FCSTD DOCUMENT  (FreeCAD 0.17R13541 (Git))
Label: SANPORobotLaserCut2DModel
License: All rights reserved
LicenseURL: http://en.wikipedia.org/wiki/All_rights_reserved
objects: Sketcher::SketchObject×37, PartDesign::Body×1
note: 38 computed .brp shape members not serialized (recipe doc carries the construction recipe); baked Part::Feature solids carry a one-line shape summary decoded from their .brp

FEATURE [Sketcher::SketchObject] Sketch  label="A4Size"
  MapMode = 5
  Support = -> [XY_Plane]
  sketch-geometry (4):
    g0: LineSegment StartX=0 StartY=0 StartZ=0 EndX=210 EndY=0 EndZ=0
    g1: LineSegment StartX=210 StartY=0 StartZ=0 EndX=210 EndY=297 EndZ=0
    g2: LineSegment StartX=210 StartY=297 StartZ=0 EndX=0 EndY=297 EndZ=0
    g3: LineSegment StartX=0 StartY=297 StartZ=0 EndX=0 EndY=0 EndZ=0
  constraints (11):
    c: Coincident(g0,g1)
    c: Coincident(g1,g2)
    c: Coincident(g2,g3)
    c: Coincident(g3,g0)
    c: Horizontal(g0)
    c: Horizontal(g2)
    c: Vertical(g1)
    c: Vertical(g3)
    c: DistanceY(g3,g3) = 297
    c: DistanceX(g0,g0) = 210
    c: Coincident(g0,g-1)
FEATURE [Sketcher::SketchObject] Sketch025  label="Sketch017"
  MapMode = 5
  Support = -> [XY_Plane]
  sketch-geometry (30):
    g0: LineSegment StartX=101 StartY=286 StartZ=0 EndX=134 EndY=286 EndZ=0
    g1: LineSegment StartX=132 StartY=234 StartZ=0 EndX=103 EndY=234 EndZ=0
    g2: ArcOfCircle CenterX=132 CenterY=236 CenterZ=0 NormalX=0 NormalY=0 NormalZ=1 AngleXU=0 Radius=2 StartAngle=4.71239 EndAngle=6.28319
    g3: ArcOfCircle CenterX=103 CenterY=236 CenterZ=0 NormalX=0 NormalY=0 NormalZ=1 AngleXU=0 Radius=2 StartAngle=3.14159 EndAngle=4.71239
    g4: Circle CenterX=117.5 CenterY=281.5 CenterZ=0 NormalX=0 NormalY=0 NormalZ=1 AngleXU=0 Radius=1.5
    g5: Circle CenterX=117.5 CenterY=238.5 CenterZ=0 NormalX=0 NormalY=0 NormalZ=1 AngleXU=0 Radius=1.5
    g6: LineSegment StartX=125 StartY=283 StartZ=0 EndX=130 EndY=283 EndZ=0
    g7: LineSegment StartX=130 StartY=283 StartZ=0 EndX=130 EndY=280 EndZ=0
    g8: LineSegment StartX=130 StartY=280 StartZ=0 EndX=125 EndY=280 EndZ=0
    g9: LineSegment StartX=125 StartY=280 StartZ=0 EndX=125 EndY=283 EndZ=0
    g10: LineSegment StartX=105 StartY=283 StartZ=0 EndX=110 EndY=283 EndZ=0
    g11: LineSegment StartX=110 StartY=283 StartZ=0 EndX=110 EndY=280 EndZ=0
    g12: LineSegment StartX=110 StartY=280 StartZ=0 EndX=105 EndY=280 EndZ=0
    g13: LineSegment StartX=105 StartY=280 StartZ=0 EndX=105 EndY=283 EndZ=0
    g14: LineSegment StartX=105 StartY=240 StartZ=0 EndX=110 EndY=240 EndZ=0
    g15: LineSegment StartX=110 StartY=240 StartZ=0 EndX=110 EndY=237 EndZ=0
    g16: LineSegment StartX=110 StartY=237 StartZ=0 EndX=105 EndY=237 EndZ=0
    g17: LineSegment StartX=105 StartY=237 StartZ=0 EndX=105 EndY=240 EndZ=0
    g18: LineSegment StartX=125 StartY=240 StartZ=0 EndX=130 EndY=240 EndZ=0
    g19: LineSegment StartX=130 StartY=240 StartZ=0 EndX=130 EndY=237 EndZ=0
    g20: LineSegment StartX=130 StartY=237 StartZ=0 EndX=125 EndY=237 EndZ=0
    g21: LineSegment StartX=125 StartY=237 StartZ=0 EndX=125 EndY=240 EndZ=0
    g22: LineSegment StartX=101 StartY=286 StartZ=0 EndX=101 EndY=261.25 EndZ=0
    g23: LineSegment StartX=101 StartY=236 StartZ=0 EndX=101 EndY=260.75 EndZ=0
    g24: LineSegment StartX=117.5 StartY=249 StartZ=0 EndX=118.5 EndY=250.732 EndZ=0
    g25: LineSegment StartX=118.5 StartY=250.732 StartZ=0 EndX=116.5 EndY=250.732 EndZ=0
    g26: LineSegment StartX=116.5 StartY=250.732 StartZ=0 EndX=117.5 EndY=249 EndZ=0
    g27: Circle [constr] CenterX=117.5 CenterY=250.155 CenterZ=0 NormalX=0 NormalY=0 NormalZ=1 AngleXU=0 Radius=1.1547
    g28: LineSegment StartX=134 StartY=286 StartZ=0 EndX=134 EndY=261.25 EndZ=0
    g29: LineSegment StartX=134 StartY=236 StartZ=0 EndX=134 EndY=260.75 EndZ=0
  constraints (91):
    c: Horizontal(g0)
    c: Horizontal(g1)
    c: Tangent(g1,g2) = 1.5708
    c: Tangent(g1,g3) = 1.5708
    c: Radius(g4) = 1.5
    c: Equal(g4,g5)
    c: Coincident(g6,g7)
    c: Coincident(g7,g8)
    c: Coincident(g8,g9)
    c: Coincident(g9,g6)
    c: Horizontal(g6)
    c: Horizontal(g8)
    c: Vertical(g7)
    c: Vertical(g9)
    c: Coincident(g10,g11)
    c: Coincident(g11,g12)
    c: Coincident(g12,g13)
    c: Coincident(g13,g10)
    c: Horizontal(g10)
    c: Horizontal(g12)
    c: Vertical(g11)
    c: Vertical(g13)
    c: Coincident(g14,g15)
    c: Coincident(g15,g16)
    c: Coincident(g16,g17)
    c: Coincident(g17,g14)
    c: Horizontal(g14)
    c: Horizontal(g16)
    c: Vertical(g17)
    c: Coincident(g18,g19)
    c: Coincident(g19,g20)
    c: Coincident(g20,g21)
    c: Coincident(g21,g18)
    c: Horizontal(g18)
    c: Horizontal(g20)
    c: Vertical(g19)
    c: Vertical(g21)
    c: DistanceX(g8,g8) = 5
    c: DistanceY(g9,g9) = 3
    c: DistanceX(g4,g8) = 7.5
    c: DistanceX(g12,g12) = 5
    c: DistanceY(g13,g13) = 3
    c: DistanceX(g11,g4) = 7.5
    c: DistanceX(g20,g20) = 5
    c: DistanceY(g21,g21) = 3
    c: DistanceY(g17,g17) = 3
    c: DistanceX(g16,g16) = 5
    c: DistanceX(g15,g5) = 7.5
    c: DistanceX(g5,g20) = 7.5
    c: Vertical(g22)
    c: Vertical(g23)
    c: DistanceY(g23,g22) = 0.5
    c: Equal(g22,g23)
    c: Tangent(g23,g3) = 1.5708
    c: DistanceX(g3,g16) = 4
    c: DistanceY(g14,g12) = 40
    c: DistanceY(g1,g16) = 3
    c: DistanceY(g10,g0) = 3
    c: DistanceY(g1,g5) = 4.5
    c: DistanceY(g1,g19) = 3
    c: DistanceX(g19,g2) = 4
    c: DistanceY(g4,g0) = 4.5
    c: Vertical(g22,g23)
    c: DistanceY(g6,g0) = 3
    c: Vertical(g15)
    c: Coincident(g0,g22)
    c: DistanceX(g0,g10) = 4
    c: Radius(g2) = 2
    c: Radius(g3) = 2
    c: Coincident(g24,g25)
    c: Coincident(g25,g26)
    c: Coincident(g26,g24)
    c: Equal(g24,g25)
    c: Equal(g24,g26)
    c: PointOnObject(g24,g27)
    c: PointOnObject(g25,g27)
    c: PointOnObject(g26,g27)
    c: Horizontal(g25)
    c: DistanceX(g25,g25) = 2
    c: DistanceY(g1,g24) = 15
    c: Vertical(g28)
    c: Vertical(g29)
    c: Vertical(g28,g29)
    c: DistanceY(g29,g28) = 0.5
    c: Horizontal(g23,g29)
    c: DistanceX(g3,g24) = 16.5
    c: Coincident(g0,g28)
    c: Tangent(g2,g29) = -1.5708
    c: DistanceX(g0,g0) = 33
    c: DistanceX(g1) = 103
    c: DistanceY(g1) = 234
FEATURE [Sketcher::SketchObject] Sketch039
  MapMode = 5
  sketch-geometry (30):
    g0: LineSegment StartX=187 StartY=191 StartZ=0 EndX=201 EndY=191 EndZ=0
    g1: LineSegment StartX=203 StartY=189 StartZ=0 EndX=203 EndY=188 EndZ=0
    g2: LineSegment StartX=201 StartY=150 StartZ=0 EndX=187 EndY=150 EndZ=0
    g3: LineSegment StartX=185 StartY=152 StartZ=0 EndX=185 EndY=153 EndZ=0
    g4: ArcOfCircle CenterX=187 CenterY=189 CenterZ=0 NormalX=0 NormalY=0 NormalZ=1 AngleXU=0 Radius=2 StartAngle=1.5708 EndAngle=3.14159
    g5: ArcOfCircle CenterX=201 CenterY=189 CenterZ=0 NormalX=0 NormalY=0 NormalZ=1 AngleXU=0 Radius=2 StartAngle=0 EndAngle=1.5708
    g6: ArcOfCircle CenterX=187 CenterY=152 CenterZ=0 NormalX=0 NormalY=0 NormalZ=1 AngleXU=0 Radius=2 StartAngle=3.14159 EndAngle=4.71239
    g7: ArcOfCircle CenterX=201 CenterY=152 CenterZ=0 NormalX=0 NormalY=0 NormalZ=1 AngleXU=0 Radius=2 StartAngle=4.71239 EndAngle=6.28319
    g8: LineSegment StartX=199 StartY=156 StartZ=0 EndX=203 EndY=156 EndZ=0
    g9: LineSegment StartX=203 StartY=153 StartZ=0 EndX=199 EndY=153 EndZ=0
    g10: LineSegment StartX=199 StartY=153 StartZ=0 EndX=199 EndY=156 EndZ=0
    g11: Circle CenterX=194 CenterY=154.5 CenterZ=0 NormalX=0 NormalY=0 NormalZ=1 AngleXU=0 Radius=1.5
    g12: LineSegment [constr] StartX=194 StartY=150 StartZ=0 EndX=194 EndY=191 EndZ=0
    g13: LineSegment StartX=203 StartY=153 StartZ=0 EndX=203 EndY=152 EndZ=0
    g14: LineSegment StartX=185 StartY=156 StartZ=0 EndX=189 EndY=156 EndZ=0
    g15: LineSegment StartX=185 StartY=153 StartZ=0 EndX=189 EndY=153 EndZ=0
    g16: LineSegment StartX=189 StartY=156 StartZ=0 EndX=189 EndY=153 EndZ=0
    g17: LineSegment StartX=199 StartY=188 StartZ=0 EndX=203 EndY=188 EndZ=0
    g18: LineSegment StartX=203 StartY=185 StartZ=0 EndX=199 EndY=185 EndZ=0
    g19: LineSegment StartX=199 StartY=185 StartZ=0 EndX=199 EndY=188 EndZ=0
    g20: LineSegment StartX=185 StartY=185 StartZ=0 EndX=189 EndY=185 EndZ=0
    g21: LineSegment StartX=189 StartY=185 StartZ=0 EndX=189 EndY=188 EndZ=0
    g22: LineSegment StartX=189 StartY=188 StartZ=0 EndX=185 EndY=188 EndZ=0
    g23: Circle CenterX=194 CenterY=186.5 CenterZ=0 NormalX=0 NormalY=0 NormalZ=1 AngleXU=0 Radius=1.5
    g24: LineSegment StartX=185 StartY=188 StartZ=0 EndX=185 EndY=189 EndZ=0
    g25: Circle CenterX=194 CenterY=177 CenterZ=0 NormalX=0 NormalY=0 NormalZ=1 AngleXU=0 Radius=3.4
    g26: LineSegment StartX=203 StartY=185 StartZ=0 EndX=203 EndY=170.75 EndZ=0
    g27: LineSegment StartX=203 StartY=156 StartZ=0 EndX=203 EndY=170.25 EndZ=0
    g28: LineSegment StartX=185 StartY=185 StartZ=0 EndX=185 EndY=170.75 EndZ=0
    g29: LineSegment StartX=185 StartY=156 StartZ=0 EndX=185 EndY=170.25 EndZ=0
  constraints (92):
    c: Horizontal(g0)
    c: Horizontal(g2)
    c: Vertical(g1)
    c: Vertical(g3)
    c: Tangent(g0,g4) = 1.5708
    c: Tangent(g0,g5) = 1.5708
    c: Tangent(g1,g5) = 1.5708
    c: Tangent(g2,g6) = 1.5708
    c: Tangent(g3,g6) = 1.5708
    c: Radius(g4) = 2
    c: Equal(g4,g5)
    c: Equal(g4,g6)
    c: Equal(g4,g7)
    c: DistanceX(g3,g13) = 18
    c: Coincident(g9,g10)
    c: Coincident(g10,g8)
    c: Horizontal(g8)
    c: Horizontal(g9)
    c: Vertical(g10)
    c: PointOnObject(g9,g1)
    c: DistanceY(g2,g9) = 3
    c: DistanceY(g10,g10) = 3
    c: DistanceX(g9,g9) = 4
    c: PointOnObject(g12,g2)
    c: PointOnObject(g12,g0)
    c: Vertical(g12)
    c: Symmetric(g3,g13,g12)
    c: PointOnObject(g11,g12)
    c: Radius(g11) = 1.5
    c: DistanceY(g12,g11) = 4.5
    c: PointOnObject(g13,g9)
    c: PointOnObject(g8,g1)
    c: PointOnObject(g14,g3)
    c: Horizontal(g14,g8)
    c: Horizontal(g3,g9)
    c: Horizontal(g14)
    c: Coincident(g15,g3)
    c: Horizontal(g15)
    c: Coincident(g16,g14)
    c: Coincident(g16,g15)
    c: Vertical(g16)
    c: DistanceX(g15,g15) = 4
    c: Horizontal(g4,g4)
    c: Coincident(g18,g19)
    c: Coincident(g19,g17)
    c: Horizontal(g17)
    c: Horizontal(g18)
    c: Vertical(g19)
    c: PointOnObject(g18,g1)
    c: Coincident(g20,g21)
    c: Coincident(g21,g22)
    c: Horizontal(g20)
    c: Horizontal(g22)
    c: Vertical(g21)
    c: PointOnObject(g23,g12)
    c: DistanceY(g23,g12) = 4.5
    c: DistanceY(g17,g0) = 3
    c: DistanceY(g22,g0) = 3
    c: DistanceY(g21,g21) = 3
    c: DistanceY(g19,g19) = 3
    c: Radius(g23) = 1.5
    c: DistanceX(g18,g18) = 4
    c: PointOnObject(g1,g17)
    c: DistanceX(g17,g17) = 4
    c: PointOnObject(g24,g22)
    c: DistanceX(g20,g20) = 4
    c: DistanceX(g22,g22) = 4
    c: PointOnObject(g25,g12)
    c: Radius(g25) = 3.4
    c: Coincident(g26,g18)
    c: Vertical(g26)
    c: Coincident(g27,g8)
    c: Vertical(g27)
    c: DistanceY(g27,g26) = 0.5
    c: Equal(g26,g27)
    c: Coincident(g28,g20)
    c: Vertical(g28)
    c: Coincident(g29,g14)
    c: Vertical(g29)
    c: DistanceY(g29,g28) = 0.5
    c: Equal(g28,g29)
    c: Tangent(g24,g4) = 1.5708
    c: Coincident(g24,g22)
    c: DistanceX(g4,g1) = 18
    c: DistanceY(g12,g25) = 27
    c: Tangent(g13,g7) = 1.5708
    c: Tangent(g2,g7) = 1.5708
    c: Coincident(g9,g13)
    c: DistanceY(g14,g20) = 29
    c: DistanceY(g25,g20) = 8
    c: DistanceX(g2) = 187
    c: DistanceY(g2) = 150
FEATURE [Sketcher::SketchObject] Sketch046
  MapMode = 5
  Support = -> [XY_Plane]
  sketch-geometry (29):
    g0: LineSegment StartX=7 StartY=170 StartZ=0 EndX=36 EndY=170 EndZ=0
    g1: LineSegment StartX=38 StartY=148 StartZ=0 EndX=34 EndY=148 EndZ=0
    g2: LineSegment StartX=34 StartY=148 StartZ=0 EndX=34 EndY=143 EndZ=0
    g3: LineSegment StartX=34 StartY=143 StartZ=0 EndX=29 EndY=143 EndZ=0
    g4: LineSegment StartX=29 StartY=143 StartZ=0 EndX=29 EndY=148 EndZ=0
    g5: LineSegment StartX=23 StartY=148 StartZ=0 EndX=23 EndY=152 EndZ=0
    g6: LineSegment StartX=23 StartY=152 StartZ=0 EndX=24.3 EndY=152 EndZ=0
    g7: LineSegment StartX=24.3 StartY=152 StartZ=0 EndX=24.3 EndY=154.5 EndZ=0
    g8: LineSegment StartX=24.3 StartY=154.5 StartZ=0 EndX=23 EndY=154.5 EndZ=0
    g9: LineSegment StartX=23 StartY=154.5 StartZ=0 EndX=23 EndY=156 EndZ=0
    g10: LineSegment StartX=23 StartY=156 StartZ=0 EndX=20 EndY=156 EndZ=0
    g11: LineSegment StartX=20 StartY=156 StartZ=0 EndX=20 EndY=154.5 EndZ=0
    g12: LineSegment StartX=20 StartY=154.5 StartZ=0 EndX=18.7 EndY=154.5 EndZ=0
    g13: LineSegment StartX=18.7 StartY=154.5 StartZ=0 EndX=18.7 EndY=152 EndZ=0
    g14: LineSegment StartX=18.7 StartY=152 StartZ=0 EndX=20 EndY=152 EndZ=0
    g15: LineSegment StartX=20 StartY=152 StartZ=0 EndX=20 EndY=148 EndZ=0
    g16: LineSegment StartX=14 StartY=148 StartZ=0 EndX=14 EndY=143 EndZ=0
    g17: LineSegment StartX=14 StartY=143 StartZ=0 EndX=9 EndY=143 EndZ=0
    g18: LineSegment StartX=9 StartY=143 StartZ=0 EndX=9 EndY=148 EndZ=0
    g19: LineSegment StartX=9 StartY=148 StartZ=0 EndX=5 EndY=148 EndZ=0
    g20: ArcOfCircle CenterX=7 CenterY=168 CenterZ=0 NormalX=0 NormalY=0 NormalZ=1 AngleXU=0 Radius=2 StartAngle=1.5708 EndAngle=3.14159
    g21: ArcOfCircle CenterX=36 CenterY=168 CenterZ=0 NormalX=0 NormalY=0 NormalZ=1 AngleXU=0 Radius=2 StartAngle=0 EndAngle=1.5708
    g22: Circle CenterX=29 CenterY=164 CenterZ=0 NormalX=0 NormalY=0 NormalZ=1 AngleXU=0 Radius=1.5
    g23: LineSegment StartX=5 StartY=168 StartZ=0 EndX=5 EndY=158.25 EndZ=0
    g24: LineSegment StartX=5 StartY=148 StartZ=0 EndX=5 EndY=157.75 EndZ=0
    g25: LineSegment StartX=38 StartY=168 StartZ=0 EndX=38 EndY=158.25 EndZ=0
    g26: LineSegment StartX=38 StartY=148 StartZ=0 EndX=38 EndY=157.75 EndZ=0
    g27: LineSegment StartX=23 StartY=148 StartZ=0 EndX=29 EndY=148 EndZ=0
    g28: LineSegment StartX=14 StartY=148 StartZ=0 EndX=20 EndY=148 EndZ=0
  constraints (88):
    c: Horizontal(g0)
    c: Horizontal(g1)
    c: Coincident(g1,g2)
    c: Vertical(g2)
    c: Coincident(g2,g3)
    c: Horizontal(g3)
    c: Coincident(g3,g4)
    c: Vertical(g4)
    c: Vertical(g5)
    c: Coincident(g5,g6)
    c: Horizontal(g6)
    c: Coincident(g6,g7)
    c: Vertical(g7)
    c: Coincident(g7,g8)
    c: Horizontal(g8)
    c: Coincident(g8,g9)
    c: Vertical(g9)
    c: Coincident(g9,g10)
    c: Coincident(g10,g11)
    c: Vertical(g11)
    c: Coincident(g11,g12)
    c: Horizontal(g12)
    c: Coincident(g12,g13)
    c: Vertical(g13)
    c: Coincident(g13,g14)
    c: Horizontal(g14)
    c: Coincident(g14,g15)
    c: Vertical(g15)
    c: Vertical(g16)
    c: Coincident(g16,g17)
    c: Horizontal(g17)
    c: Vertical(g18)
    c: Coincident(g18,g19)
    c: Horizontal(g19)
    c: DistanceX(g10,g10) = 3
    c: DistanceY(g18,g18) = 5
    c: DistanceY(g2,g2) = 5
    c: DistanceY(g16,g16) = 5
    c: DistanceY(g4,g4) = 5
    c: DistanceX(g17,g17) = 5
    c: DistanceX(g19,g19) = 4
    c: DistanceX(g3,g3) = 5
    c: DistanceX(g1,g1) = 4
    c: Horizontal(g17,g3)
    c: DistanceY(g11,g11) = 1.5
    c: DistanceX(g8,g8) = 1.3
    c: DistanceX(g12,g12) = 1.3
    c: DistanceX(g14,g14) = 1.3
    c: DistanceX(g6,g6) = 1.3
    c: DistanceY(g13,g13) = 2.5
    c: DistanceY(g7,g7) = 2.5
    c: DistanceY(g15,g15) = 4
    c: DistanceX(g16,g15) = 6
    c: DistanceX(g5,g4) = 6
    c: Tangent(g0,g20) = 1.5708
    c: Radius(g20) = 2
    c: Radius(g21) = 2
    c: Radius(g22) = 1.5
    c: DistanceY(g22,g0) = 6
    c: Vertical(g23)
    c: Coincident(g24,g19)
    c: Vertical(g24)
    c: Tangent(g23,g20) = -1.5708
    c: Vertical(g23,g24)
    c: DistanceY(g24,g23) = 0.5
    c: Equal(g23,g24)
    c: Vertical(g25)
    c: Coincident(g26,g1)
    c: Vertical(g26)
    c: Vertical(g25,g26)
    c: DistanceY(g26,g25) = 0.5
    c: Equal(g25,g26)
    c: Tangent(g25,g21) = 1.5708
    c: DistanceX(g22,g21) = 9
    c: Tangent(g0,g21) = 1.5708
    c: Coincident(g5,g27)
    c: Horizontal(g27)
    c: DistanceY(g5,g5) = 4
    c: Coincident(g28,g15)
    c: Horizontal(g28)
    c: Coincident(g27,g4)
    c: DistanceY(g9,g9) = 1.5
    c: Coincident(g16,g28)
    c: DistanceX(g20,g21) = 33
    c: DistanceY(g1,g22) = 16
    c: Coincident(g17,g18)
    c: DistanceX(g17) = 9
    c: DistanceY(g17) = 143
FEATURE [Sketcher::SketchObject] Sketch051
  MapMode = 5
  Support = -> [XY_Plane]
  sketch-geometry (61):
    g0: ArcOfCircle CenterX=10 CenterY=70 CenterZ=0 NormalX=0 NormalY=0 NormalZ=1 AngleXU=0 Radius=5 StartAngle=1.5708 EndAngle=3.14159
    g1: LineSegment StartX=10 StartY=75 StartZ=0 EndX=80 EndY=75 EndZ=0
    g2: ArcOfCircle CenterX=80 CenterY=70 CenterZ=0 NormalX=0 NormalY=0 NormalZ=1 AngleXU=0 Radius=5 StartAngle=0 EndAngle=1.5708
    g3: LineSegment StartX=17 StartY=5 StartZ=0 EndX=73 EndY=5 EndZ=0
    g4: LineSegment StartX=35 StartY=11 StartZ=0 EndX=55 EndY=11 EndZ=0
    g5: LineSegment StartX=55 StartY=11 StartZ=0 EndX=55 EndY=8 EndZ=0
    g6: LineSegment StartX=55 StartY=8 StartZ=0 EndX=35 EndY=8 EndZ=0
    g7: LineSegment StartX=35 StartY=8 StartZ=0 EndX=35 EndY=11 EndZ=0
    g8: Circle CenterX=35.5 CenterY=16 CenterZ=0 NormalX=0 NormalY=0 NormalZ=1 AngleXU=0 Radius=1.5
    g9: Circle CenterX=20.6 CenterY=67 CenterZ=0 NormalX=0 NormalY=0 NormalZ=1 AngleXU=0 Radius=1.5
    g10: Circle CenterX=69.1 CenterY=68 CenterZ=0 NormalX=0 NormalY=0 NormalZ=1 AngleXU=0 Radius=1.5
    g11: LineSegment StartX=43.55 StartY=19.9 StartZ=0 EndX=46.45 EndY=19.9 EndZ=0
    g12: LineSegment StartX=46.45 StartY=19.9 StartZ=0 EndX=46.45 EndY=17 EndZ=0
    g13: LineSegment StartX=46.45 StartY=17 StartZ=0 EndX=43.55 EndY=17 EndZ=0
    g14: LineSegment StartX=43.55 StartY=17 StartZ=0 EndX=43.55 EndY=19.9 EndZ=0
    g15: Circle CenterX=11 CenterY=67.5 CenterZ=0 NormalX=0 NormalY=0 NormalZ=1 AngleXU=0 Radius=1.5
    g16: LineSegment StartX=14 StartY=69 StartZ=0 EndX=17 EndY=69 EndZ=0
    g17: LineSegment StartX=17 StartY=69 StartZ=0 EndX=17 EndY=66 EndZ=0
    g18: LineSegment StartX=17 StartY=66 StartZ=0 EndX=14 EndY=66 EndZ=0
    g19: LineSegment StartX=14 StartY=66 StartZ=0 EndX=14 EndY=69 EndZ=0
    g20: LineSegment StartX=5 StartY=70 StartZ=0 EndX=5 EndY=69 EndZ=0
    g21: LineSegment StartX=5 StartY=69 StartZ=0 EndX=8 EndY=69 EndZ=0
    g22: LineSegment StartX=8 StartY=69 StartZ=0 EndX=8 EndY=66 EndZ=0
    g23: LineSegment StartX=8 StartY=66 StartZ=0 EndX=5 EndY=66 EndZ=0
    g24: LineSegment StartX=5 StartY=66 StartZ=0 EndX=5 EndY=40 EndZ=0
    g25: Circle CenterX=79 CenterY=67.5 CenterZ=0 NormalX=0 NormalY=0 NormalZ=1 AngleXU=0 Radius=1.5
    g26: LineSegment StartX=73 StartY=69 StartZ=0 EndX=76 EndY=69 EndZ=0
    g27: LineSegment StartX=76 StartY=69 StartZ=0 EndX=76 EndY=66 EndZ=0
    g28: LineSegment StartX=76 StartY=66 StartZ=0 EndX=73 EndY=66 EndZ=0
    g29: LineSegment StartX=73 StartY=66 StartZ=0 EndX=73 EndY=69 EndZ=0
    g30: LineSegment StartX=85 StartY=70 StartZ=0 EndX=85 EndY=69 EndZ=0
    g31: LineSegment StartX=85 StartY=69 StartZ=0 EndX=82 EndY=69 EndZ=0
    g32: LineSegment StartX=82 StartY=69 StartZ=0 EndX=82 EndY=66 EndZ=0
    g33: LineSegment StartX=82 StartY=66 StartZ=0 EndX=85 EndY=66 EndZ=0
    g34: LineSegment StartX=85 StartY=66 StartZ=0 EndX=85 EndY=40 EndZ=0
    g35: LineSegment StartX=85 StartY=25 StartZ=0 EndX=82 EndY=25 EndZ=0
    g36: LineSegment StartX=82 StartY=25 StartZ=0 EndX=82 EndY=28 EndZ=0
    g37: LineSegment StartX=82 StartY=28 StartZ=0 EndX=85 EndY=28 EndZ=0
    g38: LineSegment StartX=85 StartY=28 StartZ=0 EndX=85 EndY=39.5 EndZ=0
    g39: Circle CenterX=79 CenterY=26.5 CenterZ=0 NormalX=0 NormalY=0 NormalZ=1 AngleXU=0 Radius=1.5
    g40: LineSegment StartX=73 StartY=28 StartZ=0 EndX=76 EndY=28 EndZ=0
    g41: LineSegment StartX=76 StartY=28 StartZ=0 EndX=76 EndY=25 EndZ=0
    g42: LineSegment StartX=76 StartY=25 StartZ=0 EndX=73 EndY=25 EndZ=0
    g43: LineSegment StartX=73 StartY=25 StartZ=0 EndX=73 EndY=28 EndZ=0
    g44: LineSegment StartX=5 StartY=25 StartZ=0 EndX=8 EndY=25 EndZ=0
    g45: LineSegment StartX=8 StartY=25 StartZ=0 EndX=8 EndY=28 EndZ=0
    g46: LineSegment StartX=8 StartY=28 StartZ=0 EndX=5 EndY=28 EndZ=0
    g47: LineSegment StartX=5 StartY=28 StartZ=0 EndX=5 EndY=39.5 EndZ=0
    g48: Circle CenterX=11 CenterY=26.5 CenterZ=0 NormalX=0 NormalY=0 NormalZ=1 AngleXU=0 Radius=1.5
    g49: LineSegment StartX=14 StartY=28 StartZ=0 EndX=17 EndY=28 EndZ=0
    g50: LineSegment StartX=17 StartY=28 StartZ=0 EndX=17 EndY=25 EndZ=0
    g51: LineSegment StartX=17 StartY=25 StartZ=0 EndX=14 EndY=25 EndZ=0
    g52: LineSegment StartX=14 StartY=25 StartZ=0 EndX=14 EndY=28 EndZ=0
    g53: LineSegment [constr] StartX=15 StartY=11 StartZ=0 EndX=75 EndY=11 EndZ=0
    g54: LineSegment [constr] StartX=75 StartY=11 StartZ=0 EndX=75 EndY=8 EndZ=0
    g55: LineSegment [constr] StartX=75 StartY=8 StartZ=0 EndX=15 EndY=8 EndZ=0
    g56: LineSegment [constr] StartX=15 StartY=8 StartZ=0 EndX=15 EndY=11 EndZ=0
    g57: LineSegment StartX=85 StartY=25 StartZ=0 EndX=74.7595 EndY=6.0492 EndZ=0
    g58: ArcOfCircle CenterX=73 CenterY=7 CenterZ=0 NormalX=0 NormalY=0 NormalZ=1 AngleXU=0 Radius=2 StartAngle=4.71239 EndAngle=5.78776
    g59: LineSegment StartX=5 StartY=25 StartZ=0 EndX=15.2405 EndY=6.0492 EndZ=0
    g60: ArcOfCircle CenterX=17 CenterY=7 CenterZ=0 NormalX=0 NormalY=0 NormalZ=1 AngleXU=0 Radius=2 StartAngle=3.63701 EndAngle=4.71239
  constraints (186):
    c: Coincident(g0,g1)
    c: Horizontal(g1)
    c: Horizontal(g3)
    c: Vertical(g2,g1)
    c: Horizontal(g2,g2)
    c: Coincident(g2,g1)
    c: Radius(g2) = 5
    c: Radius(g0) = 5
    c: Vertical(g0,g0)
    c: Horizontal(g0,g0)
    c: DistanceX(g1,g1) = 70
    c: Coincident(g4,g5)
    c: Coincident(g5,g6)
    c: Coincident(g6,g7)
    c: Coincident(g7,g4)
    c: Horizontal(g4)
    c: Horizontal(g6)
    c: Vertical(g5)
    c: Vertical(g7)
    c: DistanceX(g6,g6) = 20
    c: DistanceY(g7,g7) = 3
    c: DistanceY(g3,g6) = 3
    c: Radius(g9) = 1.5
    c: Radius(g10) = 1.5
    c: Radius(g8) = 1.5
    c: DistanceY(g3,g8) = 11
    c: DistanceY(g8,g9) = 51
    c: DistanceX(g9,g8) = 14.9
    c: DistanceX(g9,g10) = 48.5
    c: DistanceY(g8,g10) = 52
    c: Coincident(g11,g12)
    c: Coincident(g12,g13)
    c: Coincident(g13,g14)
    c: Coincident(g14,g11)
    c: Horizontal(g11)
    c: Horizontal(g13)
    c: Vertical(g12)
    c: Vertical(g14)
    c: DistanceX(g13,g13) = 2.9
    c: DistanceY(g14,g14) = 2.9
    c: DistanceY(g3,g13) = 12
    c: DistanceY(g3,g0) = 70
    c: Radius(g15) = 1.5
    c: DistanceY(g15,g0) = 7.5
    c: DistanceX(g0,g15) = 6
    c: Coincident(g16,g17)
    c: Coincident(g17,g18)
    c: Coincident(g18,g19)
    c: Coincident(g19,g16)
    c: Horizontal(g16)
    c: Horizontal(g18)
    c: Vertical(g17)
    c: Vertical(g19)
    c: DistanceX(g18,g18) = 3
    c: DistanceY(g19,g19) = 3
    c: DistanceY(g16,g0) = 6
    c: DistanceX(g0,g16) = 9
    c: Vertical(g20)
    c: Coincident(g20,g21)
    c: Horizontal(g21)
    c: Coincident(g21,g22)
    c: Vertical(g22)
    c: Coincident(g22,g23)
    c: Horizontal(g23)
    c: Coincident(g23,g24)
    c: Vertical(g24)
    c: DistanceY(g20,g20) = 1
    c: DistanceX(g21,g21) = 3
    c: DistanceY(g22,g22) = 3
    c: DistanceX(g23,g23) = 3
    c: Coincident(g26,g27)
    c: Coincident(g27,g28)
    c: Coincident(g28,g29)
    c: Coincident(g29,g26)
    c: Horizontal(g26)
    c: Horizontal(g28)
    c: Vertical(g27)
    c: Vertical(g29)
    c: Vertical(g30)
    c: Coincident(g30,g31)
    c: Horizontal(g31)
    c: Coincident(g31,g32)
    c: Vertical(g32)
    c: Coincident(g32,g33)
    c: Horizontal(g33)
    c: Coincident(g33,g34)
    c: Vertical(g34)
    c: Tangent(g0,g20) = -1.5708
    c: Radius(g25) = 1.5
    c: Tangent(g2,g30) = 1.5708
    c: DistanceY(g30,g30) = 1
    c: DistanceX(g31,g31) = 3
    c: DistanceY(g32,g32) = 3
    c: DistanceX(g33,g33) = 3
    c: DistanceX(g25,g2) = 6
    c: DistanceY(g25,g1) = 7.5
    c: DistanceY(g26,g1) = 6
    c: DistanceX(g26,g2) = 9
    c: DistanceX(g28,g28) = 3
    c: DistanceY(g29,g29) = 3
    c: DistanceY(g24,g0) = 35
    c: DistanceY(g34,g1) = 35
    c: Horizontal(g35)
    c: Coincident(g35,g36)
    c: Vertical(g36)
    c: Coincident(g36,g37)
    c: Horizontal(g37)
    c: Coincident(g37,g38)
    c: Vertical(g38)
    c: Coincident(g40,g41)
    c: Coincident(g41,g42)
    c: Coincident(g42,g43)
    c: Coincident(g43,g40)
    c: Horizontal(g40)
    c: Horizontal(g42)
    c: Vertical(g41)
    c: Vertical(g43)
    c: DistanceX(g35,g35) = 3
    c: DistanceY(g36,g36) = 3
    c: DistanceX(g37,g37) = 3
    c: Vertical(g34,g38)
    c: DistanceY(g38,g34) = 0.5
    c: DistanceX(g42,g42) = 3
    c: DistanceY(g43,g43) = 3
    c: Radius(g39) = 1.5
    c: DistanceY(g3,g39) = 21.5
    c: DistanceY(g3,g41) = 20
    c: Horizontal(g44)
    c: Coincident(g44,g45)
    c: Vertical(g45)
    c: Coincident(g45,g46)
    c: Horizontal(g46)
    c: Coincident(g46,g47)
    c: Vertical(g47)
    c: DistanceX(g44,g44) = 3
    c: DistanceY(g45,g45) = 3
    c: DistanceX(g46,g46) = 3
    c: Vertical(g24,g47)
    c: DistanceY(g47,g24) = 0.5
    c: Coincident(g49,g50)
    c: Coincident(g50,g51)
    c: Coincident(g51,g52)
    c: Coincident(g52,g49)
    c: Horizontal(g49)
    c: Horizontal(g51)
    c: Vertical(g50)
    c: Vertical(g52)
    c: Radius(g48) = 1.5
    c: DistanceX(g51,g51) = 3
    c: DistanceY(g52,g52) = 3
    c: DistanceY(g3,g48) = 21.5
    c: DistanceY(g3,g51) = 20
    c: DistanceX(g3) = 17
    c: DistanceY(g3) = 5
    c: DistanceX(g50,g42) = 56
    c: Coincident(g53,g54)
    c: Coincident(g54,g55)
    c: Coincident(g55,g56)
    c: Coincident(g56,g53)
    c: Horizontal(g53)
    c: Horizontal(g55)
    c: Vertical(g54)
    c: Vertical(g56)
    c: DistanceY(g56,g56) = 3
    c: DistanceX(g55,g55) = 60
    c: DistanceX(g55,g6) = 20
    c: DistanceY(g3,g55) = 3
    c: DistanceY(g3,g35) = 20
    c: Coincident(g35,g57)
    c: Tangent(g57,g58) = 1.5708
    c: Tangent(g58,g3) = -1.5708
    c: Radius(g58) = 2
    c: DistanceX(g3,g3) = 56
    c: DistanceX(g39,g35) = 6
    c: DistanceX(g41,g35) = 9
    c: DistanceY(g3,g44) = 20
    c: Coincident(g44,g59)
    c: Tangent(g59,g60) = -1.5708
    c: Tangent(g60,g3) = -1.5708
    c: DistanceX(g44,g48) = 6
    c: DistanceX(g44,g51) = 9
    c: Vertical(g50,g3)
    c: Radius(g60) = 2
    c: DistanceX(g44,g6) = 30
    c: DistanceX(g44,g8) = 30.5
    c: DistanceX(g44,g13) = 38.55
FEATURE [Sketcher::SketchObject] Sketch052
  MapMode = 5
  Support = -> [XY_Plane]
  sketch-geometry (68):
    g0: ArcOfCircle CenterX=91 CenterY=70 CenterZ=0 NormalX=0 NormalY=0 NormalZ=1 AngleXU=0 Radius=5 StartAngle=1.5708 EndAngle=3.14159
    g1: LineSegment StartX=91 StartY=75 StartZ=0 EndX=161 EndY=75 EndZ=0
    g2: ArcOfCircle CenterX=161 CenterY=70 CenterZ=0 NormalX=0 NormalY=0 NormalZ=1 AngleXU=0 Radius=5 StartAngle=0 EndAngle=1.5708
    g3: LineSegment StartX=98 StartY=5 StartZ=0 EndX=154 EndY=5 EndZ=0
    g4: LineSegment StartX=116 StartY=11 StartZ=0 EndX=136 EndY=11 EndZ=0
    g5: LineSegment StartX=136 StartY=11 StartZ=0 EndX=136 EndY=8 EndZ=0
    g6: LineSegment StartX=136 StartY=8 StartZ=0 EndX=116 EndY=8 EndZ=0
    g7: LineSegment StartX=116 StartY=8 StartZ=0 EndX=116 EndY=11 EndZ=0
    g8: LineSegment StartX=122 StartY=50 StartZ=0 EndX=122 EndY=30 EndZ=0
    g9: ArcOfCircle CenterX=123.5 CenterY=30 CenterZ=0 NormalX=0 NormalY=0 NormalZ=1 AngleXU=0 Radius=1.5 StartAngle=3.14159 EndAngle=6.28319
    g10: LineSegment StartX=125 StartY=30 StartZ=0 EndX=125 EndY=50 EndZ=0
    g11: ArcOfCircle CenterX=123.5 CenterY=50 CenterZ=0 NormalX=0 NormalY=0 NormalZ=1 AngleXU=0 Radius=1.5 StartAngle=0 EndAngle=3.14159
    g12: LineSegment StartX=127 StartY=50 StartZ=0 EndX=127 EndY=30 EndZ=0
    g13: ArcOfCircle CenterX=128.5 CenterY=30 CenterZ=0 NormalX=0 NormalY=0 NormalZ=1 AngleXU=0 Radius=1.5 StartAngle=3.14159 EndAngle=6.28319
    g14: LineSegment StartX=130 StartY=30 StartZ=0 EndX=130 EndY=50 EndZ=0
    g15: ArcOfCircle CenterX=128.5 CenterY=50 CenterZ=0 NormalX=0 NormalY=0 NormalZ=1 AngleXU=0 Radius=1.5 StartAngle=0 EndAngle=3.14159
    g16: LineSegment StartX=98 StartY=47.5 StartZ=0 EndX=110.1 EndY=47.5 EndZ=0
    g17: LineSegment StartX=110.1 StartY=47.5 StartZ=0 EndX=110.1 EndY=25 EndZ=0
    g18: LineSegment StartX=110.1 StartY=25 StartZ=0 EndX=98 EndY=25 EndZ=0
    g19: LineSegment StartX=141.9 StartY=47.5 StartZ=0 EndX=154 EndY=47.5 EndZ=0
    g20: LineSegment StartX=154 StartY=25 StartZ=0 EndX=141.9 EndY=25 EndZ=0
    g21: LineSegment StartX=141.9 StartY=25 StartZ=0 EndX=141.9 EndY=47.5 EndZ=0
    g22: Circle CenterX=104.05 CenterY=50 CenterZ=0 NormalX=0 NormalY=0 NormalZ=1 AngleXU=0 Radius=1
    g23: Circle CenterX=104.05 CenterY=22.5 CenterZ=0 NormalX=0 NormalY=0 NormalZ=1 AngleXU=0 Radius=1
    g24: Circle CenterX=147.95 CenterY=22.5 CenterZ=0 NormalX=0 NormalY=0 NormalZ=1 AngleXU=0 Radius=1
    g25: Circle CenterX=147.95 CenterY=50 CenterZ=0 NormalX=0 NormalY=0 NormalZ=1 AngleXU=0 Radius=1
    g26: LineSegment StartX=86 StartY=70 StartZ=0 EndX=86 EndY=69 EndZ=0
    g27: LineSegment StartX=86 StartY=69 StartZ=0 EndX=89 EndY=69 EndZ=0
    g28: LineSegment StartX=89 StartY=69 StartZ=0 EndX=89 EndY=66 EndZ=0
    g29: LineSegment StartX=89 StartY=66 StartZ=0 EndX=86 EndY=66 EndZ=0
    g30: LineSegment StartX=86 StartY=66 StartZ=0 EndX=86 EndY=47.25 EndZ=0
    g31: Circle CenterX=92 CenterY=67.5 CenterZ=0 NormalX=0 NormalY=0 NormalZ=1 AngleXU=0 Radius=1.5
    g32: LineSegment StartX=95 StartY=69 StartZ=0 EndX=98 EndY=69 EndZ=0
    g33: LineSegment StartX=98 StartY=69 StartZ=0 EndX=98 EndY=66 EndZ=0
    g34: LineSegment StartX=98 StartY=66 StartZ=0 EndX=95 EndY=66 EndZ=0
    g35: LineSegment StartX=95 StartY=66 StartZ=0 EndX=95 EndY=69 EndZ=0
    g36: LineSegment StartX=166 StartY=70 StartZ=0 EndX=166 EndY=69 EndZ=0
    g37: LineSegment StartX=166 StartY=69 StartZ=0 EndX=163 EndY=69 EndZ=0
    g38: LineSegment StartX=163 StartY=69 StartZ=0 EndX=163 EndY=66 EndZ=0
    g39: LineSegment StartX=163 StartY=66 StartZ=0 EndX=166 EndY=66 EndZ=0
    g40: LineSegment StartX=166 StartY=66 StartZ=0 EndX=166 EndY=47.25 EndZ=0
    g41: Circle CenterX=160 CenterY=67.5 CenterZ=0 NormalX=0 NormalY=0 NormalZ=1 AngleXU=0 Radius=1.5
    g42: LineSegment StartX=154 StartY=69 StartZ=0 EndX=157 EndY=69 EndZ=0
    g43: LineSegment StartX=157 StartY=69 StartZ=0 EndX=157 EndY=66 EndZ=0
    g44: LineSegment StartX=157 StartY=66 StartZ=0 EndX=154 EndY=66 EndZ=0
    g45: LineSegment StartX=154 StartY=66 StartZ=0 EndX=154 EndY=69 EndZ=0
    g46: LineSegment StartX=86 StartY=25 StartZ=0 EndX=89 EndY=25 EndZ=0
    g47: LineSegment StartX=89 StartY=25 StartZ=0 EndX=89 EndY=28 EndZ=0
    g48: LineSegment StartX=89 StartY=28 StartZ=0 EndX=86 EndY=28 EndZ=0
    g49: LineSegment StartX=86 StartY=28 StartZ=0 EndX=86 EndY=46.75 EndZ=0
    g50: Circle CenterX=92 CenterY=26.5 CenterZ=0 NormalX=0 NormalY=0 NormalZ=1 AngleXU=0 Radius=1.5
    g51: LineSegment StartX=95 StartY=28 StartZ=0 EndX=98 EndY=28 EndZ=0
    g52: LineSegment StartX=98 StartY=25 StartZ=0 EndX=95 EndY=25 EndZ=0
    g53: LineSegment StartX=95 StartY=25 StartZ=0 EndX=95 EndY=28 EndZ=0
    g54: LineSegment StartX=166 StartY=25 StartZ=0 EndX=163 EndY=25 EndZ=0
    g55: LineSegment StartX=163 StartY=25 StartZ=0 EndX=163 EndY=28 EndZ=0
    g56: LineSegment StartX=163 StartY=28 StartZ=0 EndX=166 EndY=28 EndZ=0
    g57: LineSegment StartX=166 StartY=28 StartZ=0 EndX=166 EndY=46.75 EndZ=0
    g58: Circle CenterX=160 CenterY=26.5 CenterZ=0 NormalX=0 NormalY=0 NormalZ=1 AngleXU=0 Radius=1.5
    g59: LineSegment StartX=154 StartY=28 StartZ=0 EndX=157 EndY=28 EndZ=0
    g60: LineSegment StartX=157 StartY=28 StartZ=0 EndX=157 EndY=25 EndZ=0
    g61: LineSegment StartX=157 StartY=25 StartZ=0 EndX=154 EndY=25 EndZ=0
    g62: LineSegment StartX=98 StartY=47.5 StartZ=0 EndX=98 EndY=28 EndZ=0
    g63: LineSegment StartX=154 StartY=47.5 StartZ=0 EndX=154 EndY=28 EndZ=0
    g64: LineSegment StartX=166 StartY=25 StartZ=0 EndX=155.76 EndY=6.0492 EndZ=0
    g65: ArcOfCircle CenterX=154 CenterY=7 CenterZ=0 NormalX=0 NormalY=0 NormalZ=1 AngleXU=0 Radius=2 StartAngle=4.71239 EndAngle=5.78776
    g66: LineSegment StartX=86 StartY=25 StartZ=0 EndX=96.2405 EndY=6.0492 EndZ=0
    g67: ArcOfCircle CenterX=98 CenterY=7 CenterZ=0 NormalX=0 NormalY=0 NormalZ=1 AngleXU=0 Radius=2 StartAngle=3.63701 EndAngle=4.71239
  constraints (210):
    c: Coincident(g0,g1)
    c: Horizontal(g1)
    c: Horizontal(g3)
    c: Vertical(g2,g1)
    c: Horizontal(g2,g2)
    c: Coincident(g2,g1)
    c: Radius(g2) = 5
    c: Radius(g0) = 5
    c: Vertical(g0,g0)
    c: Horizontal(g0,g0)
    c: DistanceX(g1,g1) = 70
    c: Coincident(g4,g5)
    c: Coincident(g5,g6)
    c: Coincident(g6,g7)
    c: Coincident(g7,g4)
    c: Horizontal(g4)
    c: Horizontal(g6)
    c: Vertical(g5)
    c: Vertical(g7)
    c: DistanceX(g6,g6) = 20
    c: DistanceY(g7,g7) = 3
    c: DistanceY(g3,g6) = 3
    c: Vertical(g8)
    c: Tangent(g8,g9) = -1.5708
    c: Vertical(g10)
    c: Tangent(g10,g11) = -1.5708
    c: DistanceY(g10,g10) = 20
    c: Radius(g11) = 1.5
    c: Horizontal(g8,g9)
    c: Vertical(g12)
    c: Tangent(g12,g13) = -1.5708
    c: Vertical(g14)
    c: Tangent(g14,g15) = -1.5708
    c: Horizontal(g13,g12)
    c: DistanceY(g14,g14) = 20
    c: Radius(g15) = 1.5
    c: Coincident(g16,g17)
    c: Coincident(g17,g18)
    c: Horizontal(g16)
    c: Horizontal(g18)
    c: Vertical(g17)
    c: DistanceY(g18,g16) = 22.5
    c: DistanceX(g18,g18) = 12.1
    c: Coincident(g20,g21)
    c: Coincident(g21,g19)
    c: Horizontal(g19)
    c: Horizontal(g20)
    c: Vertical(g21)
    c: DistanceX(g20,g20) = 12.1
    c: DistanceY(g21,g21) = 22.5
    c: DistanceY(g3,g20) = 20
    c: DistanceY(g3,g17) = 20
    c: DistanceY(g3,g8) = 25
    c: DistanceY(g3,g13) = 25
    c: Radius(g22) = 1
    c: Radius(g25) = 1
    c: Radius(g24) = 1
    c: Radius(g23) = 1
    c: DistanceY(g16,g22) = 2.5
    c: DistanceX(g16,g22) = 6.05
    c: DistanceX(g25,g19) = 6.05
    c: DistanceY(g19,g25) = 2.5
    c: DistanceY(g23,g18) = 2.5
    c: DistanceX(g18,g23) = 6.05
    c: DistanceX(g24,g20) = 6.05
    c: DistanceY(g24,g20) = 2.5
    c: DistanceX(g14,g19) = 11.9
    c: DistanceX(g10,g12) = 2
    c: Tangent(g11,g8) = -1.5708
    c: Tangent(g9,g10) = -1.5708
    c: Tangent(g15,g12) = -1.5708
    c: Tangent(g13,g14) = -1.5708
    c: Vertical(g26)
    c: Coincident(g26,g27)
    c: Horizontal(g27)
    c: Coincident(g27,g28)
    c: Vertical(g28)
    c: Coincident(g28,g29)
    c: Horizontal(g29)
    c: Coincident(g29,g30)
    c: Vertical(g30)
    c: Tangent(g0,g26) = -1.5708
    c: DistanceY(g26,g26) = 1
    c: DistanceX(g27,g27) = 3
    c: DistanceY(g28,g28) = 3
    c: DistanceX(g29,g29) = 3
    c: Coincident(g32,g33)
    c: Coincident(g33,g34)
    c: Coincident(g34,g35)
    c: Coincident(g35,g32)
    c: Horizontal(g32)
    c: Horizontal(g34)
    c: Vertical(g33)
    c: Vertical(g35)
    c: Radius(g31) = 1.5
    c: DistanceX(g34,g34) = 3
    c: DistanceY(g35,g35) = 3
    c: DistanceX(g0,g31) = 6
    c: DistanceX(g0,g32) = 9
    c: DistanceY(g31,g0) = 7.5
    c: DistanceY(g32,g0) = 6
    c: DistanceY(g3,g0) = 70
    c: Vertical(g36)
    c: Coincident(g36,g37)
    c: Horizontal(g37)
    c: Coincident(g37,g38)
    c: Vertical(g38)
    c: Coincident(g38,g39)
    c: Horizontal(g39)
    c: Coincident(g39,g40)
    c: Vertical(g40)
    c: Tangent(g2,g36) = 1.5708
    c: DistanceY(g36,g36) = 1
    c: DistanceX(g37,g37) = 3
    c: DistanceY(g38,g38) = 3
    c: DistanceX(g39,g39) = 3
    c: Coincident(g42,g43)
    c: Coincident(g43,g44)
    c: Coincident(g44,g45)
    c: Coincident(g45,g42)
    c: Horizontal(g42)
    c: Horizontal(g44)
    c: Vertical(g43)
    c: Vertical(g45)
    c: Radius(g41) = 1.5
    c: DistanceX(g44,g44) = 3
    c: DistanceY(g45,g45) = 3
    c: DistanceX(g41,g2) = 6
    c: DistanceX(g42,g2) = 9
    c: DistanceY(g42,g1) = 6
    c: DistanceY(g41,g1) = 7.5
    c: Horizontal(g46)
    c: Coincident(g46,g47)
    c: Vertical(g47)
    c: Coincident(g47,g48)
    c: Horizontal(g48)
    c: Coincident(g48,g49)
    c: Vertical(g49)
    c: Vertical(g30,g49)
    c: DistanceY(g49,g30) = 0.5
    c: DistanceY(g47,g47) = 3
    c: Coincident(g52,g53)
    c: Coincident(g53,g51)
    c: Horizontal(g51)
    c: Horizontal(g52)
    c: Vertical(g53)
    c: DistanceX(g46,g46) = 3
    c: DistanceX(g48,g48) = 3
    c: DistanceX(g46,g52) = 9
    c: DistanceX(g52,g52) = 3
    c: DistanceY(g53,g53) = 3
    c: DistanceY(g3,g50) = 21.5
    c: DistanceY(g3,g52) = 20
    c: Equal(g30,g49)
    c: Radius(g50) = 1.5
    c: Horizontal(g54)
    c: Coincident(g54,g55)
    c: Vertical(g55)
    c: Coincident(g55,g56)
    c: Horizontal(g56)
    c: Coincident(g56,g57)
    c: Vertical(g57)
    c: Vertical(g40,g57)
    c: DistanceY(g57,g40) = 0.5
    c: DistanceX(g54,g54) = 3
    c: DistanceY(g55,g55) = 3
    c: DistanceX(g56,g56) = 3
    c: Coincident(g59,g60)
    c: Coincident(g60,g61)
    c: Horizontal(g59)
    c: Horizontal(g61)
    c: Vertical(g60)
    c: Radius(g58) = 1.5
    c: DistanceX(g61,g61) = 3
    c: DistanceY(g61,g59) = 3
    c: DistanceY(g3,g58) = 21.5
    c: DistanceY(g3,g61) = 20
    c: DistanceX(g58,g54) = 6
    c: Equal(g40,g57)
    c: DistanceY(g59,g43) = 38
    c: DistanceX(g3) = 98
    c: DistanceY(g3) = 5
    c: Coincident(g62,g16)
    c: Coincident(g62,g51)
    c: Vertical(g62)
    c: Coincident(g63,g19)
    c: Coincident(g63,g59)
    c: Vertical(g63)
    c: DistanceX(g19,g19) = 12.1
    c: DistanceX(g16,g16) = 12.1
    c: Coincident(g54,g64)
    c: Tangent(g64,g65) = 1.5708
    c: Coincident(g46,g66)
    c: Tangent(g66,g67) = -1.5708
    c: Tangent(g67,g3) = -1.5708
    c: Tangent(g65,g3) = -1.5708
    c: Radius(g65) = 2
    c: Radius(g67) = 2
    c: DistanceX(g3,g3) = 56
    c: DistanceX(g46,g50) = 6
    c: DistanceY(g3,g46) = 20
    c: Coincident(g18,g52)
    c: DistanceX(g46,g3) = 12
    c: Coincident(g20,g61)
    c: DistanceY(g3,g54) = 20
    c: DistanceX(g60,g54) = 9
    c: DistanceX(g46,g6) = 30
    c: DistanceX(g46,g8) = 36
    c: DistanceX(g13,g54) = 36
    c: DistanceY(g51,g34) = 38
FEATURE [Sketcher::SketchObject] Sketch064
  MapMode = 5
  Support = -> [XY_Plane]
  sketch-geometry (12):
    g0: LineSegment StartX=140 StartY=76 StartZ=0 EndX=166 EndY=76 EndZ=0
    g1: LineSegment StartX=166 StartY=94 StartZ=0 EndX=140 EndY=94 EndZ=0
    g2: ArcOfCircle CenterX=140 CenterY=92 CenterZ=0 NormalX=0 NormalY=0 NormalZ=1 AngleXU=0 Radius=2 StartAngle=1.5708 EndAngle=3.14159
    g3: ArcOfCircle CenterX=140 CenterY=78 CenterZ=0 NormalX=0 NormalY=0 NormalZ=1 AngleXU=0 Radius=2 StartAngle=3.14159 EndAngle=4.71239
    g4: LineSegment StartX=147.261 StartY=88.39 StartZ=0 EndX=161.526 EndY=87.2932 EndZ=0
    g5: ArcOfCircle CenterX=161.35 CenterY=85 CenterZ=0 NormalX=0 NormalY=0 NormalZ=1 AngleXU=0 Radius=2.3 StartAngle=4.78912 EndAngle=7.77725
    g6: LineSegment StartX=161.526 StartY=82.7068 StartZ=0 EndX=147.261 EndY=81.61 EndZ=0
    g7: ArcOfCircle CenterX=147 CenterY=85 CenterZ=0 NormalX=0 NormalY=0 NormalZ=1 AngleXU=0 Radius=3.4 StartAngle=1.49407 EndAngle=4.78912
    g8: LineSegment StartX=138 StartY=92 StartZ=0 EndX=138 EndY=85.25 EndZ=0
    g9: LineSegment StartX=138 StartY=78 StartZ=0 EndX=138 EndY=84.75 EndZ=0
    g10: LineSegment StartX=166 StartY=94 StartZ=0 EndX=166 EndY=85.25 EndZ=0
    g11: LineSegment StartX=166 StartY=76 StartZ=0 EndX=166 EndY=84.75 EndZ=0
  constraints (37):
    c: Horizontal(g0)
    c: Horizontal(g1)
    c: Tangent(g1,g2) = -1.5708
    c: Radius(g3) = 2
    c: Radius(g2) = 2
    c: DistanceX(g1,g1) = 26
    c: Tangent(g4,g5) = 1.5708
    c: Tangent(g6,g7) = 1.5708
    c: Radius(g7) = 3.4
    c: DistanceX(g7,g0) = 19
    c: Horizontal(g5,g7)
    c: DistanceX(g7,g5) = 14.35
    c: Radius(g5) = 2.3
    c: Tangent(g7,g4) = 1.5708
    c: Tangent(g5,g6) = 1.5708
    c: DistanceY(g0,g7) = 9
    c: Vertical(g8)
    c: Vertical(g9)
    c: Tangent(g8,g2) = -1.5708
    c: DistanceY(g9,g8) = 0.5
    c: Vertical(g8,g9)
    c: Equal(g8,g9)
    c: DistanceY(g9,g9) = 6.75
    c: Coincident(g10,g1)
    c: Vertical(g10)
    c: Coincident(g11,g0)
    c: Vertical(g11)
    c: Vertical(g10,g11)
    c: DistanceY(g11,g10) = 0.5
    c: Equal(g10,g11)
    c: DistanceX(g0,g0) = 26
    c: Tangent(g9,g3) = 1.5708
    c: DistanceX(g5,g0) = 4.65
    c: DistanceX(g3,g7) = 9
    c: Tangent(g3,g0) = -1.5708
    c: DistanceX(g0) = 140
    c: DistanceY(g0) = 76
FEATURE [Sketcher::SketchObject] Sketch083
  MapMode = 5
  Support = -> [XY_Plane]
  sketch-geometry (47):
    g0: LineSegment StartX=111 StartY=142 StartZ=0 EndX=111 EndY=115 EndZ=0
    g1: ArcOfCircle CenterX=97 CenterY=111 CenterZ=0 NormalX=0 NormalY=0 NormalZ=1 AngleXU=0 Radius=2 StartAngle=1.5708 EndAngle=3.14159
    g2: ArcOfCircle CenterX=97 CenterY=97 CenterZ=0 NormalX=0 NormalY=0 NormalZ=1 AngleXU=0 Radius=2 StartAngle=3.14159 EndAngle=4.71239
    g3: LineSegment StartX=111 StartY=93 StartZ=0 EndX=111 EndY=76 EndZ=0
    g4: Circle CenterX=104 CenterY=104 CenterZ=0 NormalX=0 NormalY=0 NormalZ=1 AngleXU=0 Radius=1.5
    g5: LineSegment StartX=123 StartY=142 StartZ=0 EndX=123 EndY=104.25 EndZ=0
    g6: LineSegment StartX=123 StartY=76 StartZ=0 EndX=123 EndY=103.75 EndZ=0
    g7: LineSegment StartX=95 StartY=111 StartZ=0 EndX=95 EndY=104.25 EndZ=0
    g8: LineSegment StartX=95 StartY=97 StartZ=0 EndX=95 EndY=103.75 EndZ=0
    g9: LineSegment StartX=123 StartY=142 StartZ=0 EndX=120 EndY=142 EndZ=0
    g10: LineSegment StartX=120 StartY=142 StartZ=0 EndX=120 EndY=139 EndZ=0
    g11: LineSegment StartX=114 StartY=139 StartZ=0 EndX=114 EndY=142 EndZ=0
    g12: LineSegment StartX=114 StartY=142 StartZ=0 EndX=111 EndY=142 EndZ=0
    g13: LineSegment StartX=123 StartY=76 StartZ=0 EndX=120 EndY=76 EndZ=0
    g14: LineSegment StartX=120 StartY=76 StartZ=0 EndX=120 EndY=79 EndZ=0
    g15: LineSegment StartX=114 StartY=79 StartZ=0 EndX=114 EndY=76 EndZ=0
    g16: LineSegment StartX=114 StartY=76 StartZ=0 EndX=111 EndY=76 EndZ=0
    g17: LineSegment StartX=97 StartY=113 StartZ=0 EndX=109 EndY=113 EndZ=0
    g18: ArcOfCircle CenterX=109 CenterY=115 CenterZ=0 NormalX=0 NormalY=0 NormalZ=1 AngleXU=0 Radius=2 StartAngle=4.71239 EndAngle=6.28319
    g19: LineSegment StartX=97 StartY=95 StartZ=0 EndX=109 EndY=95 EndZ=0
    g20: ArcOfCircle CenterX=109 CenterY=93 CenterZ=0 NormalX=0 NormalY=0 NormalZ=1 AngleXU=0 Radius=2 StartAngle=-4.4e-11 EndAngle=1.5708
    g21: LineSegment StartX=114 StartY=79 StartZ=0 EndX=115.5 EndY=79 EndZ=0
    g22: LineSegment StartX=115.5 StartY=79 StartZ=0 EndX=115.5 EndY=83 EndZ=0
    g23: LineSegment StartX=115.5 StartY=83 StartZ=0 EndX=114.2 EndY=83 EndZ=0
    g24: LineSegment StartX=114.2 StartY=83 StartZ=0 EndX=114.2 EndY=85.5 EndZ=0
    g25: LineSegment StartX=114.2 StartY=85.5 StartZ=0 EndX=115.5 EndY=85.5 EndZ=0
    g26: LineSegment StartX=115.5 StartY=85.5 StartZ=0 EndX=115.5 EndY=87 EndZ=0
    g27: LineSegment StartX=115.5 StartY=87 StartZ=0 EndX=118.5 EndY=87 EndZ=0
    g28: LineSegment StartX=118.5 StartY=87 StartZ=0 EndX=118.5 EndY=85.5 EndZ=0
    g29: LineSegment StartX=118.5 StartY=85.5 StartZ=0 EndX=119.8 EndY=85.5 EndZ=0
    g30: LineSegment StartX=119.8 StartY=85.5 StartZ=0 EndX=119.8 EndY=83 EndZ=0
    g31: LineSegment StartX=119.8 StartY=83 StartZ=0 EndX=118.5 EndY=83 EndZ=0
    g32: LineSegment StartX=118.5 StartY=83 StartZ=0 EndX=118.5 EndY=79 EndZ=0
    g33: LineSegment StartX=118.5 StartY=79 StartZ=0 EndX=120 EndY=79 EndZ=0
    g34: LineSegment StartX=114 StartY=139 StartZ=0 EndX=115.5 EndY=139 EndZ=0
    g35: LineSegment StartX=115.5 StartY=139 StartZ=0 EndX=115.5 EndY=135 EndZ=0
    g36: LineSegment StartX=115.5 StartY=135 StartZ=0 EndX=114.2 EndY=135 EndZ=0
    g37: LineSegment StartX=114.2 StartY=135 StartZ=0 EndX=114.2 EndY=132.5 EndZ=0
    g38: LineSegment StartX=114.2 StartY=132.5 StartZ=0 EndX=115.5 EndY=132.5 EndZ=0
    g39: LineSegment StartX=115.5 StartY=132.5 StartZ=0 EndX=115.5 EndY=131 EndZ=0
    g40: LineSegment StartX=115.5 StartY=131 StartZ=0 EndX=118.5 EndY=131 EndZ=0
    g41: LineSegment StartX=118.5 StartY=131 StartZ=0 EndX=118.5 EndY=132.5 EndZ=0
    g42: LineSegment StartX=118.5 StartY=132.5 StartZ=0 EndX=119.8 EndY=132.5 EndZ=0
    g43: LineSegment StartX=119.8 StartY=132.5 StartZ=0 EndX=119.8 EndY=135 EndZ=0
    g44: LineSegment StartX=119.8 StartY=135 StartZ=0 EndX=118.5 EndY=135 EndZ=0
    g45: LineSegment StartX=118.5 StartY=135 StartZ=0 EndX=118.5 EndY=139 EndZ=0
    g46: LineSegment StartX=118.5 StartY=139 StartZ=0 EndX=120 EndY=139 EndZ=0
  constraints (142):
    c: Vertical(g0)
    c: Vertical(g3)
    c: Radius(g2) = 2
    c: Radius(g1) = 2
    c: Radius(g4) = 1.5
    c: DistanceX(g4,g6) = 19
    c: Vertical(g5)
    c: Vertical(g6)
    c: Vertical(g5,g6)
    c: DistanceY(g6,g5) = 0.5
    c: Vertical(g7)
    c: Coincident(g8,g2)
    c: Vertical(g8)
    c: Tangent(g8,g2)
    c: Tangent(g7,g1) = -1.5708
    c: Vertical(g7,g8)
    c: DistanceY(g8,g7) = 0.5
    c: Equal(g7,g8)
    c: Horizontal(g9)
    c: Coincident(g9,g10)
    c: Vertical(g10)
    c: Vertical(g11)
    c: Coincident(g11,g12)
    c: Coincident(g12,g0)
    c: Horizontal(g12)
    c: Coincident(g13,g14)
    c: Vertical(g14)
    c: Vertical(g15)
    c: Coincident(g15,g16)
    c: Coincident(g16,g3)
    c: Horizontal(g16)
    c: Horizontal(g13)
    c: DistanceX(g13,g13) = 3
    c: DistanceX(g16,g16) = 3
    c: DistanceX(g15,g14) = 6
    c: DistanceX(g2,g6) = 28
    c: DistanceX(g11,g10) = 6
    c: DistanceX(g9,g9) = 3
    c: DistanceX(g12,g12) = 3
    c: Horizontal(g17)
    c: Tangent(g17,g18) = -1.5708
    c: Tangent(g18,g0) = 1.5708
    c: Tangent(g1,g17) = 1.5708
    c: Radius(g18) = 2
    c: Horizontal(g19)
    c: Tangent(g19,g20) = 1.5708
    c: Tangent(g20,g3) = 1.5708
    c: Tangent(g2,g19) = -1.5708
    c: Radius(g20) = 2
    c: Coincident(g6,g13)
    c: Coincident(g5,g9)
    c: DistanceY(g19,g4) = 9
    c: DistanceY(g4,g17) = 9
    c: Horizontal(g6,g8)
    c: Coincident(g15,g21)
    c: Horizontal(g21)
    c: Coincident(g21,g22)
    c: Vertical(g22)
    c: Coincident(g22,g23)
    c: Horizontal(g23)
    c: Coincident(g23,g24)
    c: Vertical(g24)
    c: Coincident(g24,g25)
    c: Horizontal(g25)
    c: Coincident(g25,g26)
    c: Vertical(g26)
    c: Coincident(g26,g27)
    c: Horizontal(g27)
    c: Coincident(g27,g28)
    c: Vertical(g28)
    c: Coincident(g28,g29)
    c: Horizontal(g29)
    c: Coincident(g29,g30)
    c: Vertical(g30)
    c: Coincident(g30,g31)
    c: Horizontal(g31)
    c: Coincident(g31,g32)
    c: Vertical(g32)
    c: Coincident(g32,g33)
    c: Coincident(g33,g14)
    c: Horizontal(g33)
    c: DistanceY(g15,g15) = 3
    c: DistanceY(g14,g14) = 3
    c: DistanceX(g21,g21) = 1.5
    c: DistanceX(g33,g33) = 1.5
    c: DistanceY(g22,g22) = 4
    c: DistanceY(g32,g32) = 4
    c: DistanceX(g23,g23) = 1.3
    c: DistanceX(g31,g31) = 1.3
    c: DistanceY(g24,g24) = 2.5
    c: DistanceY(g30,g30) = 2.5
    c: DistanceX(g25,g25) = 1.3
    c: DistanceX(g29,g29) = 1.3
    c: DistanceY(g26,g26) = 1.5
    c: DistanceY(g28,g28) = 1.5
    c: Coincident(g11,g34)
    c: Horizontal(g34)
    c: Coincident(g34,g35)
    c: Vertical(g35)
    c: Coincident(g35,g36)
    c: Horizontal(g36)
    c: Coincident(g36,g37)
    c: Vertical(g37)
    c: Coincident(g37,g38)
    c: Horizontal(g38)
    c: Coincident(g38,g39)
    c: Vertical(g39)
    c: Coincident(g39,g40)
    c: Horizontal(g40)
    c: Coincident(g40,g41)
    c: Vertical(g41)
    c: Coincident(g41,g42)
    c: Horizontal(g42)
    c: Coincident(g42,g43)
    c: Vertical(g43)
    c: Coincident(g43,g44)
    c: Horizontal(g44)
    c: Coincident(g44,g45)
    c: Vertical(g45)
    c: Coincident(g45,g46)
    c: Coincident(g46,g10)
    c: DistanceY(g11,g11) = 3
    c: DistanceY(g10,g10) = 3
    c: DistanceX(g34,g34) = 1.5
    c: Horizontal(g46)
    c: DistanceX(g46,g46) = 1.5
    c: DistanceY(g35,g35) = 4
    c: DistanceY(g45,g45) = 4
    c: DistanceX(g36,g36) = 1.3
    c: DistanceX(g44,g44) = 1.3
    c: DistanceY(g37,g37) = 2.5
    c: DistanceY(g43,g43) = 2.5
    c: DistanceX(g38,g38) = 1.3
    c: DistanceX(g42,g42) = 1.3
    c: DistanceY(g39,g39) = 1.5
    c: DistanceY(g41,g41) = 1.5
    c: DistanceY(g6,g5) = 66
    c: DistanceX(g3) = 111
    c: DistanceY(g3) = 76
    c: DistanceY(g3,g3) = 17
    c: DistanceY(g15,g19) = 16
    c: DistanceY(g17,g11) = 26
FEATURE [Sketcher::SketchObject] Sketch084
  MapMode = 5
  Support = -> [XY_Plane]
  sketch-geometry (47):
    g0: LineSegment StartX=66 StartY=76 StartZ=0 EndX=69 EndY=76 EndZ=0
    g1: LineSegment StartX=78 StartY=76 StartZ=0 EndX=78 EndY=93 EndZ=0
    g2: ArcOfCircle CenterX=92 CenterY=97 CenterZ=0 NormalX=0 NormalY=0 NormalZ=1 AngleXU=0 Radius=2 StartAngle=4.71239 EndAngle=6.28319
    g3: ArcOfCircle CenterX=92 CenterY=111 CenterZ=0 NormalX=0 NormalY=0 NormalZ=1 AngleXU=0 Radius=2 StartAngle=0 EndAngle=1.5708
    g4: LineSegment StartX=78 StartY=115 StartZ=0 EndX=78 EndY=142 EndZ=0
    g5: LineSegment StartX=69 StartY=142 StartZ=0 EndX=66 EndY=142 EndZ=0
    g6: Circle CenterX=85 CenterY=104 CenterZ=0 NormalX=0 NormalY=0 NormalZ=1 AngleXU=0 Radius=1.5
    g7: LineSegment StartX=66 StartY=142 StartZ=0 EndX=66 EndY=104.25 EndZ=0
    g8: LineSegment StartX=66 StartY=76 StartZ=0 EndX=66 EndY=103.75 EndZ=0
    g9: LineSegment StartX=94 StartY=111 StartZ=0 EndX=94 EndY=104.25 EndZ=0
    g10: LineSegment StartX=94 StartY=97 StartZ=0 EndX=94 EndY=103.75 EndZ=0
    g11: LineSegment StartX=75 StartY=139 StartZ=0 EndX=75 EndY=142 EndZ=0
    g12: LineSegment StartX=75 StartY=142 StartZ=0 EndX=78 EndY=142 EndZ=0
    g13: LineSegment StartX=75 StartY=79 StartZ=0 EndX=75 EndY=76 EndZ=0
    g14: LineSegment StartX=75 StartY=76 StartZ=0 EndX=78 EndY=76 EndZ=0
    g15: LineSegment StartX=92 StartY=113 StartZ=0 EndX=80 EndY=113 EndZ=0
    g16: ArcOfCircle CenterX=80 CenterY=115 CenterZ=0 NormalX=0 NormalY=0 NormalZ=1 AngleXU=0 Radius=2 StartAngle=3.14159 EndAngle=4.71239
    g17: LineSegment StartX=92 StartY=95 StartZ=0 EndX=80 EndY=95 EndZ=0
    g18: ArcOfCircle CenterX=80 CenterY=93 CenterZ=0 NormalX=0 NormalY=0 NormalZ=1 AngleXU=0 Radius=2 StartAngle=1.5708 EndAngle=3.14159
    g19: LineSegment StartX=69 StartY=139 StartZ=0 EndX=69 EndY=142 EndZ=0
    g20: LineSegment StartX=69 StartY=76 StartZ=0 EndX=69 EndY=79 EndZ=0
    g21: LineSegment StartX=69 StartY=79 StartZ=0 EndX=70.5 EndY=79 EndZ=0
    g22: LineSegment StartX=70.5 StartY=79 StartZ=0 EndX=70.5 EndY=83 EndZ=0
    g23: LineSegment StartX=70.5 StartY=83 StartZ=0 EndX=69.2 EndY=83 EndZ=0
    g24: LineSegment StartX=69.2 StartY=83 StartZ=0 EndX=69.2 EndY=85.5 EndZ=0
    g25: LineSegment StartX=69.2 StartY=85.5 StartZ=0 EndX=70.5 EndY=85.5 EndZ=0
    g26: LineSegment StartX=70.5 StartY=85.5 StartZ=0 EndX=70.5 EndY=87 EndZ=0
    g27: LineSegment StartX=70.5 StartY=87 StartZ=0 EndX=73.5 EndY=87 EndZ=0
    g28: LineSegment StartX=73.5 StartY=87 StartZ=0 EndX=73.5 EndY=85.5 EndZ=0
    g29: LineSegment StartX=73.5 StartY=85.5 StartZ=0 EndX=74.8 EndY=85.5 EndZ=0
    g30: LineSegment StartX=74.8 StartY=85.5 StartZ=0 EndX=74.8 EndY=83 EndZ=0
    g31: LineSegment StartX=74.8 StartY=83 StartZ=0 EndX=73.5 EndY=83 EndZ=0
    g32: LineSegment StartX=73.5 StartY=83 StartZ=0 EndX=73.5 EndY=79 EndZ=0
    g33: LineSegment StartX=73.5 StartY=79 StartZ=0 EndX=75 EndY=79 EndZ=0
    g34: LineSegment StartX=69 StartY=139 StartZ=0 EndX=70.5 EndY=139 EndZ=0
    g35: LineSegment StartX=70.5 StartY=139 StartZ=0 EndX=70.5 EndY=135 EndZ=0
    g36: LineSegment StartX=70.5 StartY=135 StartZ=0 EndX=69.2 EndY=135 EndZ=0
    g37: LineSegment StartX=69.2 StartY=135 StartZ=0 EndX=69.2 EndY=132.5 EndZ=0
    g38: LineSegment StartX=69.2 StartY=132.5 StartZ=0 EndX=70.5 EndY=132.5 EndZ=0
    g39: LineSegment StartX=70.5 StartY=132.5 StartZ=0 EndX=70.5 EndY=131 EndZ=0
    g40: LineSegment StartX=70.5 StartY=131 StartZ=0 EndX=73.5 EndY=131 EndZ=0
    g41: LineSegment StartX=73.5 StartY=131 StartZ=0 EndX=73.5 EndY=132.5 EndZ=0
    g42: LineSegment StartX=73.5 StartY=132.5 StartZ=0 EndX=74.8 EndY=132.5 EndZ=0
    g43: LineSegment StartX=74.8 StartY=132.5 StartZ=0 EndX=74.8 EndY=135 EndZ=0
    g44: LineSegment StartX=74.8 StartY=135 StartZ=0 EndX=73.5 EndY=135 EndZ=0
    g45: LineSegment StartX=73.5 StartY=135 StartZ=0 EndX=73.5 EndY=139 EndZ=0
    g46: LineSegment StartX=73.5 StartY=139 StartZ=0 EndX=75 EndY=139 EndZ=0
  constraints (140):
    c: Horizontal(g0)
    c: Vertical(g1)
    c: Vertical(g4)
    c: Horizontal(g5)
    c: Radius(g3) = 2
    c: Radius(g2) = 2
    c: DistanceX(g5,g5) = 3
    c: Radius(g6) = 1.5
    c: DistanceX(g0,g6) = 19
    c: Coincident(g7,g5)
    c: Vertical(g7)
    c: Coincident(g8,g0)
    c: Vertical(g8)
    c: Vertical(g7,g8)
    c: DistanceY(g8,g7) = 0.5
    c: Vertical(g9)
    c: Coincident(g10,g2)
    c: Vertical(g10)
    c: Tangent(g10,g2)
    c: Tangent(g9,g3) = 1.5708
    c: Vertical(g9,g10)
    c: DistanceY(g10,g9) = 0.5
    c: Equal(g9,g10)
    c: Vertical(g11)
    c: Coincident(g11,g12)
    c: Coincident(g12,g4)
    c: Horizontal(g12)
    c: DistanceX(g12,g12) = 3
    c: DistanceX(g0,g0) = 3
    c: Vertical(g13)
    c: Coincident(g13,g14)
    c: Coincident(g14,g1)
    c: Horizontal(g14)
    c: DistanceX(g20,g13) = 6
    c: DistanceX(g14,g14) = 3
    c: DistanceX(g0,g2) = 28
    c: Horizontal(g15)
    c: Tangent(g15,g16) = 1.5708
    c: Tangent(g16,g4) = 1.5708
    c: Tangent(g3,g15) = -1.5708
    c: Horizontal(g17)
    c: Tangent(g17,g18) = -1.5708
    c: Tangent(g18,g1) = 1.5708
    c: Tangent(g2,g17) = 1.5708
    c: Radius(g18) = 2
    c: Radius(g16) = 2
    c: DistanceX(g19,g11) = 6
    c: Coincident(g19,g5)
    c: Vertical(g19)
    c: DistanceY(g6,g7) = 0.25
    c: Coincident(g0,g20)
    c: Vertical(g20)
    c: DistanceY(g0,g5) = 66
    c: DistanceY(g17,g6) = 9
    c: DistanceY(g6,g15) = 9
    c: Coincident(g20,g21)
    c: Horizontal(g21)
    c: Coincident(g21,g22)
    c: Vertical(g22)
    c: Coincident(g22,g23)
    c: Horizontal(g23)
    c: Coincident(g23,g24)
    c: Vertical(g24)
    c: Coincident(g24,g25)
    c: Horizontal(g25)
    c: Coincident(g25,g26)
    c: Vertical(g26)
    c: Coincident(g26,g27)
    c: Horizontal(g27)
    c: Coincident(g27,g28)
    c: Vertical(g28)
    c: Coincident(g28,g29)
    c: Horizontal(g29)
    c: Coincident(g29,g30)
    c: Vertical(g30)
    c: Coincident(g30,g31)
    c: Horizontal(g31)
    c: Coincident(g31,g32)
    c: Vertical(g32)
    c: Coincident(g32,g33)
    c: Coincident(g33,g13)
    c: Horizontal(g33)
    c: DistanceX(g27,g27) = 3
    c: DistanceY(g22,g22) = 4
    c: DistanceY(g24,g24) = 2.5
    c: DistanceY(g26,g26) = 1.5
    c: DistanceY(g20,g20) = 3
    c: DistanceX(g23,g23) = 1.3
    c: DistanceY(g13,g13) = 3
    c: DistanceY(g32,g32) = 4
    c: DistanceY(g30,g30) = 2.5
    c: DistanceY(g28,g28) = 1.5
    c: DistanceX(g25,g25) = 1.3
    c: DistanceX(g21,g21) = 1.5
    c: DistanceX(g33,g33) = 1.5
    c: DistanceX(g31,g31) = 1.3
    c: DistanceX(g0) = 66
    c: DistanceY(g0) = 76
    c: Coincident(g19,g34)
    c: Horizontal(g34)
    c: Coincident(g34,g35)
    c: Vertical(g35)
    c: Coincident(g35,g36)
    c: Horizontal(g36)
    c: Coincident(g36,g37)
    c: Vertical(g37)
    c: Coincident(g37,g38)
    c: Horizontal(g38)
    c: Coincident(g38,g39)
    c: Vertical(g39)
    c: Coincident(g39,g40)
    c: Horizontal(g40)
    c: Coincident(g40,g41)
    c: Vertical(g41)
    c: Coincident(g41,g42)
    c: Horizontal(g42)
    c: Coincident(g42,g43)
    c: Vertical(g43)
    c: Coincident(g43,g44)
    c: Horizontal(g44)
    c: Coincident(g44,g45)
    c: Vertical(g45)
    c: Coincident(g45,g46)
    c: Coincident(g46,g11)
    c: Horizontal(g46)
    c: DistanceY(g19,g19) = 3
    c: DistanceY(g11,g11) = 3
    c: DistanceX(g34,g34) = 1.5
    c: DistanceX(g46,g46) = 1.5
    c: DistanceY(g35,g35) = 4
    c: DistanceY(g45,g45) = 4
    c: DistanceY(g37,g37) = 2.5
    c: DistanceY(g43,g43) = 2.5
    c: DistanceY(g39,g39) = 1.5
    c: DistanceY(g41,g41) = 1.5
    c: DistanceX(g40,g40) = 3
    c: DistanceX(g36,g36) = 1.3
    c: DistanceX(g44,g44) = 1.3
    c: DistanceX(g38,g38) = 1.3
    c: DistanceY(g1,g1) = 17
FEATURE [Sketcher::SketchObject] Sketch094
  MapMode = 5
  Support = -> [XY_Plane]
  sketch-geometry (35):
    g0: LineSegment [constr] StartX=144 StartY=158 StartZ=0 EndX=162 EndY=158 EndZ=0
    g1: LineSegment StartX=144 StartY=143 StartZ=0 EndX=148 EndY=143 EndZ=0
    g2: LineSegment StartX=162 StartY=143 StartZ=0 EndX=158 EndY=143 EndZ=0
    g3: LineSegment StartX=148 StartY=143 StartZ=0 EndX=148 EndY=146 EndZ=0
    g4: LineSegment StartX=148 StartY=146 StartZ=0 EndX=151.5 EndY=146 EndZ=0
    g5: LineSegment StartX=151.5 StartY=146 StartZ=0 EndX=151.5 EndY=150 EndZ=0
    g6: LineSegment StartX=151.5 StartY=150 StartZ=0 EndX=150.2 EndY=150 EndZ=0
    g7: LineSegment StartX=150.2 StartY=150 StartZ=0 EndX=150.2 EndY=152.5 EndZ=0
    g8: LineSegment StartX=150.2 StartY=152.5 StartZ=0 EndX=151.5 EndY=152.5 EndZ=0
    g9: LineSegment StartX=151.5 StartY=152.5 StartZ=0 EndX=151.5 EndY=154 EndZ=0
    g10: LineSegment StartX=151.5 StartY=154 StartZ=0 EndX=154.5 EndY=154 EndZ=0
    g11: LineSegment StartX=154.5 StartY=154 StartZ=0 EndX=154.5 EndY=152.5 EndZ=0
    g12: LineSegment StartX=154.5 StartY=152.5 StartZ=0 EndX=155.8 EndY=152.5 EndZ=0
    g13: LineSegment StartX=155.8 StartY=152.5 StartZ=0 EndX=155.8 EndY=150 EndZ=0
    g14: LineSegment StartX=155.8 StartY=150 StartZ=0 EndX=154.5 EndY=150 EndZ=0
    g15: LineSegment StartX=154.5 StartY=150 StartZ=0 EndX=154.5 EndY=146 EndZ=0
    g16: LineSegment StartX=154.5 StartY=146 StartZ=0 EndX=158 EndY=146 EndZ=0
    g17: LineSegment StartX=158 StartY=146 StartZ=0 EndX=158 EndY=143 EndZ=0
    g18: LineSegment StartX=162 StartY=188 StartZ=0 EndX=162 EndY=178.5 EndZ=0
    g19: ArcOfCircle CenterX=146 CenterY=188 CenterZ=0 NormalX=0 NormalY=0 NormalZ=1 AngleXU=0 Radius=2 StartAngle=1.5708 EndAngle=3.14159
    g20: LineSegment StartX=146 StartY=190 StartZ=0 EndX=160 EndY=190 EndZ=0
    g21: ArcOfCircle CenterX=160 CenterY=188 CenterZ=0 NormalX=0 NormalY=0 NormalZ=1 AngleXU=0 Radius=2 StartAngle=0 EndAngle=1.5708
    g22: LineSegment StartX=146.95 StartY=185 StartZ=0 EndX=159.05 EndY=185 EndZ=0
    g23: LineSegment StartX=159.05 StartY=185 StartZ=0 EndX=159.05 EndY=162.5 EndZ=0
    g24: LineSegment StartX=159.05 StartY=162.5 StartZ=0 EndX=146.95 EndY=162.5 EndZ=0
    g25: LineSegment StartX=146.95 StartY=162.5 StartZ=0 EndX=146.95 EndY=185 EndZ=0
    g26: Circle CenterX=153 CenterY=187.5 CenterZ=0 NormalX=0 NormalY=0 NormalZ=1 AngleXU=0 Radius=1
    g27: Circle CenterX=153 CenterY=160 CenterZ=0 NormalX=0 NormalY=0 NormalZ=1 AngleXU=0 Radius=1
    g28: LineSegment StartX=162 StartY=178 StartZ=0 EndX=162 EndY=143 EndZ=0
    g29: LineSegment StartX=144 StartY=188 StartZ=0 EndX=144 EndY=178.5 EndZ=0
    g30: LineSegment StartX=144 StartY=178 StartZ=0 EndX=144 EndY=168 EndZ=0
    g31: LineSegment StartX=144 StartY=168 StartZ=0 EndX=141 EndY=168 EndZ=0
    g32: LineSegment StartX=141 StartY=168 StartZ=0 EndX=141 EndY=163 EndZ=0
    g33: LineSegment StartX=141 StartY=163 StartZ=0 EndX=144 EndY=163 EndZ=0
    g34: LineSegment StartX=144 StartY=163 StartZ=0 EndX=144 EndY=143 EndZ=0
  constraints (109):
    c: Horizontal(g0)
    c: DistanceY(g1,g0) = 15
    c: DistanceX(g0,g0) = 18
    c: Horizontal(g2,g1)
    c: Horizontal(g1)
    c: Horizontal(g2)
    c: Coincident(g1,g3)
    c: Vertical(g3)
    c: Coincident(g3,g4)
    c: Horizontal(g4)
    c: Coincident(g4,g5)
    c: Vertical(g5)
    c: Coincident(g5,g6)
    c: Horizontal(g6)
    c: Coincident(g6,g7)
    c: Vertical(g7)
    c: Coincident(g7,g8)
    c: Horizontal(g8)
    c: Coincident(g8,g9)
    c: Coincident(g9,g10)
    c: Horizontal(g10)
    c: Coincident(g10,g11)
    c: Vertical(g11)
    c: Coincident(g11,g12)
    c: Horizontal(g12)
    c: Coincident(g12,g13)
    c: Vertical(g13)
    c: Coincident(g13,g14)
    c: Horizontal(g14)
    c: Coincident(g14,g15)
    c: Vertical(g15)
    c: Coincident(g15,g16)
    c: Horizontal(g16)
    c: Coincident(g16,g17)
    c: Coincident(g17,g2)
    c: Vertical(g17)
    c: Vertical(g9)
    c: DistanceX(g1,g1) = 4
    c: DistanceX(g2,g2) = 4
    c: Horizontal(g3,g16)
    c: DistanceY(g3,g3) = 3
    c: Horizontal(g5,g14)
    c: Horizontal(g8,g11)
    c: DistanceX(g4,g4) = 3.5
    c: DistanceX(g16,g16) = 3.5
    c: DistanceY(g5,g5) = 4
    c: Vertical(g8,g5)
    c: Vertical(g11,g14)
    c: DistanceY(g7,g7) = 2.5
    c: DistanceX(g4,g15) = 3
    c: DistanceX(g6,g6) = 1.3
    c: DistanceX(g14,g14) = 1.3
    c: DistanceY(g9,g9) = 1.5
    c: Vertical(g18)
    c: Vertical(g0,g18)
    c: Vertical(g18,g28)
    c: DistanceY(g28,g18) = 0.5
    c: Horizontal(g20)
    c: Tangent(g20,g21) = 1.5708
    c: Tangent(g19,g20) = 1.5708
    c: Radius(g19) = 2
    c: Radius(g21) = 2
    c: Tangent(g21,g18) = 1.5708
    c: Coincident(g22,g23)
    c: Coincident(g23,g24)
    c: Coincident(g24,g25)
    c: Coincident(g25,g22)
    c: Horizontal(g22)
    c: Horizontal(g24)
    c: Vertical(g23)
    c: Vertical(g25)
    c: DistanceX(g24,g24) = 12.1
    c: DistanceY(g25,g25) = 22.5
    c: DistanceY(g3,g24) = 16.5
    c: DistanceX(g1,g24) = 2.95
    c: DistanceY(g22,g19) = 5
    c: Radius(g27) = 1
    c: Radius(g26) = 1
    c: DistanceY(g22,g26) = 2.5
    c: DistanceY(g27,g24) = 2.5
    c: DistanceX(g24,g27) = 6.05
    c: DistanceX(g22,g26) = 6.05
    c: DistanceY(g9,g27) = 6
    c: DistanceY(g1,g19) = 47
    c: Vertical(g30,g29)
    c: DistanceY(g30,g29) = 0.5
    c: Horizontal(g30,g28)
    c: DistanceX(g10,g10) = 3
    c: Vertical(g28)
    c: Vertical(g29)
    c: Tangent(g19,g29) = -1.5708
    c: Vertical(g30)
    c: Coincident(g30,g31)
    c: Horizontal(g31)
    c: Coincident(g31,g32)
    c: Vertical(g32)
    c: Coincident(g32,g33)
    c: Horizontal(g33)
    c: Coincident(g33,g34)
    c: Coincident(g34,g1)
    c: Vertical(g34)
    c: DistanceY(g34,g34) = 20
    c: DistanceX(g33,g33) = 3
    c: DistanceY(g32,g32) = 5
    c: DistanceX(g31,g31) = 3
    c: Coincident(g2,g28)
    c: DistanceY(g30,g30) = 10
    c: DistanceX(g1) = 144
    c: DistanceY(g1) = 143
FEATURE [Sketcher::SketchObject] Sketch095
  MapMode = 5
  Support = -> [XY_Plane]
  sketch-geometry (30):
    g0: LineSegment [constr] StartX=144 StartY=206 StartZ=0 EndX=162 EndY=206 EndZ=0
    g1: LineSegment StartX=144 StartY=191 StartZ=0 EndX=148 EndY=191 EndZ=0
    g2: LineSegment StartX=162 StartY=191 StartZ=0 EndX=158 EndY=191 EndZ=0
    g3: LineSegment StartX=148 StartY=191 StartZ=0 EndX=148 EndY=194 EndZ=0
    g4: LineSegment StartX=148 StartY=194 StartZ=0 EndX=151.5 EndY=194 EndZ=0
    g5: LineSegment StartX=151.5 StartY=194 StartZ=0 EndX=151.5 EndY=198 EndZ=0
    g6: LineSegment StartX=151.5 StartY=198 StartZ=0 EndX=150.2 EndY=198 EndZ=0
    g7: LineSegment StartX=150.2 StartY=198 StartZ=0 EndX=150.2 EndY=200.5 EndZ=0
    g8: LineSegment StartX=150.2 StartY=200.5 StartZ=0 EndX=151.5 EndY=200.5 EndZ=0
    g9: LineSegment StartX=151.5 StartY=200.5 StartZ=0 EndX=151.5 EndY=202 EndZ=0
    g10: LineSegment StartX=151.5 StartY=202 StartZ=0 EndX=154.5 EndY=202 EndZ=0
    g11: LineSegment StartX=154.5 StartY=202 StartZ=0 EndX=154.5 EndY=200.5 EndZ=0
    g12: LineSegment StartX=154.5 StartY=200.5 StartZ=0 EndX=155.8 EndY=200.5 EndZ=0
    g13: LineSegment StartX=155.8 StartY=200.5 StartZ=0 EndX=155.8 EndY=198 EndZ=0
    g14: LineSegment StartX=155.8 StartY=198 StartZ=0 EndX=154.5 EndY=198 EndZ=0
    g15: LineSegment StartX=154.5 StartY=198 StartZ=0 EndX=154.5 EndY=194 EndZ=0
    g16: LineSegment StartX=154.5 StartY=194 StartZ=0 EndX=158 EndY=194 EndZ=0
    g17: LineSegment StartX=158 StartY=194 StartZ=0 EndX=158 EndY=191 EndZ=0
    g18: LineSegment StartX=162 StartY=231 StartZ=0 EndX=162 EndY=226.5 EndZ=0
    g19: ArcOfCircle CenterX=146 CenterY=231 CenterZ=0 NormalX=0 NormalY=0 NormalZ=1 AngleXU=0 Radius=2 StartAngle=1.5708 EndAngle=3.14159
    g20: LineSegment StartX=146 StartY=233 StartZ=0 EndX=160 EndY=233 EndZ=0
    g21: ArcOfCircle CenterX=160 CenterY=231 CenterZ=0 NormalX=0 NormalY=0 NormalZ=1 AngleXU=0 Radius=2 StartAngle=0 EndAngle=1.5708
    g22: Circle CenterX=153 CenterY=227 CenterZ=0 NormalX=0 NormalY=0 NormalZ=1 AngleXU=0 Radius=1.5
    g23: LineSegment StartX=162 StartY=226 StartZ=0 EndX=162 EndY=191 EndZ=0
    g24: LineSegment StartX=144 StartY=231 StartZ=0 EndX=144 EndY=226.5 EndZ=0
    g25: LineSegment StartX=144 StartY=226 StartZ=0 EndX=144 EndY=216 EndZ=0
    g26: LineSegment StartX=144 StartY=216 StartZ=0 EndX=141 EndY=216 EndZ=0
    g27: LineSegment StartX=141 StartY=216 StartZ=0 EndX=141 EndY=211 EndZ=0
    g28: LineSegment StartX=141 StartY=211 StartZ=0 EndX=144 EndY=211 EndZ=0
    g29: LineSegment StartX=144 StartY=211 StartZ=0 EndX=144 EndY=191 EndZ=0
  constraints (95):
    c: Horizontal(g0)
    c: DistanceY(g1,g0) = 15
    c: DistanceX(g0,g0) = 18
    c: Horizontal(g2,g1)
    c: Horizontal(g1)
    c: Horizontal(g2)
    c: Coincident(g1,g3)
    c: Vertical(g3)
    c: Coincident(g3,g4)
    c: Horizontal(g4)
    c: Coincident(g4,g5)
    c: Vertical(g5)
    c: Coincident(g5,g6)
    c: Horizontal(g6)
    c: Coincident(g6,g7)
    c: Vertical(g7)
    c: Coincident(g7,g8)
    c: Horizontal(g8)
    c: Coincident(g8,g9)
    c: Coincident(g9,g10)
    c: Horizontal(g10)
    c: Coincident(g10,g11)
    c: Vertical(g11)
    c: Coincident(g11,g12)
    c: Horizontal(g12)
    c: Coincident(g12,g13)
    c: Vertical(g13)
    c: Coincident(g13,g14)
    c: Horizontal(g14)
    c: Coincident(g14,g15)
    c: Vertical(g15)
    c: Coincident(g15,g16)
    c: Horizontal(g16)
    c: Coincident(g16,g17)
    c: Coincident(g17,g2)
    c: Vertical(g17)
    c: Vertical(g9)
    c: DistanceX(g1,g1) = 4
    c: DistanceX(g2,g2) = 4
    c: Horizontal(g3,g16)
    c: DistanceY(g3,g3) = 3
    c: Horizontal(g5,g14)
    c: Horizontal(g8,g11)
    c: DistanceX(g4,g4) = 3.5
    c: DistanceX(g16,g16) = 3.5
    c: DistanceY(g5,g5) = 4
    c: Vertical(g8,g5)
    c: Vertical(g11,g14)
    c: DistanceY(g7,g7) = 2.5
    c: DistanceX(g4,g15) = 3
    c: DistanceX(g6,g6) = 1.3
    c: DistanceX(g14,g14) = 1.3
    c: DistanceY(g9,g9) = 1.5
    c: Vertical(g18)
    c: Vertical(g0,g18)
    c: Vertical(g18,g23)
    c: DistanceY(g23,g18) = 0.5
    c: Horizontal(g20)
    c: Tangent(g20,g21) = 1.5708
    c: Tangent(g19,g20) = 1.5708
    c: Radius(g19) = 2
    c: Radius(g21) = 2
    c: Tangent(g21,g18) = 1.5708
    c: Radius(g22) = 1.5
    c: DistanceY(g22,g19) = 6
    c: DistanceX(g1,g22) = 9
    c: DistanceY(g1,g19) = 42
    c: Distance(g22,g19) = 9.21954
    c: Distance(g19,g22) = 8.06226
    c: Vertical(g25,g24)
    c: DistanceY(g25,g24) = 0.5
    c: Horizontal(g25,g23)
    c: DistanceX(g10,g10) = 3
    c: Vertical(g23)
    c: Vertical(g24)
    c: Tangent(g19,g24) = -1.5708
    c: Vertical(g25)
    c: Coincident(g25,g26)
    c: Horizontal(g26)
    c: Coincident(g26,g27)
    c: Vertical(g27)
    c: Coincident(g27,g28)
    c: Horizontal(g28)
    c: Coincident(g28,g29)
    c: Coincident(g29,g1)
    c: Vertical(g29)
    c: DistanceY(g29,g29) = 20
    c: DistanceX(g28,g28) = 3
    c: DistanceY(g27,g27) = 5
    c: DistanceX(g26,g26) = 3
    c: DistanceY(g1,g22) = 36
    c: Coincident(g2,g23)
    c: DistanceY(g25,g25) = 10
    c: DistanceX(g1) = 144
    c: DistanceY(g1) = 191
FEATURE [Sketcher::SketchObject] Sketch099
  MapMode = 5
  Support = -> [XY_Plane]
  sketch-geometry (29):
    g0: LineSegment StartX=41 StartY=170 StartZ=0 EndX=70 EndY=170 EndZ=0
    g1: LineSegment StartX=72 StartY=148 StartZ=0 EndX=68 EndY=148 EndZ=0
    g2: LineSegment StartX=68 StartY=148 StartZ=0 EndX=68 EndY=143 EndZ=0
    g3: LineSegment StartX=68 StartY=143 StartZ=0 EndX=63 EndY=143 EndZ=0
    g4: LineSegment StartX=63 StartY=143 StartZ=0 EndX=63 EndY=148 EndZ=0
    g5: LineSegment StartX=57 StartY=148 StartZ=0 EndX=57 EndY=152 EndZ=0
    g6: LineSegment StartX=57 StartY=152 StartZ=0 EndX=58.3 EndY=152 EndZ=0
    g7: LineSegment StartX=58.3 StartY=152 StartZ=0 EndX=58.3 EndY=154.5 EndZ=0
    g8: LineSegment StartX=58.3 StartY=154.5 StartZ=0 EndX=57 EndY=154.5 EndZ=0
    g9: LineSegment StartX=57 StartY=154.5 StartZ=0 EndX=57 EndY=156 EndZ=0
    g10: LineSegment StartX=57 StartY=156 StartZ=0 EndX=54 EndY=156 EndZ=0
    g11: LineSegment StartX=54 StartY=156 StartZ=0 EndX=54 EndY=154.5 EndZ=0
    g12: LineSegment StartX=54 StartY=154.5 StartZ=0 EndX=52.7 EndY=154.5 EndZ=0
    g13: LineSegment StartX=52.7 StartY=154.5 StartZ=0 EndX=52.7 EndY=152 EndZ=0
    g14: LineSegment StartX=52.7 StartY=152 StartZ=0 EndX=54 EndY=152 EndZ=0
    g15: LineSegment StartX=54 StartY=152 StartZ=0 EndX=54 EndY=148 EndZ=0
    g16: LineSegment StartX=48 StartY=148 StartZ=0 EndX=48 EndY=143 EndZ=0
    g17: LineSegment StartX=48 StartY=143 StartZ=0 EndX=43 EndY=143 EndZ=0
    g18: LineSegment StartX=43 StartY=143 StartZ=0 EndX=43 EndY=148 EndZ=0
    g19: LineSegment StartX=43 StartY=148 StartZ=0 EndX=39 EndY=148 EndZ=0
    g20: ArcOfCircle CenterX=41 CenterY=168 CenterZ=0 NormalX=0 NormalY=0 NormalZ=1 AngleXU=0 Radius=2 StartAngle=1.5708 EndAngle=3.14159
    g21: ArcOfCircle CenterX=70 CenterY=168 CenterZ=0 NormalX=0 NormalY=0 NormalZ=1 AngleXU=0 Radius=2 StartAngle=0 EndAngle=1.5708
    g22: Circle CenterX=48 CenterY=164 CenterZ=0 NormalX=0 NormalY=0 NormalZ=1 AngleXU=0 Radius=1.5
    g23: LineSegment StartX=39 StartY=168 StartZ=0 EndX=39 EndY=158.25 EndZ=0
    g24: LineSegment StartX=39 StartY=148 StartZ=0 EndX=39 EndY=157.75 EndZ=0
    g25: LineSegment StartX=72 StartY=168 StartZ=0 EndX=72 EndY=158.25 EndZ=0
    g26: LineSegment StartX=72 StartY=148 StartZ=0 EndX=72 EndY=157.75 EndZ=0
    g27: LineSegment StartX=57 StartY=148 StartZ=0 EndX=63 EndY=148 EndZ=0
    g28: LineSegment StartX=48 StartY=148 StartZ=0 EndX=54 EndY=148 EndZ=0
  constraints (88):
    c: Horizontal(g0)
    c: Horizontal(g1)
    c: Coincident(g1,g2)
    c: Vertical(g2)
    c: Coincident(g2,g3)
    c: Horizontal(g3)
    c: Coincident(g3,g4)
    c: Vertical(g4)
    c: Vertical(g5)
    c: Coincident(g5,g6)
    c: Horizontal(g6)
    c: Coincident(g6,g7)
    c: Vertical(g7)
    c: Coincident(g7,g8)
    c: Horizontal(g8)
    c: Coincident(g8,g9)
    c: Vertical(g9)
    c: Coincident(g9,g10)
    c: Coincident(g10,g11)
    c: Vertical(g11)
    c: Coincident(g11,g12)
    c: Horizontal(g12)
    c: Coincident(g12,g13)
    c: Vertical(g13)
    c: Coincident(g13,g14)
    c: Horizontal(g14)
    c: Coincident(g14,g15)
    c: Vertical(g15)
    c: Vertical(g16)
    c: Coincident(g16,g17)
    c: Horizontal(g17)
    c: Vertical(g18)
    c: Coincident(g18,g19)
    c: Horizontal(g19)
    c: DistanceX(g10,g10) = 3
    c: DistanceY(g18,g18) = 5
    c: DistanceY(g2,g2) = 5
    c: DistanceY(g16,g16) = 5
    c: DistanceY(g4,g4) = 5
    c: DistanceX(g17,g17) = 5
    c: DistanceX(g19,g19) = 4
    c: DistanceX(g3,g3) = 5
    c: DistanceX(g1,g1) = 4
    c: Horizontal(g17,g3)
    c: DistanceY(g11,g11) = 1.5
    c: DistanceX(g8,g8) = 1.3
    c: DistanceX(g12,g12) = 1.3
    c: DistanceX(g14,g14) = 1.3
    c: DistanceX(g6,g6) = 1.3
    c: DistanceY(g13,g13) = 2.5
    c: DistanceY(g7,g7) = 2.5
    c: DistanceY(g15,g15) = 4
    c: DistanceX(g16,g15) = 6
    c: DistanceX(g5,g4) = 6
    c: Tangent(g0,g20) = 1.5708
    c: Radius(g20) = 2
    c: Radius(g21) = 2
    c: Radius(g22) = 1.5
    c: Vertical(g23)
    c: Coincident(g24,g19)
    c: Vertical(g24)
    c: Tangent(g23,g20) = -1.5708
    c: Vertical(g23,g24)
    c: DistanceY(g24,g23) = 0.5
    c: Equal(g23,g24)
    c: Vertical(g25)
    c: Coincident(g26,g1)
    c: Vertical(g26)
    c: Vertical(g25,g26)
    c: DistanceY(g26,g25) = 0.5
    c: Equal(g25,g26)
    c: Tangent(g25,g21) = 1.5708
    c: Tangent(g0,g21) = 1.5708
    c: Coincident(g5,g27)
    c: Horizontal(g27)
    c: DistanceY(g5,g5) = 4
    c: Coincident(g28,g15)
    c: Horizontal(g28)
    c: Coincident(g27,g4)
    c: DistanceY(g9,g9) = 1.5
    c: Coincident(g16,g28)
    c: DistanceX(g20,g21) = 33
    c: DistanceY(g1,g22) = 16
    c: DistanceX(g20,g22) = 9
    c: DistanceY(g22,g0) = 6
    c: Coincident(g17,g18)
    c: DistanceX(g17) = 43
    c: DistanceY(g17) = 143
FEATURE [Sketcher::SketchObject] Sketch100
  MapMode = 5
  Support = -> [XY_Plane]
  sketch-geometry (29):
    g0: LineSegment StartX=109 StartY=209 StartZ=0 EndX=138 EndY=209 EndZ=0
    g1: LineSegment StartX=140 StartY=187 StartZ=0 EndX=136 EndY=187 EndZ=0
    g2: LineSegment StartX=136 StartY=187 StartZ=0 EndX=136 EndY=182 EndZ=0
    g3: LineSegment StartX=136 StartY=182 StartZ=0 EndX=131 EndY=182 EndZ=0
    g4: LineSegment StartX=131 StartY=182 StartZ=0 EndX=131 EndY=187 EndZ=0
    g5: LineSegment StartX=125 StartY=187 StartZ=0 EndX=125 EndY=191 EndZ=0
    g6: LineSegment StartX=125 StartY=191 StartZ=0 EndX=126.3 EndY=191 EndZ=0
    g7: LineSegment StartX=126.3 StartY=191 StartZ=0 EndX=126.3 EndY=193.5 EndZ=0
    g8: LineSegment StartX=126.3 StartY=193.5 StartZ=0 EndX=125 EndY=193.5 EndZ=0
    g9: LineSegment StartX=125 StartY=193.5 StartZ=0 EndX=125 EndY=195 EndZ=0
    g10: LineSegment StartX=125 StartY=195 StartZ=0 EndX=122 EndY=195 EndZ=0
    g11: LineSegment StartX=122 StartY=195 StartZ=0 EndX=122 EndY=193.5 EndZ=0
    g12: LineSegment StartX=122 StartY=193.5 StartZ=0 EndX=120.7 EndY=193.5 EndZ=0
    g13: LineSegment StartX=120.7 StartY=193.5 StartZ=0 EndX=120.7 EndY=191 EndZ=0
    g14: LineSegment StartX=120.7 StartY=191 StartZ=0 EndX=122 EndY=191 EndZ=0
    g15: LineSegment StartX=122 StartY=191 StartZ=0 EndX=122 EndY=187 EndZ=0
    g16: LineSegment StartX=116 StartY=187 StartZ=0 EndX=116 EndY=182 EndZ=0
    g17: LineSegment StartX=116 StartY=182 StartZ=0 EndX=111 EndY=182 EndZ=0
    g18: LineSegment StartX=111 StartY=182 StartZ=0 EndX=111 EndY=187 EndZ=0
    g19: LineSegment StartX=111 StartY=187 StartZ=0 EndX=107 EndY=187 EndZ=0
    g20: ArcOfCircle CenterX=109 CenterY=207 CenterZ=0 NormalX=0 NormalY=0 NormalZ=1 AngleXU=0 Radius=2 StartAngle=1.5708 EndAngle=3.14159
    g21: ArcOfCircle CenterX=138 CenterY=207 CenterZ=0 NormalX=0 NormalY=0 NormalZ=1 AngleXU=0 Radius=2 StartAngle=0 EndAngle=1.5708
    g22: Circle CenterX=131 CenterY=203 CenterZ=0 NormalX=0 NormalY=0 NormalZ=1 AngleXU=0 Radius=3.4
    g23: LineSegment StartX=107 StartY=207 StartZ=0 EndX=107 EndY=197.25 EndZ=0
    g24: LineSegment StartX=107 StartY=187 StartZ=0 EndX=107 EndY=196.75 EndZ=0
    g25: LineSegment StartX=140 StartY=207 StartZ=0 EndX=140 EndY=197.25 EndZ=0
    g26: LineSegment StartX=140 StartY=187 StartZ=0 EndX=140 EndY=196.75 EndZ=0
    g27: LineSegment StartX=125 StartY=187 StartZ=0 EndX=131 EndY=187 EndZ=0
    g28: LineSegment StartX=116 StartY=187 StartZ=0 EndX=122 EndY=187 EndZ=0
  constraints (88):
    c: Horizontal(g0)
    c: Horizontal(g1)
    c: Coincident(g1,g2)
    c: Vertical(g2)
    c: Coincident(g2,g3)
    c: Horizontal(g3)
    c: Coincident(g3,g4)
    c: Vertical(g4)
    c: Vertical(g5)
    c: Coincident(g5,g6)
    c: Horizontal(g6)
    c: Coincident(g6,g7)
    c: Vertical(g7)
    c: Coincident(g7,g8)
    c: Horizontal(g8)
    c: Coincident(g8,g9)
    c: Vertical(g9)
    c: Coincident(g9,g10)
    c: Coincident(g10,g11)
    c: Vertical(g11)
    c: Coincident(g11,g12)
    c: Horizontal(g12)
    c: Coincident(g12,g13)
    c: Vertical(g13)
    c: Coincident(g13,g14)
    c: Horizontal(g14)
    c: Coincident(g14,g15)
    c: Vertical(g15)
    c: Vertical(g16)
    c: Coincident(g16,g17)
    c: Horizontal(g17)
    c: Coincident(g17,g18)
    c: Vertical(g18)
    c: Coincident(g18,g19)
    c: Horizontal(g19)
    c: DistanceX(g10,g10) = 3
    c: DistanceY(g18,g18) = 5
    c: DistanceY(g2,g2) = 5
    c: DistanceY(g16,g16) = 5
    c: DistanceY(g4,g4) = 5
    c: DistanceX(g17,g17) = 5
    c: DistanceX(g19,g19) = 4
    c: DistanceX(g3,g3) = 5
    c: DistanceX(g1,g1) = 4
    c: Horizontal(g17,g3)
    c: DistanceY(g11,g11) = 1.5
    c: DistanceX(g8,g8) = 1.3
    c: DistanceX(g12,g12) = 1.3
    c: DistanceX(g14,g14) = 1.3
    c: DistanceX(g6,g6) = 1.3
    c: DistanceY(g13,g13) = 2.5
    c: DistanceY(g7,g7) = 2.5
    c: DistanceY(g15,g15) = 4
    c: DistanceX(g16,g15) = 6
    c: DistanceX(g5,g4) = 6
    c: Tangent(g0,g20) = 1.5708
    c: Radius(g20) = 2
    c: Radius(g21) = 2
    c: Radius(g22) = 3.4
    c: DistanceY(g22,g0) = 6
    c: Vertical(g23)
    c: Coincident(g24,g19)
    c: Vertical(g24)
    c: Tangent(g23,g20) = -1.5708
    c: Vertical(g23,g24)
    c: DistanceY(g24,g23) = 0.5
    c: Equal(g23,g24)
    c: Vertical(g25)
    c: Coincident(g26,g1)
    c: Vertical(g26)
    c: Vertical(g25,g26)
    c: DistanceY(g26,g25) = 0.5
    c: Equal(g25,g26)
    c: Tangent(g25,g21) = 1.5708
    c: DistanceX(g22,g21) = 9
    c: Tangent(g0,g21) = 1.5708
    c: Coincident(g5,g27)
    c: Horizontal(g27)
    c: DistanceY(g5,g5) = 4
    c: Coincident(g28,g15)
    c: Horizontal(g28)
    c: Coincident(g27,g4)
    c: DistanceY(g9,g9) = 1.5
    c: Coincident(g16,g28)
    c: DistanceX(g20,g21) = 33
    c: DistanceY(g1,g22) = 16
    c: DistanceX(g17) = 111
    c: DistanceY(g17) = 182
FEATURE [Sketcher::SketchObject] Sketch101
  MapMode = 5
  Support = -> [XY_Plane]
  sketch-geometry (29):
    g0: LineSegment StartX=75 StartY=209 StartZ=0 EndX=104 EndY=209 EndZ=0
    g1: LineSegment StartX=106 StartY=187 StartZ=0 EndX=102 EndY=187 EndZ=0
    g2: LineSegment StartX=102 StartY=187 StartZ=0 EndX=102 EndY=182 EndZ=0
    g3: LineSegment StartX=102 StartY=182 StartZ=0 EndX=97 EndY=182 EndZ=0
    g4: LineSegment StartX=97 StartY=182 StartZ=0 EndX=97 EndY=187 EndZ=0
    g5: LineSegment StartX=91 StartY=187 StartZ=0 EndX=91 EndY=191 EndZ=0
    g6: LineSegment StartX=91 StartY=191 StartZ=0 EndX=92.3 EndY=191 EndZ=0
    g7: LineSegment StartX=92.3 StartY=191 StartZ=0 EndX=92.3 EndY=193.5 EndZ=0
    g8: LineSegment StartX=92.3 StartY=193.5 StartZ=0 EndX=91 EndY=193.5 EndZ=0
    g9: LineSegment StartX=91 StartY=193.5 StartZ=0 EndX=91 EndY=195 EndZ=0
    g10: LineSegment StartX=91 StartY=195 StartZ=0 EndX=88 EndY=195 EndZ=0
    g11: LineSegment StartX=88 StartY=195 StartZ=0 EndX=88 EndY=193.5 EndZ=0
    g12: LineSegment StartX=88 StartY=193.5 StartZ=0 EndX=86.7 EndY=193.5 EndZ=0
    g13: LineSegment StartX=86.7 StartY=193.5 StartZ=0 EndX=86.7 EndY=191 EndZ=0
    g14: LineSegment StartX=86.7 StartY=191 StartZ=0 EndX=88 EndY=191 EndZ=0
    g15: LineSegment StartX=88 StartY=191 StartZ=0 EndX=88 EndY=187 EndZ=0
    g16: LineSegment StartX=82 StartY=187 StartZ=0 EndX=82 EndY=182 EndZ=0
    g17: LineSegment StartX=82 StartY=182 StartZ=0 EndX=77 EndY=182 EndZ=0
    g18: LineSegment StartX=77 StartY=182 StartZ=0 EndX=77 EndY=187 EndZ=0
    g19: LineSegment StartX=77 StartY=187 StartZ=0 EndX=73 EndY=187 EndZ=0
    g20: ArcOfCircle CenterX=75 CenterY=207 CenterZ=0 NormalX=0 NormalY=0 NormalZ=1 AngleXU=0 Radius=2 StartAngle=1.5708 EndAngle=3.14159
    g21: ArcOfCircle CenterX=104 CenterY=207 CenterZ=0 NormalX=0 NormalY=0 NormalZ=1 AngleXU=0 Radius=2 StartAngle=0 EndAngle=1.5708
    g22: Circle CenterX=82 CenterY=203 CenterZ=0 NormalX=0 NormalY=0 NormalZ=1 AngleXU=0 Radius=3.4
    g23: LineSegment StartX=73 StartY=207 StartZ=0 EndX=73 EndY=197.25 EndZ=0
    g24: LineSegment StartX=73 StartY=187 StartZ=0 EndX=73 EndY=196.75 EndZ=0
    g25: LineSegment StartX=106 StartY=207 StartZ=0 EndX=106 EndY=197.25 EndZ=0
    g26: LineSegment StartX=106 StartY=187 StartZ=0 EndX=106 EndY=196.75 EndZ=0
    g27: LineSegment StartX=91 StartY=187 StartZ=0 EndX=97 EndY=187 EndZ=0
    g28: LineSegment StartX=82 StartY=187 StartZ=0 EndX=88 EndY=187 EndZ=0
  constraints (89):
    c: Horizontal(g0)
    c: Horizontal(g1)
    c: Coincident(g1,g2)
    c: Vertical(g2)
    c: Coincident(g2,g3)
    c: Horizontal(g3)
    c: Coincident(g3,g4)
    c: Vertical(g4)
    c: Vertical(g5)
    c: Coincident(g5,g6)
    c: Horizontal(g6)
    c: Coincident(g6,g7)
    c: Vertical(g7)
    c: Coincident(g7,g8)
    c: Horizontal(g8)
    c: Coincident(g8,g9)
    c: Vertical(g9)
    c: Coincident(g9,g10)
    c: Coincident(g10,g11)
    c: Vertical(g11)
    c: Coincident(g11,g12)
    c: Horizontal(g12)
    c: Coincident(g12,g13)
    c: Vertical(g13)
    c: Coincident(g13,g14)
    c: Horizontal(g14)
    c: Coincident(g14,g15)
    c: Vertical(g15)
    c: Vertical(g16)
    c: Coincident(g16,g17)
    c: Horizontal(g17)
    c: Vertical(g18)
    c: Coincident(g18,g19)
    c: Horizontal(g19)
    c: DistanceX(g10,g10) = 3
    c: DistanceY(g18,g18) = 5
    c: DistanceY(g2,g2) = 5
    c: DistanceY(g16,g16) = 5
    c: DistanceY(g4,g4) = 5
    c: DistanceX(g17,g17) = 5
    c: DistanceX(g19,g19) = 4
    c: DistanceX(g3,g3) = 5
    c: DistanceX(g1,g1) = 4
    c: Horizontal(g17,g3)
    c: DistanceY(g11,g11) = 1.5
    c: DistanceX(g8,g8) = 1.3
    c: DistanceX(g12,g12) = 1.3
    c: DistanceX(g14,g14) = 1.3
    c: DistanceX(g6,g6) = 1.3
    c: DistanceY(g13,g13) = 2.5
    c: DistanceY(g7,g7) = 2.5
    c: DistanceY(g15,g15) = 4
    c: DistanceX(g16,g15) = 6
    c: DistanceX(g5,g4) = 6
    c: Tangent(g0,g20) = 1.5708
    c: Radius(g20) = 2
    c: Radius(g21) = 2
    c: Radius(g22) = 3.4
    c: Vertical(g23)
    c: Coincident(g24,g19)
    c: Vertical(g24)
    c: Tangent(g23,g20) = -1.5708
    c: Vertical(g23,g24)
    c: DistanceY(g24,g23) = 0.5
    c: Equal(g23,g24)
    c: Vertical(g25)
    c: Coincident(g26,g1)
    c: Vertical(g26)
    c: Vertical(g25,g26)
    c: DistanceY(g26,g25) = 0.5
    c: Equal(g25,g26)
    c: Tangent(g25,g21) = 1.5708
    c: Tangent(g0,g21) = 1.5708
    c: Coincident(g5,g27)
    c: Horizontal(g27)
    c: DistanceY(g5,g5) = 4
    c: Coincident(g28,g15)
    c: Horizontal(g28)
    c: Coincident(g27,g4)
    c: DistanceY(g9,g9) = 1.5
    c: Coincident(g16,g28)
    c: DistanceX(g20,g21) = 33
    c: DistanceY(g1,g22) = 16
    c: DistanceX(g20,g22) = 9
    c: DistanceY(g22,g0) = 6
    c: Coincident(g17,g18)
    c: DistanceY(g19,g0) = 22
    c: DistanceX(g17) = 77
    c: DistanceY(g17) = 182
FEATURE [Sketcher::SketchObject] Sketch102
  MapMode = 5
  Support = -> [XY_Plane]
  sketch-geometry (32):
    g0: LineSegment StartX=7 StartY=290 StartZ=0 EndX=50 EndY=290 EndZ=0
    g1: LineSegment StartX=50 StartY=233 StartZ=0 EndX=7 EndY=233 EndZ=0
    g2: ArcOfCircle CenterX=7 CenterY=288 CenterZ=0 NormalX=0 NormalY=0 NormalZ=1 AngleXU=0 Radius=2 StartAngle=1.5708 EndAngle=3.14159
    g3: ArcOfCircle CenterX=50 CenterY=288 CenterZ=0 NormalX=0 NormalY=0 NormalZ=1 AngleXU=0 Radius=2 StartAngle=0 EndAngle=1.5708
    g4: ArcOfCircle CenterX=50 CenterY=235 CenterZ=0 NormalX=0 NormalY=0 NormalZ=1 AngleXU=0 Radius=2 StartAngle=4.71239 EndAngle=6.28319
    g5: ArcOfCircle CenterX=7 CenterY=235 CenterZ=0 NormalX=0 NormalY=0 NormalZ=1 AngleXU=0 Radius=2 StartAngle=3.14159 EndAngle=4.71239
    g6: Circle CenterX=35.5 CenterY=284.5 CenterZ=0 NormalX=0 NormalY=0 NormalZ=1 AngleXU=0 Radius=3
    g7: Circle CenterX=35.5 CenterY=241.5 CenterZ=0 NormalX=0 NormalY=0 NormalZ=1 AngleXU=0 Radius=3
    g8: LineSegment StartX=43 StartY=286 StartZ=0 EndX=48 EndY=286 EndZ=0
    g9: LineSegment StartX=48 StartY=286 StartZ=0 EndX=48 EndY=283 EndZ=0
    g10: LineSegment StartX=48 StartY=283 StartZ=0 EndX=43 EndY=283 EndZ=0
    g11: LineSegment StartX=43 StartY=283 StartZ=0 EndX=43 EndY=286 EndZ=0
    g12: LineSegment StartX=23 StartY=286 StartZ=0 EndX=28 EndY=286 EndZ=0
    g13: LineSegment StartX=28 StartY=286 StartZ=0 EndX=28 EndY=283 EndZ=0
    g14: LineSegment StartX=28 StartY=283 StartZ=0 EndX=23 EndY=283 EndZ=0
    g15: LineSegment StartX=23 StartY=283 StartZ=0 EndX=23 EndY=286 EndZ=0
    g16: LineSegment StartX=23 StartY=243 StartZ=0 EndX=28 EndY=243 EndZ=0
    g17: LineSegment StartX=28 StartY=243 StartZ=0 EndX=28 EndY=240 EndZ=0
    g18: LineSegment StartX=28 StartY=240 StartZ=0 EndX=23 EndY=240 EndZ=0
    g19: LineSegment StartX=23 StartY=240 StartZ=0 EndX=23 EndY=243 EndZ=0
    g20: LineSegment StartX=43 StartY=243 StartZ=0 EndX=48 EndY=243 EndZ=0
    g21: LineSegment StartX=48 StartY=243 StartZ=0 EndX=48 EndY=240 EndZ=0
    g22: LineSegment StartX=48 StartY=240 StartZ=0 EndX=43 EndY=240 EndZ=0
    g23: LineSegment StartX=43 StartY=240 StartZ=0 EndX=43 EndY=243 EndZ=0
    g24: LineSegment StartX=5 StartY=288 StartZ=0 EndX=5 EndY=261.75 EndZ=0
    g25: LineSegment StartX=5 StartY=235 StartZ=0 EndX=5 EndY=261.25 EndZ=0
    g26: LineSegment StartX=52 StartY=288 StartZ=0 EndX=52 EndY=261.75 EndZ=0
    g27: LineSegment StartX=52 StartY=235 StartZ=0 EndX=52 EndY=261.25 EndZ=0
    g28: LineSegment StartX=35.5 StartY=252 StartZ=0 EndX=36.5 EndY=253.732 EndZ=0
    g29: LineSegment StartX=36.5 StartY=253.732 StartZ=0 EndX=34.5 EndY=253.732 EndZ=0
    g30: LineSegment StartX=34.5 StartY=253.732 StartZ=0 EndX=35.5 EndY=252 EndZ=0
    g31: Circle [constr] CenterX=35.5 CenterY=253.155 CenterZ=0 NormalX=0 NormalY=0 NormalZ=1 AngleXU=0 Radius=1.1547
  constraints (95):
    c: Horizontal(g0)
    c: Horizontal(g1)
    c: Tangent(g0,g2) = 1.5708
    c: Tangent(g0,g3) = 1.5708
    c: Tangent(g1,g4) = 1.5708
    c: Tangent(g1,g5) = 1.5708
    c: Radius(g2) = 2
    c: Equal(g2,g3)
    c: Equal(g2,g4)
    c: Equal(g2,g5)
    c: Radius(g6) = 3
    c: Equal(g6,g7)
    c: Coincident(g8,g9)
    c: Coincident(g9,g10)
    c: Coincident(g10,g11)
    c: Coincident(g11,g8)
    c: Horizontal(g8)
    c: Horizontal(g10)
    c: Vertical(g9)
    c: Vertical(g11)
    c: Coincident(g12,g13)
    c: Coincident(g13,g14)
    c: Coincident(g14,g15)
    c: Coincident(g15,g12)
    c: Horizontal(g12)
    c: Horizontal(g14)
    c: Vertical(g13)
    c: Vertical(g15)
    c: Coincident(g16,g17)
    c: Coincident(g17,g18)
    c: Coincident(g18,g19)
    c: Coincident(g19,g16)
    c: Horizontal(g16)
    c: Horizontal(g18)
    c: Vertical(g19)
    c: Coincident(g20,g21)
    c: Coincident(g21,g22)
    c: Coincident(g22,g23)
    c: Coincident(g23,g20)
    c: Horizontal(g20)
    c: Horizontal(g22)
    c: Vertical(g21)
    c: Vertical(g23)
    c: DistanceX(g10,g10) = 5
    c: DistanceY(g11,g11) = 3
    c: DistanceX(g6,g10) = 7.5
    c: DistanceX(g14,g14) = 5
    c: DistanceY(g15,g15) = 3
    c: DistanceX(g13,g6) = 7.5
    c: DistanceX(g22,g22) = 5
    c: DistanceY(g23,g23) = 3
    c: DistanceY(g19,g19) = 3
    c: DistanceX(g18,g18) = 5
    c: DistanceX(g17,g7) = 7.5
    c: DistanceX(g7,g22) = 7.5
    c: Vertical(g24)
    c: Vertical(g25)
    c: DistanceY(g25,g24) = 0.5
    c: Equal(g24,g25)
    c: Tangent(g25,g5) = 1.5708
    c: Tangent(g24,g2) = -1.5708
    c: DistanceX(g5,g18) = 18
    c: Vertical(g26)
    c: Vertical(g27)
    c: Vertical(g26,g27)
    c: DistanceY(g27,g26) = 0.5
    c: Equal(g26,g27)
    c: Horizontal(g3,g3)
    c: Tangent(g4,g27) = -1.5708
    c: Tangent(g26,g3) = 1.5708
    c: DistanceY(g16,g14) = 40
    c: DistanceY(g1,g18) = 7
    c: DistanceY(g12,g0) = 4
    c: DistanceX(g2,g12) = 18
    c: DistanceY(g1,g7) = 8.5
    c: DistanceY(g1,g21) = 7
    c: DistanceX(g21,g4) = 4
    c: DistanceY(g6,g0) = 5.5
    c: Vertical(g24,g25)
    c: DistanceY(g8,g0) = 4
    c: Vertical(g17)
    c: Coincident(g28,g29)
    c: Coincident(g29,g30)
    c: Coincident(g30,g28)
    c: Equal(g28,g29)
    c: Equal(g28,g30)
    c: PointOnObject(g28,g31)
    c: PointOnObject(g29,g31)
    c: PointOnObject(g30,g31)
    c: Horizontal(g29)
    c: DistanceX(g29,g29) = 2
    c: DistanceX(g28,g4) = 16.5
    c: DistanceY(g1,g28) = 19
    c: DistanceX(g1) = 7
    c: DistanceY(g1) = 233
FEATURE [Sketcher::SketchObject] Sketch103
  MapMode = 5
  Support = -> [XY_Plane]
  sketch-geometry (32):
    g0: LineSegment StartX=55 StartY=290 StartZ=0 EndX=98 EndY=290 EndZ=0
    g1: LineSegment StartX=98 StartY=233 StartZ=0 EndX=55 EndY=233 EndZ=0
    g2: ArcOfCircle CenterX=55 CenterY=288 CenterZ=0 NormalX=0 NormalY=0 NormalZ=1 AngleXU=0 Radius=2 StartAngle=1.5708 EndAngle=3.14159
    g3: ArcOfCircle CenterX=98 CenterY=288 CenterZ=0 NormalX=0 NormalY=0 NormalZ=1 AngleXU=0 Radius=2 StartAngle=0 EndAngle=1.5708
    g4: ArcOfCircle CenterX=98 CenterY=235 CenterZ=0 NormalX=0 NormalY=0 NormalZ=1 AngleXU=0 Radius=2 StartAngle=4.71239 EndAngle=6.28319
    g5: ArcOfCircle CenterX=55 CenterY=235 CenterZ=0 NormalX=0 NormalY=0 NormalZ=1 AngleXU=0 Radius=2 StartAngle=3.14159 EndAngle=4.71239
    g6: Circle CenterX=69.5 CenterY=284.5 CenterZ=0 NormalX=0 NormalY=0 NormalZ=1 AngleXU=0 Radius=3
    g7: Circle CenterX=69.5 CenterY=241.5 CenterZ=0 NormalX=0 NormalY=0 NormalZ=1 AngleXU=0 Radius=3
    g8: LineSegment StartX=77 StartY=286 StartZ=0 EndX=82 EndY=286 EndZ=0
    g9: LineSegment StartX=82 StartY=286 StartZ=0 EndX=82 EndY=283 EndZ=0
    g10: LineSegment StartX=82 StartY=283 StartZ=0 EndX=77 EndY=283 EndZ=0
    g11: LineSegment StartX=77 StartY=283 StartZ=0 EndX=77 EndY=286 EndZ=0
    g12: LineSegment StartX=57 StartY=286 StartZ=0 EndX=62 EndY=286 EndZ=0
    g13: LineSegment StartX=62 StartY=286 StartZ=0 EndX=62 EndY=283 EndZ=0
    g14: LineSegment StartX=62 StartY=283 StartZ=0 EndX=57 EndY=283 EndZ=0
    g15: LineSegment StartX=57 StartY=283 StartZ=0 EndX=57 EndY=286 EndZ=0
    g16: LineSegment StartX=57 StartY=243 StartZ=0 EndX=62 EndY=243 EndZ=0
    g17: LineSegment StartX=62 StartY=243 StartZ=0 EndX=62 EndY=240 EndZ=0
    g18: LineSegment StartX=62 StartY=240 StartZ=0 EndX=57 EndY=240 EndZ=0
    g19: LineSegment StartX=57 StartY=240 StartZ=0 EndX=57 EndY=243 EndZ=0
    g20: LineSegment StartX=77 StartY=243 StartZ=0 EndX=82 EndY=243 EndZ=0
    g21: LineSegment StartX=82 StartY=243 StartZ=0 EndX=82 EndY=240 EndZ=0
    g22: LineSegment StartX=82 StartY=240 StartZ=0 EndX=77 EndY=240 EndZ=0
    g23: LineSegment StartX=77 StartY=240 StartZ=0 EndX=77 EndY=243 EndZ=0
    g24: LineSegment StartX=53 StartY=288 StartZ=0 EndX=53 EndY=261.75 EndZ=0
    g25: LineSegment StartX=53 StartY=235 StartZ=0 EndX=53 EndY=261.25 EndZ=0
    g26: LineSegment StartX=100 StartY=288 StartZ=0 EndX=100 EndY=261.75 EndZ=0
    g27: LineSegment StartX=100 StartY=235 StartZ=0 EndX=100 EndY=261.25 EndZ=0
    g28: LineSegment StartX=69.5 StartY=252 StartZ=0 EndX=70.5 EndY=253.732 EndZ=0
    g29: LineSegment StartX=70.5 StartY=253.732 StartZ=0 EndX=68.5 EndY=253.732 EndZ=0
    g30: LineSegment StartX=68.5 StartY=253.732 StartZ=0 EndX=69.5 EndY=252 EndZ=0
    g31: Circle [constr] CenterX=69.5 CenterY=253.155 CenterZ=0 NormalX=0 NormalY=0 NormalZ=1 AngleXU=0 Radius=1.1547
  constraints (96):
    c: Horizontal(g0)
    c: Horizontal(g1)
    c: Tangent(g0,g2) = 1.5708
    c: Tangent(g0,g3) = 1.5708
    c: Tangent(g1,g4) = 1.5708
    c: Tangent(g1,g5) = 1.5708
    c: Radius(g2) = 2
    c: Equal(g2,g3)
    c: Equal(g2,g4)
    c: Equal(g2,g5)
    c: Radius(g6) = 3
    c: Equal(g6,g7)
    c: Coincident(g8,g9)
    c: Coincident(g9,g10)
    c: Coincident(g10,g11)
    c: Coincident(g11,g8)
    c: Horizontal(g8)
    c: Horizontal(g10)
    c: Vertical(g9)
    c: Vertical(g11)
    c: Coincident(g12,g13)
    c: Coincident(g13,g14)
    c: Coincident(g14,g15)
    c: Coincident(g15,g12)
    c: Horizontal(g12)
    c: Horizontal(g14)
    c: Vertical(g13)
    c: Vertical(g15)
    c: Coincident(g16,g17)
    c: Coincident(g17,g18)
    c: Coincident(g18,g19)
    c: Coincident(g19,g16)
    c: Horizontal(g16)
    c: Horizontal(g18)
    c: Vertical(g19)
    c: Coincident(g20,g21)
    c: Coincident(g21,g22)
    c: Coincident(g22,g23)
    c: Coincident(g23,g20)
    c: Horizontal(g20)
    c: Horizontal(g22)
    c: Vertical(g21)
    c: Vertical(g23)
    c: DistanceX(g10,g10) = 5
    c: DistanceY(g11,g11) = 3
    c: DistanceX(g6,g10) = 7.5
    c: DistanceX(g14,g14) = 5
    c: DistanceY(g15,g15) = 3
    c: DistanceX(g13,g6) = 7.5
    c: DistanceX(g22,g22) = 5
    c: DistanceY(g23,g23) = 3
    c: DistanceY(g19,g19) = 3
    c: DistanceX(g18,g18) = 5
    c: DistanceX(g17,g7) = 7.5
    c: DistanceX(g7,g22) = 7.5
    c: Vertical(g24)
    c: Vertical(g25)
    c: DistanceY(g25,g24) = 0.5
    c: Equal(g24,g25)
    c: Tangent(g25,g5) = 1.5708
    c: Tangent(g24,g2) = -1.5708
    c: DistanceX(g5,g18) = 4
    c: Vertical(g26)
    c: Vertical(g27)
    c: Vertical(g26,g27)
    c: DistanceY(g27,g26) = 0.5
    c: Equal(g26,g27)
    c: Horizontal(g3,g3)
    c: Tangent(g4,g27) = -1.5708
    c: Tangent(g26,g3) = 1.5708
    c: DistanceY(g16,g14) = 40
    c: DistanceY(g1,g18) = 7
    c: DistanceY(g12,g0) = 4
    c: DistanceX(g2,g12) = 4
    c: DistanceY(g1,g7) = 8.5
    c: DistanceY(g1,g21) = 7
    c: DistanceX(g21,g4) = 18
    c: DistanceY(g6,g0) = 5.5
    c: Vertical(g24,g25)
    c: DistanceY(g8,g0) = 4
    c: Vertical(g17)
    c: Coincident(g28,g29)
    c: Coincident(g29,g30)
    c: Coincident(g30,g28)
    c: Equal(g28,g29)
    c: Equal(g28,g30)
    c: PointOnObject(g28,g31)
    c: PointOnObject(g29,g31)
    c: PointOnObject(g30,g31)
    c: Horizontal(g29)
    c: DistanceX(g29,g29) = 2
    c: DistanceX(g8,g3) = 18
    c: DistanceX(g5,g28) = 16.5
    c: DistanceY(g1,g28) = 19
    c: DistanceX(g1) = 55
    c: DistanceY(g1) = 233
FEATURE [Sketcher::SketchObject] Sketch104
  MapMode = 5
  Support = -> [XY_Plane]
  sketch-geometry (16):
    g0: LineSegment StartX=75 StartY=232 StartZ=0 EndX=104 EndY=232 EndZ=0
    g1: LineSegment StartX=92.3 StartY=214 StartZ=0 EndX=92.3 EndY=216.5 EndZ=0
    g2: LineSegment StartX=92.3 StartY=216.5 StartZ=0 EndX=86.7 EndY=216.5 EndZ=0
    g3: LineSegment StartX=86.7 StartY=216.5 StartZ=0 EndX=86.7 EndY=214 EndZ=0
    g4: LineSegment StartX=86.7 StartY=214 StartZ=0 EndX=92.3 EndY=214 EndZ=0
    g5: LineSegment StartX=106 StartY=210 StartZ=0 EndX=73 EndY=210 EndZ=0
    g6: ArcOfCircle CenterX=75 CenterY=230 CenterZ=0 NormalX=0 NormalY=0 NormalZ=1 AngleXU=0 Radius=2 StartAngle=1.5708 EndAngle=3.14159
    g7: ArcOfCircle CenterX=104 CenterY=230 CenterZ=0 NormalX=0 NormalY=0 NormalZ=1 AngleXU=0 Radius=2 StartAngle=0 EndAngle=1.5708
    g8: LineSegment StartX=73 StartY=230 StartZ=0 EndX=73 EndY=220.25 EndZ=0
    g9: LineSegment StartX=73 StartY=210 StartZ=0 EndX=73 EndY=219.75 EndZ=0
    g10: LineSegment StartX=106 StartY=230 StartZ=0 EndX=106 EndY=220.25 EndZ=0
    g11: LineSegment StartX=106 StartY=210 StartZ=0 EndX=106 EndY=219.75 EndZ=0
    g12: LineSegment StartX=82.2606 StartY=229.39 StartZ=0 EndX=96.5263 EndY=228.293 EndZ=0
    g13: ArcOfCircle CenterX=96.35 CenterY=226 CenterZ=0 NormalX=0 NormalY=0 NormalZ=1 AngleXU=0 Radius=2.3 StartAngle=4.78912 EndAngle=7.77725
    g14: LineSegment StartX=96.5263 StartY=223.707 StartZ=0 EndX=82.2606 EndY=222.61 EndZ=0
    g15: ArcOfCircle CenterX=82 CenterY=226 CenterZ=0 NormalX=0 NormalY=0 NormalZ=1 AngleXU=0 Radius=3.4 StartAngle=1.49407 EndAngle=4.78912
  constraints (47):
    c: Horizontal(g0)
    c: Vertical(g1)
    c: Coincident(g1,g2)
    c: Horizontal(g2)
    c: Vertical(g3)
    c: Coincident(g3,g4)
    c: Horizontal(g4)
    c: Horizontal(g5)
    c: DistanceY(g3,g3) = 2.5
    c: DistanceY(g1,g1) = 2.5
    c: DistanceY(g5,g4) = 4
    c: Tangent(g0,g6) = 1.5708
    c: Radius(g6) = 2
    c: Radius(g7) = 2
    c: Vertical(g8)
    c: Coincident(g9,g5)
    c: Vertical(g9)
    c: Tangent(g8,g6) = -1.5708
    c: Vertical(g8,g9)
    c: DistanceY(g9,g8) = 0.5
    c: Equal(g8,g9)
    c: Vertical(g10)
    c: Vertical(g11)
    c: Vertical(g10,g11)
    c: DistanceY(g11,g10) = 0.5
    c: Equal(g10,g11)
    c: Tangent(g10,g7) = 1.5708
    c: Tangent(g0,g7) = 1.5708
    c: DistanceX(g6,g7) = 33
    c: DistanceY(g5,g0) = 22
    c: Tangent(g12,g13) = 1.5708
    c: Tangent(g14,g15) = 1.5708
    c: Tangent(g15,g12) = 1.5708
    c: Tangent(g13,g14) = 1.5708
    c: Radius(g15) = 3.4
    c: Radius(g13) = 2.3
    c: Horizontal(g15,g13)
    c: DistanceX(g15,g13) = 14.35
    c: DistanceY(g15,g0) = 6
    c: DistanceX(g6,g15) = 9
    c: Coincident(g2,g3)
    c: DistanceX(g2,g2) = 5.6
    c: Coincident(g1,g4)
    c: Coincident(g5,g11)
    c: DistanceX(g5,g3) = 13.7
    c: DistanceX(g5) = 73
    c: DistanceY(g5) = 210
FEATURE [Sketcher::SketchObject] Sketch105
  MapMode = 5
  Support = -> [XY_Plane]
  sketch-geometry (16):
    g0: LineSegment StartX=109 StartY=232 StartZ=0 EndX=138 EndY=232 EndZ=0
    g1: LineSegment StartX=126.3 StartY=214 StartZ=0 EndX=126.3 EndY=216.5 EndZ=0
    g2: LineSegment StartX=126.3 StartY=216.5 StartZ=0 EndX=120.7 EndY=216.5 EndZ=0
    g3: LineSegment StartX=120.7 StartY=216.5 StartZ=0 EndX=120.7 EndY=214 EndZ=0
    g4: LineSegment StartX=120.7 StartY=214 StartZ=0 EndX=126.3 EndY=214 EndZ=0
    g5: LineSegment StartX=140 StartY=210 StartZ=0 EndX=107 EndY=210 EndZ=0
    g6: ArcOfCircle CenterX=109 CenterY=230 CenterZ=0 NormalX=0 NormalY=0 NormalZ=1 AngleXU=0 Radius=2 StartAngle=1.5708 EndAngle=3.14159
    g7: ArcOfCircle CenterX=138 CenterY=230 CenterZ=0 NormalX=0 NormalY=0 NormalZ=1 AngleXU=0 Radius=2 StartAngle=0 EndAngle=1.5708
    g8: LineSegment StartX=107 StartY=230 StartZ=0 EndX=107 EndY=220.25 EndZ=0
    g9: LineSegment StartX=107 StartY=210 StartZ=0 EndX=107 EndY=219.75 EndZ=0
    g10: LineSegment StartX=140 StartY=230 StartZ=0 EndX=140 EndY=220.25 EndZ=0
    g11: LineSegment StartX=140 StartY=210 StartZ=0 EndX=140 EndY=219.75 EndZ=0
    g12: LineSegment StartX=130.739 StartY=229.39 StartZ=0 EndX=116.474 EndY=228.293 EndZ=0
    g13: ArcOfCircle CenterX=116.65 CenterY=226 CenterZ=0 NormalX=0 NormalY=0 NormalZ=1 AngleXU=0 Radius=2.3 StartAngle=1.64753 EndAngle=4.63566
    g14: LineSegment StartX=116.474 StartY=223.707 StartZ=0 EndX=130.739 EndY=222.61 EndZ=0
    g15: ArcOfCircle CenterX=131 CenterY=226 CenterZ=0 NormalX=0 NormalY=0 NormalZ=1 AngleXU=0 Radius=3.4 StartAngle=4.63566 EndAngle=7.93071
  constraints (47):
    c: Horizontal(g0)
    c: Vertical(g1)
    c: Coincident(g1,g2)
    c: Horizontal(g2)
    c: Vertical(g3)
    c: Coincident(g3,g4)
    c: Horizontal(g4)
    c: Horizontal(g5)
    c: DistanceY(g3,g3) = 2.5
    c: DistanceY(g1,g1) = 2.5
    c: DistanceY(g5,g4) = 4
    c: Tangent(g0,g6) = 1.5708
    c: Radius(g6) = 2
    c: Radius(g7) = 2
    c: Vertical(g8)
    c: Coincident(g9,g5)
    c: Vertical(g9)
    c: Tangent(g8,g6) = -1.5708
    c: Vertical(g8,g9)
    c: DistanceY(g9,g8) = 0.5
    c: Equal(g8,g9)
    c: Vertical(g10)
    c: Vertical(g11)
    c: Vertical(g10,g11)
    c: DistanceY(g11,g10) = 0.5
    c: Equal(g10,g11)
    c: Tangent(g10,g7) = 1.5708
    c: Tangent(g0,g7) = 1.5708
    c: DistanceX(g6,g7) = 33
    c: DistanceY(g5,g0) = 22
    c: Coincident(g2,g3)
    c: DistanceX(g2,g2) = 5.6
    c: Coincident(g1,g4)
    c: Coincident(g5,g11)
    c: DistanceX(g5,g3) = 13.7
    c: Tangent(g12,g13) = -1.5708
    c: Tangent(g14,g15) = -1.5708
    c: Tangent(g15,g12) = -1.5708
    c: Tangent(g13,g14) = -1.5708
    c: Radius(g15) = 3.4
    c: Radius(g13) = 2.3
    c: Horizontal(g13,g15)
    c: DistanceX(g13,g15) = 14.35
    c: DistanceY(g15,g0) = 6
    c: DistanceX(g15,g7) = 9
    c: DistanceX(g5) = 107
    c: DistanceY(g5) = 210
FEATURE [Sketcher::SketchObject] Sketch107
  MapMode = 5
  Support = -> [XY_Plane]
  sketch-geometry (14):
    g0: LineSegment StartX=186.75 StartY=265 StartZ=0 EndX=204 EndY=265 EndZ=0
    g1: LineSegment StartX=204 StartY=265 StartZ=0 EndX=204 EndY=260 EndZ=0
    g2: LineSegment StartX=204 StartY=260 StartZ=0 EndX=201 EndY=260 EndZ=0
    g3: LineSegment StartX=201 StartY=260 StartZ=0 EndX=201 EndY=255 EndZ=0
    g4: LineSegment StartX=201 StartY=255 StartZ=0 EndX=204 EndY=255 EndZ=0
    g5: LineSegment StartX=204 StartY=255 StartZ=0 EndX=204 EndY=250 EndZ=0
    g6: LineSegment StartX=204 StartY=250 StartZ=0 EndX=186.75 EndY=250 EndZ=0
    g7: LineSegment StartX=186.25 StartY=265 StartZ=0 EndX=169 EndY=265 EndZ=0
    g8: LineSegment StartX=169 StartY=265 StartZ=0 EndX=169 EndY=260 EndZ=0
    g9: LineSegment StartX=169 StartY=260 StartZ=0 EndX=172 EndY=260 EndZ=0
    g10: LineSegment StartX=172 StartY=260 StartZ=0 EndX=172 EndY=255 EndZ=0
    g11: LineSegment StartX=172 StartY=255 StartZ=0 EndX=169 EndY=255 EndZ=0
    g12: LineSegment StartX=169 StartY=255 StartZ=0 EndX=169 EndY=250 EndZ=0
    g13: LineSegment StartX=169 StartY=250 StartZ=0 EndX=186.25 EndY=250 EndZ=0
  constraints (45):
    c: Horizontal(g0)
    c: Coincident(g0,g1)
    c: Vertical(g1)
    c: Coincident(g1,g2)
    c: Horizontal(g2)
    c: Coincident(g2,g3)
    c: Coincident(g3,g4)
    c: Horizontal(g4)
    c: Coincident(g4,g5)
    c: Coincident(g5,g6)
    c: Horizontal(g6)
    c: Vertical(g5)
    c: Vertical(g3)
    c: DistanceY(g1,g1) = 5
    c: DistanceY(g3,g3) = 5
    c: DistanceY(g5,g5) = 5
    c: DistanceX(g0,g0) = 17.25
    c: DistanceX(g6,g6) = 17.25
    c: Horizontal(g7)
    c: Coincident(g7,g8)
    c: Vertical(g8)
    c: Coincident(g8,g9)
    c: Horizontal(g9)
    c: Coincident(g9,g10)
    c: Vertical(g10)
    c: Coincident(g10,g11)
    c: Horizontal(g11)
    c: Coincident(g11,g12)
    c: Vertical(g12)
    c: Coincident(g12,g13)
    c: Horizontal(g13)
    c: DistanceY(g8,g8) = 5
    c: DistanceY(g10,g10) = 5
    c: DistanceY(g12,g12) = 5
    c: DistanceX(g7,g7) = 17.25
    c: DistanceX(g13,g13) = 17.25
    c: Horizontal(g0,g7)
    c: DistanceX(g7,g0) = 0.5
    c: DistanceX(g13,g6) = 0.5
    c: DistanceX(g11,g11) = 3
    c: DistanceX(g9,g9) = 3
    c: DistanceX(g2,g2) = 3
    c: DistanceX(g7,g0) = 35
    c: DistanceX(g12) = 169
    c: DistanceY(g12) = 250
FEATURE [Sketcher::SketchObject] Sketch108
  MapMode = 5
  Support = -> [XY_Plane]
  sketch-geometry (14):
    g0: LineSegment StartX=186.75 StartY=249 StartZ=0 EndX=204 EndY=249 EndZ=0
    g1: LineSegment StartX=204 StartY=249 StartZ=0 EndX=204 EndY=244 EndZ=0
    g2: LineSegment StartX=204 StartY=244 StartZ=0 EndX=201 EndY=244 EndZ=0
    g3: LineSegment StartX=201 StartY=244 StartZ=0 EndX=201 EndY=239 EndZ=0
    g4: LineSegment StartX=201 StartY=239 StartZ=0 EndX=204 EndY=239 EndZ=0
    g5: LineSegment StartX=204 StartY=239 StartZ=0 EndX=204 EndY=234 EndZ=0
    g6: LineSegment StartX=204 StartY=234 StartZ=0 EndX=186.75 EndY=234 EndZ=0
    g7: LineSegment StartX=186.25 StartY=249 StartZ=0 EndX=169 EndY=249 EndZ=0
    g8: LineSegment StartX=169 StartY=249 StartZ=0 EndX=169 EndY=244 EndZ=0
    g9: LineSegment StartX=169 StartY=244 StartZ=0 EndX=172 EndY=244 EndZ=0
    g10: LineSegment StartX=172 StartY=244 StartZ=0 EndX=172 EndY=239 EndZ=0
    g11: LineSegment StartX=172 StartY=239 StartZ=0 EndX=169 EndY=239 EndZ=0
    g12: LineSegment StartX=169 StartY=239 StartZ=0 EndX=169 EndY=234 EndZ=0
    g13: LineSegment StartX=169 StartY=234 StartZ=0 EndX=186.25 EndY=234 EndZ=0
  constraints (44):
    c: Horizontal(g0)
    c: Coincident(g0,g1)
    c: Vertical(g1)
    c: Coincident(g1,g2)
    c: Horizontal(g2)
    c: Coincident(g2,g3)
    c: Coincident(g3,g4)
    c: Horizontal(g4)
    c: Coincident(g4,g5)
    c: Coincident(g5,g6)
    c: Horizontal(g6)
    c: Vertical(g5)
    c: Vertical(g3)
    c: DistanceY(g1,g1) = 5
    c: DistanceY(g3,g3) = 5
    c: DistanceY(g5,g5) = 5
    c: DistanceX(g0,g0) = 17.25
    c: DistanceX(g6,g6) = 17.25
    c: Horizontal(g7)
    c: Coincident(g7,g8)
    c: Vertical(g8)
    c: Coincident(g8,g9)
    c: Horizontal(g9)
    c: Coincident(g9,g10)
    c: Vertical(g10)
    c: Coincident(g10,g11)
    c: Horizontal(g11)
    c: Coincident(g11,g12)
    c: Vertical(g12)
    c: Coincident(g12,g13)
    c: Horizontal(g13)
    c: DistanceY(g8,g8) = 5
    c: DistanceY(g10,g10) = 5
    c: DistanceY(g12,g12) = 5
    c: DistanceX(g7,g7) = 17.25
    c: DistanceX(g13,g13) = 17.25
    c: Horizontal(g0,g7)
    c: DistanceX(g7,g0) = 0.5
    c: DistanceX(g13,g6) = 0.5
    c: DistanceX(g11,g11) = 3
    c: DistanceX(g9,g9) = 3
    c: DistanceX(g2,g2) = 3
    c: DistanceX(g12) = 169
    c: DistanceY(g12) = 234
FEATURE [Sketcher::SketchObject] Sketch003
  MapMode = 5
  sketch-geometry (19):
    g0: LineSegment StartX=5 StartY=139 StartZ=0 EndX=25 EndY=139 EndZ=0
    g1: LineSegment StartX=65 StartY=139 StartZ=0 EndX=65 EndY=79 EndZ=0
    g2: LineSegment StartX=65 StartY=79 StartZ=0 EndX=45 EndY=79 EndZ=0
    g3: LineSegment StartX=5 StartY=79 StartZ=0 EndX=5 EndY=139 EndZ=0
    g4: LineSegment StartX=45 StartY=79 StartZ=0 EndX=45 EndY=76 EndZ=0
    g5: LineSegment StartX=25 StartY=76 StartZ=0 EndX=25 EndY=79 EndZ=0
    g6: LineSegment StartX=45 StartY=139 StartZ=0 EndX=45 EndY=142 EndZ=0
    g7: LineSegment StartX=25 StartY=142 StartZ=0 EndX=25 EndY=139 EndZ=0
    g8: LineSegment StartX=45 StartY=139 StartZ=0 EndX=65 EndY=139 EndZ=0
    g9: LineSegment StartX=25 StartY=79 StartZ=0 EndX=5 EndY=79 EndZ=0
    g10: Circle CenterX=22.25 CenterY=109 CenterZ=0 NormalX=0 NormalY=0 NormalZ=1 AngleXU=0 Radius=7.9
    g11: Circle CenterX=47.75 CenterY=109 CenterZ=0 NormalX=0 NormalY=0 NormalZ=1 AngleXU=0 Radius=7.9
    g12: LineSegment [constr] StartX=35 StartY=139 StartZ=0 EndX=35 EndY=79 EndZ=0
    g13: LineSegment StartX=25 StartY=142 StartZ=0 EndX=34.75 EndY=142 EndZ=0
    g14: LineSegment StartX=45 StartY=142 StartZ=0 EndX=35.25 EndY=142 EndZ=0
    g15: LineSegment [constr] StartX=25 StartY=139 StartZ=0 EndX=45 EndY=139 EndZ=0
    g16: LineSegment [constr] StartX=25 StartY=79 StartZ=0 EndX=45 EndY=79 EndZ=0
    g17: LineSegment StartX=25 StartY=76 StartZ=0 EndX=34.75 EndY=76 EndZ=0
    g18: LineSegment StartX=45 StartY=76 StartZ=0 EndX=35.25 EndY=76 EndZ=0
  constraints (62):
    c: Coincident(g8,g1)
    c: Coincident(g1,g2)
    c: Coincident(g9,g3)
    c: Coincident(g3,g0)
    c: Horizontal(g0)
    c: Horizontal(g2)
    c: Vertical(g1)
    c: Vertical(g3)
    c: Vertical(g4)
    c: Vertical(g5)
    c: PointOnObject(g5,g2)
    c: Vertical(g6)
    c: Vertical(g7)
    c: PointOnObject(g7,g0)
    c: PointOnObject(g0,g7)
    c: PointOnObject(g8,g6)
    c: Tangent(g0,g8)
    c: PointOnObject(g2,g4)
    c: PointOnObject(g9,g5)
    c: Tangent(g2,g9)
    c: DistanceX(g5,g4) = 20
    c: DistanceX(g9,g9) = 20
    c: DistanceX(g2,g2) = 20
    c: DistanceY(g5,g5) = 3
    c: DistanceY(g3,g3) = 60
    c: Coincident(g6,g8)
    c: DistanceY(g7,g7) = 3
    c: DistanceX(g0,g0) = 20
    c: DistanceX(g8,g8) = 20
    c: DistanceX(g-1,g3) = 5
    c: Coincident(g4,g2)
    c: Radius(g10) = 7.9
    c: Horizontal(g11,g10)
    c: DistanceX(g10,g11) = 25.5
    c: Symmetric(g5,g2,g12)
    c: Symmetric(g11,g10,g12)
    c: DistanceY(g3,g10) = 30
    c: DistanceY(g-1,g3) = 79
    c: Coincident(g13,g7)
    c: Horizontal(g13)
    c: Coincident(g14,g6)
    c: Horizontal(g14)
    c: DistanceX(g13,g14) = 0.5
    c: Coincident(g15,g0)
    c: Coincident(g15,g6)
    c: PointOnObject(g12,g15)
    c: Coincident(g16,g5)
    c: Coincident(g16,g2)
    c: DistanceX(g7,g13) = 9.75
    c: PointOnObject(g12,g16)
    c: Coincident(g17,g5)
    c: Horizontal(g17)
    c: Coincident(g18,g4)
    c: Horizontal(g18)
    c: DistanceX(g17,g18) = 0.5
    c: DistanceX(g17,g17) = 9.75
    c: Horizontal(g17,g18)
    c: Horizontal(g13,g14)
    c: Radius(g11) = 7.9
    c: DistanceX(g0,g1) = 60
    c: DistanceX(g0,g10) = 17.25
    c: DistanceX(g11,g1) = 17.25
FEATURE [Sketcher::SketchObject] Sketch109
  MapMode = 5
  Support = -> [XY_Plane]
  sketch-geometry (32):
    g0: LineSegment StartX=102.75 StartY=181.1 StartZ=0 EndX=82 EndY=181.1 EndZ=0
    g1: ArcOfCircle CenterX=132 CenterY=180.1 CenterZ=0 NormalX=0 NormalY=0 NormalZ=1 AngleXU=0 Radius=1 StartAngle=0 EndAngle=1.5708
    g2: LineSegment StartX=132 StartY=181.1 StartZ=0 EndX=103.25 EndY=181.1 EndZ=0
    g3: LineSegment StartX=133 StartY=180.1 StartZ=0 EndX=133 EndY=163 EndZ=0
    g4: LineSegment StartX=83 StartY=163 StartZ=0 EndX=83 EndY=166 EndZ=0
    g5: LineSegment StartX=83 StartY=166 StartZ=0 EndX=93 EndY=166 EndZ=0
    g6: LineSegment StartX=93 StartY=166 StartZ=0 EndX=93 EndY=163 EndZ=0
    g7: LineSegment StartX=73 StartY=163 StartZ=0 EndX=73 EndY=180.1 EndZ=0
    g8: ArcOfCircle CenterX=79 CenterY=174.1 CenterZ=0 NormalX=0 NormalY=0 NormalZ=1 AngleXU=0 Radius=1 StartAngle=3.14159 EndAngle=4.71239
    g9: LineSegment StartX=79 StartY=173.1 StartZ=0 EndX=87 EndY=173.1 EndZ=0
    g10: ArcOfCircle CenterX=87 CenterY=174.1 CenterZ=0 NormalX=0 NormalY=0 NormalZ=1 AngleXU=0 Radius=1 StartAngle=4.71239 EndAngle=6.28319
    g11: LineSegment StartX=88 StartY=174.1 StartZ=0 EndX=88 EndY=175.1 EndZ=0
    g12: ArcOfCircle CenterX=87 CenterY=175.1 CenterZ=0 NormalX=0 NormalY=0 NormalZ=1 AngleXU=0 Radius=1 StartAngle=0 EndAngle=1.5708
    g13: LineSegment StartX=77 StartY=181.1 StartZ=0 EndX=74 EndY=181.1 EndZ=0
    g14: ArcOfCircle CenterX=74 CenterY=180.1 CenterZ=0 NormalX=0 NormalY=0 NormalZ=1 AngleXU=0 Radius=1 StartAngle=1.5708 EndAngle=3.14159
    g15: ArcOfCircle CenterX=82 CenterY=180.1 CenterZ=0 NormalX=0 NormalY=0 NormalZ=1 AngleXU=0 Radius=1 StartAngle=1.5708 EndAngle=3.14159
    g16: LineSegment StartX=81 StartY=180.1 StartZ=0 EndX=81 EndY=177.1 EndZ=0
    g17: ArcOfCircle CenterX=82 CenterY=177.1 CenterZ=0 NormalX=0 NormalY=0 NormalZ=1 AngleXU=0 Radius=1 StartAngle=3.14159 EndAngle=4.71239
    g18: LineSegment StartX=82 StartY=176.1 StartZ=0 EndX=87 EndY=176.1 EndZ=0
    g19: ArcOfCircle CenterX=77 CenterY=180.1 CenterZ=0 NormalX=0 NormalY=0 NormalZ=1 AngleXU=0 Radius=1 StartAngle=0 EndAngle=1.5708
    g20: LineSegment StartX=78 StartY=180.1 StartZ=0 EndX=78 EndY=174.1 EndZ=0
    g21: Circle CenterX=121.5 CenterY=172.05 CenterZ=0 NormalX=0 NormalY=0 NormalZ=1 AngleXU=0 Radius=1.5
    g22: LineSegment StartX=73 StartY=163 StartZ=0 EndX=83 EndY=163 EndZ=0
    g23: LineSegment StartX=133 StartY=163 StartZ=0 EndX=123 EndY=163 EndZ=0
    g24: LineSegment StartX=123 StartY=163 StartZ=0 EndX=123 EndY=166 EndZ=0
    g25: LineSegment StartX=123 StartY=166 StartZ=0 EndX=113 EndY=166 EndZ=0
    g26: LineSegment StartX=113 StartY=166 StartZ=0 EndX=113 EndY=163 EndZ=0
    g27: LineSegment StartX=113 StartY=163 StartZ=0 EndX=103.25 EndY=163 EndZ=0
    g28: Circle CenterX=98 CenterY=164.5 CenterZ=0 NormalX=0 NormalY=0 NormalZ=1 AngleXU=0 Radius=1
    g29: LineSegment StartX=93 StartY=163 StartZ=0 EndX=95.4019 EndY=163 EndZ=0
    g30: ArcOfCircle CenterX=98 CenterY=164.5 CenterZ=0 NormalX=0 NormalY=0 NormalZ=1 AngleXU=0 Radius=3 StartAngle=3.66519 EndAngle=5.75959
    g31: LineSegment StartX=100.598 StartY=163 StartZ=0 EndX=102.75 EndY=163 EndZ=0
  constraints (91):
    c: Horizontal(g0)
    c: Horizontal(g2)
    c: Horizontal(g0,g2)
    c: DistanceX(g0,g2) = 0.5
    c: Tangent(g1,g2) = -1.5708
    c: Radius(g1) = 1
    c: Horizontal(g1,g1)
    c: Vertical(g3)
    c: Tangent(g3,g1) = 1.5708
    c: Vertical(g4)
    c: Coincident(g4,g5)
    c: Horizontal(g5)
    c: Coincident(g5,g6)
    c: Vertical(g6)
    c: DistanceY(g4,g4) = 3
    c: Vertical(g7)
    c: Horizontal(g9)
    c: Tangent(g9,g10) = -1.5708
    c: Vertical(g11)
    c: Tangent(g11,g12) = -1.5708
    c: Radius(g12) = 1
    c: Radius(g10) = 1
    c: Radius(g8) = 1
    c: DistanceY(g11,g11) = 1
    c: Tangent(g10,g11) = -1.5708
    c: DistanceX(g9,g9) = 8
    c: Tangent(g8,g9) = -1.5708
    c: Horizontal(g13)
    c: Tangent(g13,g14) = -1.5708
    c: Tangent(g14,g7) = 1.5708
    c: Radius(g14) = 1
    c: Tangent(g0,g15) = -1.5708
    c: Vertical(g16)
    c: Tangent(g16,g17) = -1.5708
    c: Tangent(g15,g16) = -1.5708
    c: Radius(g15) = 1
    c: Radius(g17) = 1
    c: DistanceY(g16,g16) = 3
    c: Horizontal(g18)
    c: Tangent(g13,g19) = -1.5708
    c: Vertical(g20)
    c: Tangent(g19,g20) = 1.5708
    c: Radius(g19) = 1
    c: DistanceX(g13,g13) = 3
    c: Tangent(g20,g8) = -1.5708
    c: Tangent(g12,g18) = 1.5708
    c: Tangent(g17,g18) = -1.5708
    c: DistanceX(g7,g3) = 60
    c: DistanceY(g7,g13) = 18.1
    c: DistanceY(g3,g1) = 18.1
    c: DistanceX(g19,g15) = 3
    c: Radius(g21) = 1.5
    c: DistanceX(g21,g1) = 11.5
    c: DistanceY(g21,g1) = 9.05
    c: DistanceX(g5,g5) = 10
    c: DistanceX(g7,g4) = 10
    c: Coincident(g7,g22)
    c: Horizontal(g22)
    c: Coincident(g4,g22)
    c: Coincident(g3,g23)
    c: Horizontal(g23)
    c: Coincident(g23,g24)
    c: Vertical(g24)
    c: Coincident(g24,g25)
    c: Horizontal(g25)
    c: Coincident(g25,g26)
    c: Vertical(g26)
    c: Coincident(g26,g27)
    c: Horizontal(g27)
    c: DistanceX(g23,g23) = 10
    c: DistanceX(g25,g25) = 10
    c: DistanceY(g6,g6) = 3
    c: DistanceX(g27,g27) = 9.75
    c: DistanceY(g24,g24) = 3
    c: DistanceY(g26,g26) = 3
    c: Radius(g28) = 1
    c: DistanceY(g7,g28) = 1.5
    c: DistanceX(g7,g28) = 25
    c: DistanceX(g7) = 73
    c: DistanceY(g7) = 163
    c: Coincident(g6,g29)
    c: Horizontal(g29)
    c: Coincident(g30,g31)
    c: Horizontal(g27,g31)
    c: DistanceX(g31,g27) = 0.5
    c: Coincident(g30,g28)
    c: Horizontal(g31)
    c: Radius(g30) = 3
    c: Coincident(g29,g30)
    c: Horizontal(g30,g29)
    c: Vertical(g0,g31)
FEATURE [Sketcher::SketchObject] Sketch110
  MapMode = 5
  Support = -> [XY_Plane]
  sketch-geometry (32):
    g0: LineSegment StartX=102.75 StartY=161.1 StartZ=0 EndX=74 EndY=161.1 EndZ=0
    g1: ArcOfCircle CenterX=132 CenterY=160.1 CenterZ=0 NormalX=0 NormalY=0 NormalZ=1 AngleXU=0 Radius=1 StartAngle=0 EndAngle=1.5708
    g2: LineSegment StartX=133 StartY=160.1 StartZ=0 EndX=133 EndY=143 EndZ=0
    g3: LineSegment StartX=113 StartY=143 StartZ=0 EndX=113 EndY=146 EndZ=0
    g4: LineSegment StartX=113 StartY=146 StartZ=0 EndX=123 EndY=146 EndZ=0
    g5: LineSegment StartX=123 StartY=146 StartZ=0 EndX=123 EndY=143 EndZ=0
    g6: LineSegment StartX=73 StartY=143 StartZ=0 EndX=73 EndY=160.1 EndZ=0
    g7: ArcOfCircle CenterX=119 CenterY=154.1 CenterZ=0 NormalX=0 NormalY=0 NormalZ=1 AngleXU=0 Radius=1 StartAngle=3.14159 EndAngle=4.71239
    g8: LineSegment StartX=119 StartY=153.1 StartZ=0 EndX=127 EndY=153.1 EndZ=0
    g9: ArcOfCircle CenterX=127 CenterY=154.1 CenterZ=0 NormalX=0 NormalY=0 NormalZ=1 AngleXU=0 Radius=1 StartAngle=4.71239 EndAngle=6.28319
    g10: ArcOfCircle CenterX=74 CenterY=160.1 CenterZ=0 NormalX=0 NormalY=0 NormalZ=1 AngleXU=0 Radius=1 StartAngle=1.5708 EndAngle=3.14159
    g11: LineSegment StartX=119 StartY=156.1 StartZ=0 EndX=124 EndY=156.1 EndZ=0
    g12: LineSegment StartX=132 StartY=161.1 StartZ=0 EndX=129 EndY=161.1 EndZ=0
    g13: ArcOfCircle CenterX=129 CenterY=160.1 CenterZ=0 NormalX=0 NormalY=0 NormalZ=1 AngleXU=0 Radius=1 StartAngle=1.5708 EndAngle=3.14159
    g14: LineSegment StartX=128 StartY=160.1 StartZ=0 EndX=128 EndY=154.1 EndZ=0
    g15: ArcOfCircle CenterX=124 CenterY=157.1 CenterZ=0 NormalX=0 NormalY=0 NormalZ=1 AngleXU=0 Radius=1 StartAngle=4.71239 EndAngle=6.28319
    g16: LineSegment StartX=125 StartY=157.1 StartZ=0 EndX=125 EndY=160.1 EndZ=0
    g17: ArcOfCircle CenterX=124 CenterY=160.1 CenterZ=0 NormalX=0 NormalY=0 NormalZ=1 AngleXU=0 Radius=1 StartAngle=0 EndAngle=1.5708
    g18: LineSegment StartX=124 StartY=161.1 StartZ=0 EndX=103.25 EndY=161.1 EndZ=0
    g19: ArcOfCircle CenterX=119 CenterY=155.1 CenterZ=0 NormalX=0 NormalY=0 NormalZ=1 AngleXU=0 Radius=1 StartAngle=1.5708 EndAngle=3.14159
    g20: LineSegment StartX=118 StartY=155.1 StartZ=0 EndX=118 EndY=154.1 EndZ=0
    g21: Circle CenterX=84.5 CenterY=152.05 CenterZ=0 NormalX=0 NormalY=0 NormalZ=1 AngleXU=0 Radius=1.5
    g22: LineSegment StartX=133 StartY=143 StartZ=0 EndX=123 EndY=143 EndZ=0
    g23: LineSegment StartX=73 StartY=143 StartZ=0 EndX=83 EndY=143 EndZ=0
    g24: LineSegment StartX=83 StartY=143 StartZ=0 EndX=83 EndY=146 EndZ=0
    g25: LineSegment StartX=83 StartY=146 StartZ=0 EndX=93 EndY=146 EndZ=0
    g26: LineSegment StartX=93 StartY=146 StartZ=0 EndX=93 EndY=143 EndZ=0
    g27: LineSegment StartX=93 StartY=143 StartZ=0 EndX=102.75 EndY=143 EndZ=0
    g28: Circle CenterX=108 CenterY=144.5 CenterZ=0 NormalX=0 NormalY=0 NormalZ=1 AngleXU=0 Radius=1
    g29: LineSegment StartX=113 StartY=143 StartZ=0 EndX=110.598 EndY=143 EndZ=0
    g30: ArcOfCircle CenterX=108 CenterY=144.5 CenterZ=0 NormalX=0 NormalY=0 NormalZ=1 AngleXU=0 Radius=3 StartAngle=3.66519 EndAngle=5.75959
    g31: LineSegment StartX=105.402 StartY=143 StartZ=0 EndX=103.25 EndY=143 EndZ=0
  constraints (91):
    c: Horizontal(g0)
    c: Radius(g1) = 1
    c: Horizontal(g1,g1)
    c: Vertical(g2)
    c: Tangent(g2,g1) = 1.5708
    c: Vertical(g3)
    c: Coincident(g3,g4)
    c: Horizontal(g4)
    c: Coincident(g4,g5)
    c: Vertical(g5)
    c: Vertical(g6)
    c: Horizontal(g8)
    c: Tangent(g8,g9) = -1.5708
    c: Radius(g9) = 1
    c: Radius(g7) = 1
    c: DistanceX(g8,g8) = 8
    c: Tangent(g7,g8) = -1.5708
    c: Tangent(g10,g6) = 1.5708
    c: Radius(g10) = 1
    c: Horizontal(g11)
    c: DistanceX(g6,g2) = 60
    c: DistanceY(g3,g3) = 3
    c: DistanceY(g5,g5) = 3
    c: DistanceY(g2,g1) = 18.1
    c: Tangent(g0,g10) = -1.5708
    c: Horizontal(g12)
    c: Tangent(g12,g13) = -1.5708
    c: Vertical(g14)
    c: Tangent(g14,g9) = 1.5708
    c: Tangent(g13,g14) = -1.5708
    c: Tangent(g1,g12) = -1.5708
    c: Tangent(g11,g15) = -1.5708
    c: Vertical(g16)
    c: Tangent(g16,g17) = -1.5708
    c: Horizontal(g18)
    c: DistanceX(g0,g18) = 0.5
    c: Tangent(g11,g19) = 1.5708
    c: Vertical(g20)
    c: Tangent(g19,g20) = -1.5708
    c: DistanceY(g20,g20) = 1
    c: Tangent(g20,g7) = -1.5708
    c: Radius(g19) = 1
    c: Tangent(g15,g16) = -1.5708
    c: Radius(g15) = 1
    c: DistanceY(g16,g16) = 3
    c: Radius(g17) = 1
    c: DistanceX(g12,g12) = 3
    c: Tangent(g17,g18) = -1.5708
    c: Horizontal(g18,g0)
    c: Horizontal(g17,g12)
    c: Radius(g13) = 1
    c: DistanceX(g16,g13) = 3
    c: Radius(g21) = 1.5
    c: DistanceX(g6,g21) = 11.5
    c: DistanceY(g21,g0) = 9.05
    c: DistanceX(g4,g4) = 10
    c: DistanceX(g5,g2) = 10
    c: Coincident(g2,g22)
    c: Horizontal(g22)
    c: Coincident(g5,g22)
    c: Coincident(g6,g23)
    c: Horizontal(g23)
    c: Coincident(g23,g24)
    c: Vertical(g24)
    c: Coincident(g24,g25)
    c: Horizontal(g25)
    c: Coincident(g25,g26)
    c: Vertical(g26)
    c: Coincident(g26,g27)
    c: Horizontal(g27)
    c: DistanceX(g23,g23) = 10
    c: DistanceX(g25,g25) = 10
    c: DistanceY(g24,g24) = 3
    c: DistanceY(g26,g26) = 3
    c: DistanceX(g27,g27) = 9.75
    c: Vertical(g0,g27)
    c: Radius(g28) = 1
    c: DistanceY(g6,g28) = 1.5
    c: DistanceX(g28,g2) = 25
    c: DistanceX(g6) = 73
    c: DistanceY(g6) = 143
    c: Coincident(g3,g29)
    c: Horizontal(g29)
    c: Coincident(g30,g31)
    c: Horizontal(g31)
    c: Horizontal(g27,g31)
    c: DistanceX(g27,g31) = 0.5
    c: DistanceY(g6,g0) = 18.1
    c: Coincident(g28,g30)
    c: Coincident(g29,g30)
    c: Radius(g30) = 3
FEATURE [Sketcher::SketchObject] Sketch112
  MapMode = 5
  Support = -> [XY_Plane]
  sketch-geometry (25):
    g0: ArcOfCircle CenterX=169 CenterY=63 CenterZ=0 NormalX=0 NormalY=0 NormalZ=1 AngleXU=0 Radius=2 StartAngle=1.5708 EndAngle=3.14159
    g1: LineSegment StartX=169 StartY=65 StartZ=0 EndX=185.1 EndY=65 EndZ=0
    g2: LineSegment StartX=170 StartY=59 StartZ=0 EndX=182.1 EndY=59 EndZ=0
    g3: LineSegment StartX=182.1 StartY=59 StartZ=0 EndX=182.1 EndY=55 EndZ=0
    g4: LineSegment StartX=182.1 StartY=36.5 StartZ=0 EndX=170 EndY=36.5 EndZ=0
    g5: Circle CenterX=176.05 CenterY=61.5 CenterZ=0 NormalX=0 NormalY=0 NormalZ=1 AngleXU=0 Radius=1
    g6: Circle CenterX=176.05 CenterY=34 CenterZ=0 NormalX=0 NormalY=0 NormalZ=1 AngleXU=0 Radius=1
    g7: LineSegment StartX=182.1 StartY=55 StartZ=0 EndX=185.1 EndY=55 EndZ=0
    g8: LineSegment StartX=185.1 StartY=55 StartZ=0 EndX=185.1 EndY=65 EndZ=0
    g9: ArcOfCircle CenterX=169 CenterY=7 CenterZ=0 NormalX=0 NormalY=0 NormalZ=1 AngleXU=0 Radius=2 StartAngle=3.14159 EndAngle=4.71239
    g10: LineSegment StartX=169 StartY=5 StartZ=0 EndX=185.1 EndY=5 EndZ=0
    g11: LineSegment StartX=185.1 StartY=45 StartZ=0 EndX=182.1 EndY=45 EndZ=0
    g12: LineSegment StartX=182.1 StartY=45 StartZ=0 EndX=182.1 EndY=36.5 EndZ=0
    g13: LineSegment StartX=167 StartY=63 StartZ=0 EndX=167 EndY=35.25 EndZ=0
    g14: LineSegment StartX=167 StartY=7 StartZ=0 EndX=167 EndY=34.75 EndZ=0
    g15: LineSegment StartX=170 StartY=36.5 StartZ=0 EndX=170 EndY=59 EndZ=0
    g16: LineSegment StartX=185.1 StartY=25 StartZ=0 EndX=182.1 EndY=25 EndZ=0
    g17: LineSegment StartX=182.1 StartY=25 StartZ=0 EndX=182.1 EndY=15 EndZ=0
    g18: LineSegment StartX=182.1 StartY=15 StartZ=0 EndX=185.1 EndY=15 EndZ=0
    g19: LineSegment StartX=185.1 StartY=15 StartZ=0 EndX=185.1 EndY=5 EndZ=0
    g20: Circle CenterX=183.6 CenterY=30 CenterZ=0 NormalX=0 NormalY=0 NormalZ=1 AngleXU=0 Radius=1
    g21: LineSegment StartX=185.1 StartY=45 StartZ=0 EndX=185.1 EndY=35.25 EndZ=0
    g22: LineSegment StartX=185.1 StartY=25 StartZ=0 EndX=185.1 EndY=27.4019 EndZ=0
    g23: ArcOfCircle CenterX=183.6 CenterY=30 CenterZ=0 NormalX=0 NormalY=0 NormalZ=1 AngleXU=0 Radius=3 StartAngle=5.23599 EndAngle=7.33038
    g24: LineSegment StartX=185.1 StartY=32.5981 StartZ=0 EndX=185.1 EndY=34.75 EndZ=0
  constraints (75):
    c: Horizontal(g1)
    c: Tangent(g0,g1) = 1.5708
    c: Radius(g0) = 2
    c: Coincident(g2,g3)
    c: Coincident(g12,g4)
    c: Horizontal(g2)
    c: Horizontal(g4)
    c: Vertical(g3)
    c: DistanceX(g4,g4) = 12.1
    c: DistanceY(g4,g2) = 22.5
    c: DistanceY(g2,g0) = 6
    c: Radius(g6) = 1
    c: Radius(g5) = 1
    c: DistanceY(g2,g5) = 2.5
    c: DistanceY(g6,g4) = 2.5
    c: DistanceX(g4,g6) = 6.05
    c: DistanceX(g2,g5) = 6.05
    c: Horizontal(g7)
    c: Coincident(g7,g8)
    c: Vertical(g8)
    c: DistanceX(g7,g7) = 3
    c: Coincident(g1,g8)
    c: Horizontal(g10)
    c: Horizontal(g11)
    c: PointOnObject(g3,g7)
    c: Coincident(g12,g11)
    c: Tangent(g3,g12)
    c: DistanceX(g11,g11) = 3
    c: Tangent(g9,g10) = -1.5708
    c: Radius(g9) = 2
    c: DistanceY(g11,g3) = 10
    c: Coincident(g3,g7)
    c: DistanceY(g7,g1) = 10
    c: DistanceY(g10,g1) = 60
    c: Vertical(g13)
    c: Vertical(g14)
    c: Coincident(g15,g4)
    c: Vertical(g15)
    c: Vertical(g13,g14)
    c: DistanceY(g14,g13) = 0.5
    c: Tangent(g13,g0) = -1.5708
    c: Tangent(g14,g9) = 1.5708
    c: Equal(g14,g13)
    c: DistanceX(g9,g4) = 3
    c: DistanceX(g9) = 169
    c: DistanceY(g9) = 5
    c: Horizontal(g16)
    c: Coincident(g16,g17)
    c: Vertical(g17)
    c: Coincident(g17,g18)
    c: Horizontal(g18)
    c: Coincident(g18,g19)
    c: Coincident(g19,g10)
    c: Vertical(g19)
    c: DistanceY(g19,g19) = 10
    c: DistanceY(g17,g17) = 10
    c: DistanceX(g18,g18) = 3
    c: DistanceX(g16,g16) = 3
    c: Radius(g20) = 1
    c: DistanceY(g10,g20) = 25
    c: DistanceX(g20,g10) = 1.5
    c: Coincident(g2,g15)
    c: Coincident(g21,g11)
    c: Vertical(g21)
    c: Coincident(g16,g22)
    c: Vertical(g22)
    c: Coincident(g23,g24)
    c: Vertical(g24)
    c: Vertical(g21,g24)
    c: DistanceY(g24,g21) = 0.5
    c: Coincident(g20,g23)
    c: Coincident(g22,g23)
    c: Radius(g23) = 3
    c: Horizontal(g14,g24)
    c: Vertical(g22,g23)
FEATURE [Sketcher::SketchObject] Sketch116
  MapMode = 5
  Support = -> [XY_Plane]
  sketch-geometry (10):
    g0: LineSegment StartX=80 StartY=76 StartZ=0 EndX=109 EndY=76 EndZ=0
    g1: LineSegment StartX=109 StartY=94 StartZ=0 EndX=80 EndY=94 EndZ=0
    g2: LineSegment StartX=88.2606 StartY=88.39 StartZ=0 EndX=102.526 EndY=87.2932 EndZ=0
    g3: ArcOfCircle CenterX=102.35 CenterY=85 CenterZ=0 NormalX=0 NormalY=0 NormalZ=1 AngleXU=0 Radius=2.3 StartAngle=4.78912 EndAngle=7.77725
    g4: LineSegment StartX=102.526 StartY=82.7068 StartZ=0 EndX=88.2606 EndY=81.61 EndZ=0
    g5: ArcOfCircle CenterX=88 CenterY=85 CenterZ=0 NormalX=0 NormalY=0 NormalZ=1 AngleXU=0 Radius=3.4 StartAngle=1.49407 EndAngle=4.78912
    g6: LineSegment StartX=80 StartY=94 StartZ=0 EndX=80 EndY=85.25 EndZ=0
    g7: LineSegment StartX=80 StartY=76 StartZ=0 EndX=80 EndY=84.75 EndZ=0
    g8: LineSegment StartX=109 StartY=94 StartZ=0 EndX=109 EndY=85.25 EndZ=0
    g9: LineSegment StartX=109 StartY=76 StartZ=0 EndX=109 EndY=84.75 EndZ=0
  constraints (32):
    c: Horizontal(g0)
    c: Horizontal(g1)
    c: DistanceX(g1,g1) = 29
    c: Tangent(g2,g3) = 1.5708
    c: Tangent(g4,g5) = 1.5708
    c: Radius(g5) = 3.4
    c: DistanceX(g5,g0) = 21
    c: Horizontal(g3,g5)
    c: DistanceX(g5,g3) = 14.35
    c: Radius(g3) = 2.3
    c: Tangent(g5,g2) = 1.5708
    c: Tangent(g3,g4) = 1.5708
    c: DistanceY(g0,g5) = 9
    c: Vertical(g6)
    c: Vertical(g7)
    c: DistanceY(g7,g6) = 0.5
    c: Vertical(g6,g7)
    c: Equal(g6,g7)
    c: Coincident(g8,g1)
    c: Vertical(g8)
    c: Coincident(g9,g0)
    c: Vertical(g9)
    c: Vertical(g8,g9)
    c: DistanceY(g9,g8) = 0.5
    c: Equal(g8,g9)
    c: DistanceX(g3,g0) = 6.65
    c: Coincident(g0,g7)
    c: Coincident(g1,g6)
    c: DistanceY(g0,g1) = 18
    c: DistanceX(g0) = 80
    c: DistanceY(g0) = 76
    c: DistanceX(g0,g5) = 8
FEATURE [Sketcher::SketchObject] Sketch117
  MapMode = 5
  Support = -> [XY_Plane]
  sketch-geometry (10):
    g0: LineSegment StartX=80 StartY=114 StartZ=0 EndX=109 EndY=114 EndZ=0
    g1: LineSegment StartX=109 StartY=132 StartZ=0 EndX=80 EndY=132 EndZ=0
    g2: LineSegment StartX=88.2606 StartY=126.39 StartZ=0 EndX=102.526 EndY=125.293 EndZ=0
    g3: ArcOfCircle CenterX=102.35 CenterY=123 CenterZ=0 NormalX=0 NormalY=0 NormalZ=1 AngleXU=0 Radius=2.3 StartAngle=4.78912 EndAngle=7.77725
    g4: LineSegment StartX=102.526 StartY=120.707 StartZ=0 EndX=88.2606 EndY=119.61 EndZ=0
    g5: ArcOfCircle CenterX=88 CenterY=123 CenterZ=0 NormalX=0 NormalY=0 NormalZ=1 AngleXU=0 Radius=3.4 StartAngle=1.49407 EndAngle=4.78912
    g6: LineSegment StartX=80 StartY=132 StartZ=0 EndX=80 EndY=123.25 EndZ=0
    g7: LineSegment StartX=80 StartY=114 StartZ=0 EndX=80 EndY=122.75 EndZ=0
    g8: LineSegment StartX=109 StartY=132 StartZ=0 EndX=109 EndY=123.25 EndZ=0
    g9: LineSegment StartX=109 StartY=114 StartZ=0 EndX=109 EndY=122.75 EndZ=0
  constraints (32):
    c: Horizontal(g0)
    c: Horizontal(g1)
    c: DistanceX(g1,g1) = 29
    c: Tangent(g2,g3) = 1.5708
    c: Tangent(g4,g5) = 1.5708
    c: Radius(g5) = 3.4
    c: DistanceX(g5,g0) = 21
    c: Horizontal(g3,g5)
    c: DistanceX(g5,g3) = 14.35
    c: Radius(g3) = 2.3
    c: Tangent(g5,g2) = 1.5708
    c: Tangent(g3,g4) = 1.5708
    c: DistanceY(g0,g5) = 9
    c: Vertical(g6)
    c: Vertical(g7)
    c: DistanceY(g7,g6) = 0.5
    c: Vertical(g6,g7)
    c: Equal(g6,g7)
    c: Coincident(g8,g1)
    c: Vertical(g8)
    c: Coincident(g9,g0)
    c: Vertical(g9)
    c: Vertical(g8,g9)
    c: DistanceY(g9,g8) = 0.5
    c: Equal(g8,g9)
    c: DistanceX(g3,g0) = 6.65
    c: Coincident(g0,g7)
    c: Coincident(g1,g6)
    c: DistanceY(g0,g1) = 18
    c: DistanceX(g0) = 80
    c: DistanceY(g0) = 114
    c: DistanceX(g0,g5) = 8
FEATURE [Sketcher::SketchObject] Sketch124
  MapMode = 5
  Support = -> [XY_Plane]
  sketch-geometry (35):
    g0: LineSegment [constr] StartX=163 StartY=158 StartZ=0 EndX=181 EndY=158 EndZ=0
    g1: LineSegment StartX=163 StartY=143 StartZ=0 EndX=167 EndY=143 EndZ=0
    g2: LineSegment StartX=181 StartY=143 StartZ=0 EndX=177 EndY=143 EndZ=0
    g3: LineSegment StartX=167 StartY=143 StartZ=0 EndX=167 EndY=146 EndZ=0
    g4: LineSegment StartX=167 StartY=146 StartZ=0 EndX=170.5 EndY=146 EndZ=0
    g5: LineSegment StartX=170.5 StartY=146 StartZ=0 EndX=170.5 EndY=150 EndZ=0
    g6: LineSegment StartX=170.5 StartY=150 StartZ=0 EndX=169.2 EndY=150 EndZ=0
    g7: LineSegment StartX=169.2 StartY=150 StartZ=0 EndX=169.2 EndY=152.5 EndZ=0
    g8: LineSegment StartX=169.2 StartY=152.5 StartZ=0 EndX=170.5 EndY=152.5 EndZ=0
    g9: LineSegment StartX=170.5 StartY=152.5 StartZ=0 EndX=170.5 EndY=154 EndZ=0
    g10: LineSegment StartX=170.5 StartY=154 StartZ=0 EndX=173.5 EndY=154 EndZ=0
    g11: LineSegment StartX=173.5 StartY=154 StartZ=0 EndX=173.5 EndY=152.5 EndZ=0
    g12: LineSegment StartX=173.5 StartY=152.5 StartZ=0 EndX=174.8 EndY=152.5 EndZ=0
    g13: LineSegment StartX=174.8 StartY=152.5 StartZ=0 EndX=174.8 EndY=150 EndZ=0
    g14: LineSegment StartX=174.8 StartY=150 StartZ=0 EndX=173.5 EndY=150 EndZ=0
    g15: LineSegment StartX=173.5 StartY=150 StartZ=0 EndX=173.5 EndY=146 EndZ=0
    g16: LineSegment StartX=173.5 StartY=146 StartZ=0 EndX=177 EndY=146 EndZ=0
    g17: LineSegment StartX=177 StartY=146 StartZ=0 EndX=177 EndY=143 EndZ=0
    g18: LineSegment StartX=181 StartY=188 StartZ=0 EndX=181 EndY=178.5 EndZ=0
    g19: ArcOfCircle CenterX=165 CenterY=188 CenterZ=0 NormalX=0 NormalY=0 NormalZ=1 AngleXU=0 Radius=2 StartAngle=1.5708 EndAngle=3.14159
    g20: LineSegment StartX=165 StartY=190 StartZ=0 EndX=179 EndY=190 EndZ=0
    g21: ArcOfCircle CenterX=179 CenterY=188 CenterZ=0 NormalX=0 NormalY=0 NormalZ=1 AngleXU=0 Radius=2 StartAngle=0 EndAngle=1.5708
    g22: LineSegment StartX=165.95 StartY=185 StartZ=0 EndX=178.05 EndY=185 EndZ=0
    g23: LineSegment StartX=178.05 StartY=185 StartZ=0 EndX=178.05 EndY=162.5 EndZ=0
    g24: LineSegment StartX=178.05 StartY=162.5 StartZ=0 EndX=165.95 EndY=162.5 EndZ=0
    g25: LineSegment StartX=165.95 StartY=162.5 StartZ=0 EndX=165.95 EndY=185 EndZ=0
    g26: Circle CenterX=172 CenterY=187.5 CenterZ=0 NormalX=0 NormalY=0 NormalZ=1 AngleXU=0 Radius=1
    g27: Circle CenterX=172 CenterY=160 CenterZ=0 NormalX=0 NormalY=0 NormalZ=1 AngleXU=0 Radius=1
    g28: LineSegment StartX=181 StartY=178 StartZ=0 EndX=181 EndY=168 EndZ=0
    g29: LineSegment StartX=181 StartY=168 StartZ=0 EndX=184 EndY=168 EndZ=0
    g30: LineSegment StartX=184 StartY=168 StartZ=0 EndX=184 EndY=163 EndZ=0
    g31: LineSegment StartX=184 StartY=163 StartZ=0 EndX=181 EndY=163 EndZ=0
    g32: LineSegment StartX=181 StartY=163 StartZ=0 EndX=181 EndY=143 EndZ=0
    g33: LineSegment StartX=163 StartY=188 StartZ=0 EndX=163 EndY=178.5 EndZ=0
    g34: LineSegment StartX=163 StartY=178 StartZ=0 EndX=163 EndY=143 EndZ=0
  constraints (109):
    c: Horizontal(g0)
    c: DistanceY(g1,g0) = 15
    c: DistanceX(g0,g0) = 18
    c: Horizontal(g2,g1)
    c: Horizontal(g1)
    c: Horizontal(g2)
    c: Coincident(g1,g3)
    c: Vertical(g3)
    c: Coincident(g3,g4)
    c: Horizontal(g4)
    c: Coincident(g4,g5)
    c: Vertical(g5)
    c: Coincident(g5,g6)
    c: Horizontal(g6)
    c: Coincident(g6,g7)
    c: Vertical(g7)
    c: Coincident(g7,g8)
    c: Horizontal(g8)
    c: Coincident(g8,g9)
    c: Coincident(g9,g10)
    c: Horizontal(g10)
    c: Coincident(g10,g11)
    c: Vertical(g11)
    c: Coincident(g11,g12)
    c: Horizontal(g12)
    c: Coincident(g12,g13)
    c: Vertical(g13)
    c: Coincident(g13,g14)
    c: Horizontal(g14)
    c: Coincident(g14,g15)
    c: Vertical(g15)
    c: Coincident(g15,g16)
    c: Horizontal(g16)
    c: Coincident(g16,g17)
    c: Coincident(g17,g2)
    c: Vertical(g17)
    c: Vertical(g9)
    c: DistanceX(g1,g1) = 4
    c: DistanceX(g2,g2) = 4
    c: Horizontal(g3,g16)
    c: DistanceY(g3,g3) = 3
    c: Horizontal(g5,g14)
    c: Horizontal(g8,g11)
    c: DistanceX(g4,g4) = 3.5
    c: DistanceX(g16,g16) = 3.5
    c: DistanceY(g5,g5) = 4
    c: Vertical(g8,g5)
    c: Vertical(g11,g14)
    c: DistanceY(g7,g7) = 2.5
    c: DistanceX(g4,g15) = 3
    c: DistanceX(g6,g6) = 1.3
    c: DistanceX(g14,g14) = 1.3
    c: DistanceY(g9,g9) = 1.5
    c: Vertical(g18)
    c: Vertical(g0,g18)
    c: Vertical(g18,g28)
    c: DistanceY(g28,g18) = 0.5
    c: Horizontal(g20)
    c: Tangent(g20,g21) = 1.5708
    c: Tangent(g19,g20) = 1.5708
    c: Radius(g19) = 2
    c: Radius(g21) = 2
    c: Tangent(g21,g18) = 1.5708
    c: Coincident(g22,g23)
    c: Coincident(g23,g24)
    c: Coincident(g24,g25)
    c: Coincident(g25,g22)
    c: Horizontal(g22)
    c: Horizontal(g24)
    c: Vertical(g23)
    c: Vertical(g25)
    c: DistanceX(g24,g24) = 12.1
    c: DistanceY(g25,g25) = 22.5
    c: DistanceY(g3,g24) = 16.5
    c: DistanceX(g1,g24) = 2.95
    c: DistanceY(g22,g19) = 5
    c: Radius(g27) = 1
    c: Radius(g26) = 1
    c: DistanceY(g22,g26) = 2.5
    c: DistanceY(g27,g24) = 2.5
    c: DistanceX(g24,g27) = 6.05
    c: DistanceX(g22,g26) = 6.05
    c: DistanceY(g9,g27) = 6
    c: DistanceY(g1,g19) = 47
    c: Vertical(g34,g33)
    c: DistanceY(g34,g33) = 0.5
    c: Horizontal(g34,g28)
    c: DistanceX(g10,g10) = 3
    c: DistanceX(g1) = 163
    c: DistanceY(g1) = 143
    c: Vertical(g28)
    c: Coincident(g28,g29)
    c: Horizontal(g29)
    c: Coincident(g29,g30)
    c: Vertical(g30)
    c: Coincident(g30,g31)
    c: Horizontal(g31)
    c: Coincident(g31,g32)
    c: Coincident(g32,g2)
    c: Vertical(g32)
    c: DistanceX(g29,g29) = 3
    c: DistanceX(g31,g31) = 3
    c: DistanceY(g30,g30) = 5
    c: DistanceY(g2,g31) = 20
    c: DistanceY(g28,g28) = 10
    c: Vertical(g33)
    c: Tangent(g19,g33) = -1.5708
    c: Vertical(g34)
    c: Coincident(g1,g34)
FEATURE [Sketcher::SketchObject] Sketch125
  MapMode = 5
  Support = -> [XY_Plane]
  sketch-geometry (30):
    g0: LineSegment [constr] StartX=163 StartY=206 StartZ=0 EndX=181 EndY=206 EndZ=0
    g1: LineSegment StartX=163 StartY=191 StartZ=0 EndX=167 EndY=191 EndZ=0
    g2: LineSegment StartX=181 StartY=191 StartZ=0 EndX=177 EndY=191 EndZ=0
    g3: LineSegment StartX=167 StartY=191 StartZ=0 EndX=167 EndY=194 EndZ=0
    g4: LineSegment StartX=167 StartY=194 StartZ=0 EndX=170.5 EndY=194 EndZ=0
    g5: LineSegment StartX=170.5 StartY=194 StartZ=0 EndX=170.5 EndY=198 EndZ=0
    g6: LineSegment StartX=170.5 StartY=198 StartZ=0 EndX=169.2 EndY=198 EndZ=0
    g7: LineSegment StartX=169.2 StartY=198 StartZ=0 EndX=169.2 EndY=200.5 EndZ=0
    g8: LineSegment StartX=169.2 StartY=200.5 StartZ=0 EndX=170.5 EndY=200.5 EndZ=0
    g9: LineSegment StartX=170.5 StartY=200.5 StartZ=0 EndX=170.5 EndY=202 EndZ=0
    g10: LineSegment StartX=170.5 StartY=202 StartZ=0 EndX=173.5 EndY=202 EndZ=0
    g11: LineSegment StartX=173.5 StartY=202 StartZ=0 EndX=173.5 EndY=200.5 EndZ=0
    g12: LineSegment StartX=173.5 StartY=200.5 StartZ=0 EndX=174.8 EndY=200.5 EndZ=0
    g13: LineSegment StartX=174.8 StartY=200.5 StartZ=0 EndX=174.8 EndY=198 EndZ=0
    g14: LineSegment StartX=174.8 StartY=198 StartZ=0 EndX=173.5 EndY=198 EndZ=0
    g15: LineSegment StartX=173.5 StartY=198 StartZ=0 EndX=173.5 EndY=194 EndZ=0
    g16: LineSegment StartX=173.5 StartY=194 StartZ=0 EndX=177 EndY=194 EndZ=0
    g17: LineSegment StartX=177 StartY=194 StartZ=0 EndX=177 EndY=191 EndZ=0
    g18: LineSegment StartX=181 StartY=231 StartZ=0 EndX=181 EndY=226.5 EndZ=0
    g19: ArcOfCircle CenterX=165 CenterY=231 CenterZ=0 NormalX=0 NormalY=0 NormalZ=1 AngleXU=0 Radius=2 StartAngle=1.5708 EndAngle=3.14159
    g20: LineSegment StartX=165 StartY=233 StartZ=0 EndX=179 EndY=233 EndZ=0
    g21: ArcOfCircle CenterX=179 CenterY=231 CenterZ=0 NormalX=0 NormalY=0 NormalZ=1 AngleXU=0 Radius=2 StartAngle=-1e-12 EndAngle=1.5708
    g22: Circle CenterX=172 CenterY=227 CenterZ=0 NormalX=0 NormalY=0 NormalZ=1 AngleXU=0 Radius=1.5
    g23: LineSegment StartX=181 StartY=226 StartZ=0 EndX=181 EndY=216 EndZ=0
    g24: LineSegment StartX=181 StartY=216 StartZ=0 EndX=184 EndY=216 EndZ=0
    g25: LineSegment StartX=184 StartY=216 StartZ=0 EndX=184 EndY=211 EndZ=0
    g26: LineSegment StartX=184 StartY=211 StartZ=0 EndX=181 EndY=211 EndZ=0
    g27: LineSegment StartX=181 StartY=211 StartZ=0 EndX=181 EndY=191 EndZ=0
    g28: LineSegment StartX=163 StartY=231 StartZ=0 EndX=163 EndY=226.5 EndZ=0
    g29: LineSegment StartX=163 StartY=226 StartZ=0 EndX=163 EndY=191 EndZ=0
  constraints (94):
    c: Horizontal(g0)
    c: DistanceY(g1,g0) = 15
    c: DistanceX(g0,g0) = 18
    c: Horizontal(g2,g1)
    c: Horizontal(g1)
    c: Horizontal(g2)
    c: Coincident(g1,g3)
    c: Vertical(g3)
    c: Coincident(g3,g4)
    c: Horizontal(g4)
    c: Coincident(g4,g5)
    c: Vertical(g5)
    c: Coincident(g5,g6)
    c: Horizontal(g6)
    c: Coincident(g6,g7)
    c: Vertical(g7)
    c: Coincident(g7,g8)
    c: Horizontal(g8)
    c: Coincident(g8,g9)
    c: Coincident(g9,g10)
    c: Horizontal(g10)
    c: Coincident(g10,g11)
    c: Vertical(g11)
    c: Coincident(g11,g12)
    c: Horizontal(g12)
    c: Coincident(g12,g13)
    c: Vertical(g13)
    c: Coincident(g13,g14)
    c: Horizontal(g14)
    c: Coincident(g14,g15)
    c: Vertical(g15)
    c: Coincident(g15,g16)
    c: Horizontal(g16)
    c: Coincident(g16,g17)
    c: Coincident(g17,g2)
    c: Vertical(g17)
    c: Vertical(g9)
    c: DistanceX(g1,g1) = 4
    c: DistanceX(g2,g2) = 4
    c: Horizontal(g3,g16)
    c: DistanceY(g3,g3) = 3
    c: Horizontal(g5,g14)
    c: Horizontal(g8,g11)
    c: DistanceX(g4,g4) = 3.5
    c: DistanceX(g16,g16) = 3.5
    c: DistanceY(g5,g5) = 4
    c: Vertical(g8,g5)
    c: Vertical(g11,g14)
    c: DistanceY(g7,g7) = 2.5
    c: DistanceX(g4,g15) = 3
    c: DistanceX(g6,g6) = 1.3
    c: DistanceX(g14,g14) = 1.3
    c: DistanceY(g9,g9) = 1.5
    c: Vertical(g18)
    c: Vertical(g0,g18)
    c: Vertical(g18,g23)
    c: DistanceY(g23,g18) = 0.5
    c: Horizontal(g20)
    c: Tangent(g20,g21) = 1.5708
    c: Tangent(g19,g20) = 1.5708
    c: Radius(g19) = 2
    c: Radius(g21) = 2
    c: Tangent(g21,g18) = 1.5708
    c: Radius(g22) = 1.5
    c: DistanceY(g22,g19) = 6
    c: DistanceX(g1,g22) = 9
    c: DistanceY(g1,g19) = 42
    c: Distance(g22,g19) = 9.21954
    c: Distance(g19,g22) = 8.06226
    c: Vertical(g29,g28)
    c: DistanceY(g29,g28) = 0.5
    c: Horizontal(g29,g23)
    c: DistanceX(g10,g10) = 3
    c: DistanceX(g1) = 163
    c: DistanceY(g1) = 191
    c: Vertical(g23)
    c: Coincident(g23,g24)
    c: Horizontal(g24)
    c: Coincident(g24,g25)
    c: Vertical(g25)
    c: Coincident(g25,g26)
    c: Horizontal(g26)
    c: Coincident(g26,g27)
    c: Coincident(g27,g2)
    c: Vertical(g27)
    c: DistanceX(g26,g26) = 3
    c: DistanceX(g24,g24) = 3
    c: DistanceY(g25,g25) = 5
    c: DistanceY(g2,g26) = 20
    c: DistanceY(g23,g23) = 10
    c: Vertical(g28)
    c: Tangent(g19,g28) = -1.5708
    c: Vertical(g29)
    c: Coincident(g1,g29)
FEATURE [Sketcher::SketchObject] Sketch128
  MapMode = 5
  Support = -> [XY_Plane]
  sketch-geometry (46):
    g0: LineSegment StartX=8 StartY=197 StartZ=0 EndX=8 EndY=211 EndZ=0
    g1: LineSegment StartX=8 StartY=211 StartZ=0 EndX=5 EndY=211 EndZ=0
    g2: LineSegment StartX=5 StartY=211 StartZ=0 EndX=5 EndY=221 EndZ=0
    g3: LineSegment StartX=5 StartY=221 StartZ=0 EndX=8 EndY=221 EndZ=0
    g4: LineSegment StartX=35 StartY=221 StartZ=0 EndX=38 EndY=221 EndZ=0
    g5: LineSegment StartX=38 StartY=221 StartZ=0 EndX=38 EndY=211 EndZ=0
    g6: LineSegment StartX=38 StartY=211 StartZ=0 EndX=35 EndY=211 EndZ=0
    g7: LineSegment StartX=35 StartY=211 StartZ=0 EndX=35 EndY=197 EndZ=0
    g8: LineSegment StartX=8 StartY=191 StartZ=0 EndX=5 EndY=191 EndZ=0
    g9: LineSegment StartX=5 StartY=191 StartZ=0 EndX=5 EndY=181 EndZ=0
    g10: LineSegment StartX=5 StartY=181 StartZ=0 EndX=8 EndY=181 EndZ=0
    g11: LineSegment StartX=35 StartY=181 StartZ=0 EndX=38 EndY=181 EndZ=0
    g12: LineSegment StartX=38 StartY=181 StartZ=0 EndX=38 EndY=191 EndZ=0
    g13: LineSegment StartX=38 StartY=191 StartZ=0 EndX=35 EndY=191 EndZ=0
    g14: LineSegment StartX=35 StartY=231 StartZ=0 EndX=35 EndY=221 EndZ=0
    g15: LineSegment StartX=35 StartY=181 StartZ=0 EndX=35 EndY=171 EndZ=0
    g16: LineSegment StartX=8 StartY=231 StartZ=0 EndX=8 EndY=221 EndZ=0
    g17: LineSegment StartX=8 StartY=181 StartZ=0 EndX=8 EndY=171 EndZ=0
    g18: LineSegment StartX=8 StartY=191 StartZ=0 EndX=8 EndY=195 EndZ=0
    g19: LineSegment StartX=8 StartY=195 StartZ=0 EndX=11.5 EndY=195 EndZ=0
    g20: LineSegment StartX=11.5 StartY=195 StartZ=0 EndX=11.5 EndY=194 EndZ=0
    g21: LineSegment StartX=11.5 StartY=194 StartZ=0 EndX=13 EndY=194 EndZ=0
    g22: LineSegment StartX=13 StartY=194 StartZ=0 EndX=13 EndY=195 EndZ=0
    g23: LineSegment StartX=13 StartY=195 StartZ=0 EndX=13.5 EndY=195 EndZ=0
    g24: LineSegment StartX=13.5 StartY=195 StartZ=0 EndX=13.5 EndY=197 EndZ=0
    g25: LineSegment StartX=13.5 StartY=197 StartZ=0 EndX=13 EndY=197 EndZ=0
    g26: LineSegment StartX=13 StartY=197 StartZ=0 EndX=13 EndY=198 EndZ=0
    g27: LineSegment StartX=13 StartY=198 StartZ=0 EndX=11.5 EndY=198 EndZ=0
    g28: LineSegment StartX=11.5 StartY=198 StartZ=0 EndX=11.5 EndY=197 EndZ=0
    g29: LineSegment StartX=11.5 StartY=197 StartZ=0 EndX=8 EndY=197 EndZ=0
    g30: LineSegment StartX=35 StartY=191 StartZ=0 EndX=35 EndY=195 EndZ=0
    g31: LineSegment StartX=35 StartY=195 StartZ=0 EndX=31.5 EndY=195 EndZ=0
    g32: LineSegment StartX=31.5 StartY=195 StartZ=0 EndX=31.5 EndY=194 EndZ=0
    g33: LineSegment StartX=31.5 StartY=194 StartZ=0 EndX=30 EndY=194 EndZ=0
    g34: LineSegment StartX=30 StartY=194 StartZ=0 EndX=30 EndY=195 EndZ=0
    g35: LineSegment StartX=30 StartY=195 StartZ=0 EndX=29.5 EndY=195 EndZ=0
    g36: LineSegment StartX=29.5 StartY=195 StartZ=0 EndX=29.5 EndY=197 EndZ=0
    g37: LineSegment StartX=29.5 StartY=197 StartZ=0 EndX=30 EndY=197 EndZ=0
    g38: LineSegment StartX=30 StartY=197 StartZ=0 EndX=30 EndY=198 EndZ=0
    g39: LineSegment StartX=30 StartY=198 StartZ=0 EndX=31.5 EndY=198 EndZ=0
    g40: LineSegment StartX=31.5 StartY=198 StartZ=0 EndX=31.5 EndY=197 EndZ=0
    g41: LineSegment StartX=31.5 StartY=197 StartZ=0 EndX=35 EndY=197 EndZ=0
    g42: LineSegment StartX=8 StartY=231 StartZ=0 EndX=21.25 EndY=231 EndZ=0
    g43: LineSegment StartX=35 StartY=231 StartZ=0 EndX=21.75 EndY=231 EndZ=0
    g44: LineSegment StartX=8 StartY=171 StartZ=0 EndX=21.25 EndY=171 EndZ=0
    g45: LineSegment StartX=35 StartY=171 StartZ=0 EndX=21.75 EndY=171 EndZ=0
  constraints (140):
    c: Vertical(g0)
    c: Coincident(g0,g1)
    c: Horizontal(g1)
    c: Coincident(g1,g2)
    c: Vertical(g2)
    c: Coincident(g2,g3)
    c: Horizontal(g3)
    c: Horizontal(g4)
    c: Coincident(g4,g5)
    c: Vertical(g5)
    c: Coincident(g5,g6)
    c: Horizontal(g6)
    c: Coincident(g6,g7)
    c: Vertical(g7)
    c: Horizontal(g8)
    c: Coincident(g8,g9)
    c: Vertical(g9)
    c: Coincident(g9,g10)
    c: Horizontal(g10)
    c: DistanceY(g3,g16) = 10
    c: DistanceY(g2,g2) = 10
    c: DistanceY(g9,g9) = 10
    c: DistanceY(g17,g10) = 10
    c: DistanceX(g16,g14) = 27
    c: DistanceX(g3,g3) = 3
    c: DistanceX(g1,g1) = 3
    c: DistanceX(g8,g8) = 3
    c: DistanceX(g10,g10) = 3
    c: DistanceY(g4,g14) = 10
    c: DistanceY(g5,g5) = 10
    c: DistanceX(g4,g4) = 3
    c: DistanceX(g6,g6) = 3
    c: DistanceX(g17,g15) = 27
    c: Horizontal(g11)
    c: Coincident(g11,g12)
    c: Vertical(g12)
    c: Coincident(g12,g13)
    c: Horizontal(g13)
    c: DistanceY(g15,g11) = 10
    c: DistanceY(g12,g12) = 10
    c: DistanceX(g11,g11) = 3
    c: Coincident(g14,g4)
    c: Vertical(g14)
    c: Coincident(g11,g15)
    c: Vertical(g15)
    c: Coincident(g16,g3)
    c: Vertical(g16)
    c: Coincident(g10,g17)
    c: Vertical(g17)
    c: Coincident(g8,g18)
    c: Vertical(g18)
    c: Coincident(g18,g19)
    c: Horizontal(g19)
    c: Coincident(g19,g20)
    c: Vertical(g20)
    c: Coincident(g20,g21)
    c: Horizontal(g21)
    c: Coincident(g21,g22)
    c: Vertical(g22)
    c: Coincident(g22,g23)
    c: Horizontal(g23)
    c: Coincident(g23,g24)
    c: Vertical(g24)
    c: Coincident(g24,g25)
    c: Horizontal(g25)
    c: Coincident(g25,g26)
    c: Vertical(g26)
    c: Coincident(g26,g27)
    c: Horizontal(g27)
    c: Coincident(g27,g28)
    c: Vertical(g28)
    c: Coincident(g28,g29)
    c: Horizontal(g29)
    c: DistanceY(g18,g18) = 4
    c: DistanceY(g20,g20) = 1
    c: DistanceY(g28,g28) = 1
    c: DistanceY(g26,g26) = 1
    c: DistanceY(g22,g22) = 1
    c: DistanceY(g24,g24) = 2
    c: DistanceX(g27,g27) = 1.5
    c: DistanceX(g21,g21) = 1.5
    c: DistanceX(g29,g29) = 3.5
    c: DistanceX(g25,g25) = 0.5
    c: DistanceX(g19,g19) = 3.5
    c: DistanceX(g23,g23) = 0.5
    c: Coincident(g13,g30)
    c: Vertical(g30)
    c: Coincident(g30,g31)
    c: Horizontal(g31)
    c: Coincident(g31,g32)
    c: Vertical(g32)
    c: Coincident(g32,g33)
    c: Horizontal(g33)
    c: Coincident(g33,g34)
    c: Vertical(g34)
    c: Coincident(g34,g35)
    c: Horizontal(g35)
    c: Coincident(g35,g36)
    c: Vertical(g36)
    c: Coincident(g36,g37)
    c: Horizontal(g37)
    c: Coincident(g37,g38)
    c: Vertical(g38)
    c: Coincident(g38,g39)
    c: Horizontal(g39)
    c: Coincident(g39,g40)
    c: Vertical(g40)
    c: Coincident(g40,g41)
    c: Horizontal(g41)
    c: DistanceY(g30,g30) = 4
    c: DistanceX(g33,g33) = 1.5
    c: DistanceX(g39,g39) = 1.5
    c: DistanceX(g41,g41) = 3.5
    c: DistanceX(g31,g31) = 3.5
    c: DistanceX(g37,g37) = 0.5
    c: DistanceX(g35,g35) = 0.5
    c: DistanceY(g38,g38) = 1
    c: DistanceY(g40,g40) = 1
    c: DistanceY(g34,g34) = 1
    c: DistanceY(g32,g32) = 1
    c: DistanceX(g17) = 8
    c: DistanceY(g17) = 171
    c: Coincident(g42,g16)
    c: Horizontal(g42)
    c: Coincident(g43,g14)
    c: Horizontal(g43)
    c: DistanceX(g42,g43) = 0.5
    c: Equal(g42,g43)
    c: Horizontal(g42,g43)
    c: Coincident(g0,g29)
    c: DistanceY(g8,g1) = 20
    c: Coincident(g7,g41)
    c: DistanceY(g36,g36) = 2
    c: Coincident(g44,g17)
    c: Horizontal(g44)
    c: Coincident(g45,g15)
    c: Horizontal(g45)
    c: Horizontal(g44,g45)
    c: DistanceX(g44,g45) = 0.5
    c: Equal(g44,g45)
FEATURE [Sketcher::SketchObject] Sketch129
  MapMode = 5
  Support = -> [XY_Plane]
  sketch-geometry (47):
    g0: LineSegment StartX=124 StartY=76 StartZ=0 EndX=127 EndY=76 EndZ=0
    g1: LineSegment StartX=136 StartY=76 StartZ=0 EndX=136 EndY=93 EndZ=0
    g2: ArcOfCircle CenterX=150 CenterY=97 CenterZ=0 NormalX=0 NormalY=0 NormalZ=1 AngleXU=0 Radius=2 StartAngle=4.71239 EndAngle=6.28319
    g3: ArcOfCircle CenterX=150 CenterY=111 CenterZ=0 NormalX=0 NormalY=0 NormalZ=1 AngleXU=0 Radius=2 StartAngle=0 EndAngle=1.5708
    g4: LineSegment StartX=136 StartY=115 StartZ=0 EndX=136 EndY=142 EndZ=0
    g5: LineSegment StartX=127 StartY=142 StartZ=0 EndX=124 EndY=142 EndZ=0
    g6: Circle CenterX=143 CenterY=104 CenterZ=0 NormalX=0 NormalY=0 NormalZ=1 AngleXU=0 Radius=3.4
    g7: LineSegment StartX=124 StartY=142 StartZ=0 EndX=124 EndY=104.25 EndZ=0
    g8: LineSegment StartX=124 StartY=76 StartZ=0 EndX=124 EndY=103.75 EndZ=0
    g9: LineSegment StartX=152 StartY=111 StartZ=0 EndX=152 EndY=104.25 EndZ=0
    g10: LineSegment StartX=152 StartY=97 StartZ=0 EndX=152 EndY=103.75 EndZ=0
    g11: LineSegment StartX=133 StartY=139 StartZ=0 EndX=133 EndY=142 EndZ=0
    g12: LineSegment StartX=133 StartY=142 StartZ=0 EndX=136 EndY=142 EndZ=0
    g13: LineSegment StartX=133 StartY=79 StartZ=0 EndX=133 EndY=76 EndZ=0
    g14: LineSegment StartX=133 StartY=76 StartZ=0 EndX=136 EndY=76 EndZ=0
    g15: LineSegment StartX=150 StartY=113 StartZ=0 EndX=138 EndY=113 EndZ=0
    g16: ArcOfCircle CenterX=138 CenterY=115 CenterZ=0 NormalX=0 NormalY=0 NormalZ=1 AngleXU=0 Radius=2 StartAngle=3.14159 EndAngle=4.71239
    g17: LineSegment StartX=150 StartY=95 StartZ=0 EndX=138 EndY=95 EndZ=0
    g18: ArcOfCircle CenterX=138 CenterY=93 CenterZ=0 NormalX=0 NormalY=0 NormalZ=1 AngleXU=0 Radius=2 StartAngle=1.5708 EndAngle=3.14159
    g19: LineSegment StartX=127 StartY=139 StartZ=0 EndX=127 EndY=142 EndZ=0
    g20: LineSegment StartX=127 StartY=76 StartZ=0 EndX=127 EndY=79 EndZ=0
    g21: LineSegment StartX=127 StartY=79 StartZ=0 EndX=128.5 EndY=79 EndZ=0
    g22: LineSegment StartX=128.5 StartY=79 StartZ=0 EndX=128.5 EndY=83 EndZ=0
    g23: LineSegment StartX=128.5 StartY=83 StartZ=0 EndX=127.2 EndY=83 EndZ=0
    g24: LineSegment StartX=127.2 StartY=83 StartZ=0 EndX=127.2 EndY=85.5 EndZ=0
    g25: LineSegment StartX=127.2 StartY=85.5 StartZ=0 EndX=128.5 EndY=85.5 EndZ=0
    g26: LineSegment StartX=128.5 StartY=85.5 StartZ=0 EndX=128.5 EndY=87 EndZ=0
    g27: LineSegment StartX=128.5 StartY=87 StartZ=0 EndX=131.5 EndY=87 EndZ=0
    g28: LineSegment StartX=131.5 StartY=87 StartZ=0 EndX=131.5 EndY=85.5 EndZ=0
    g29: LineSegment StartX=131.5 StartY=85.5 StartZ=0 EndX=132.8 EndY=85.5 EndZ=0
    g30: LineSegment StartX=132.8 StartY=85.5 StartZ=0 EndX=132.8 EndY=83 EndZ=0
    g31: LineSegment StartX=132.8 StartY=83 StartZ=0 EndX=131.5 EndY=83 EndZ=0
    g32: LineSegment StartX=131.5 StartY=83 StartZ=0 EndX=131.5 EndY=79 EndZ=0
    g33: LineSegment StartX=131.5 StartY=79 StartZ=0 EndX=133 EndY=79 EndZ=0
    g34: LineSegment StartX=127 StartY=139 StartZ=0 EndX=128.5 EndY=139 EndZ=0
    g35: LineSegment StartX=128.5 StartY=139 StartZ=0 EndX=128.5 EndY=135 EndZ=0
    g36: LineSegment StartX=128.5 StartY=135 StartZ=0 EndX=127.2 EndY=135 EndZ=0
    g37: LineSegment StartX=127.2 StartY=135 StartZ=0 EndX=127.2 EndY=132.5 EndZ=0
    g38: LineSegment StartX=127.2 StartY=132.5 StartZ=0 EndX=128.5 EndY=132.5 EndZ=0
    g39: LineSegment StartX=128.5 StartY=132.5 StartZ=0 EndX=128.5 EndY=131 EndZ=0
    g40: LineSegment StartX=128.5 StartY=131 StartZ=0 EndX=131.5 EndY=131 EndZ=0
    g41: LineSegment StartX=131.5 StartY=131 StartZ=0 EndX=131.5 EndY=132.5 EndZ=0
    g42: LineSegment StartX=131.5 StartY=132.5 StartZ=0 EndX=132.8 EndY=132.5 EndZ=0
    g43: LineSegment StartX=132.8 StartY=132.5 StartZ=0 EndX=132.8 EndY=135 EndZ=0
    g44: LineSegment StartX=132.8 StartY=135 StartZ=0 EndX=131.5 EndY=135 EndZ=0
    g45: LineSegment StartX=131.5 StartY=135 StartZ=0 EndX=131.5 EndY=139 EndZ=0
    g46: LineSegment StartX=131.5 StartY=139 StartZ=0 EndX=133 EndY=139 EndZ=0
  constraints (140):
    c: Horizontal(g0)
    c: Vertical(g1)
    c: Vertical(g4)
    c: Horizontal(g5)
    c: Radius(g3) = 2
    c: Radius(g2) = 2
    c: DistanceX(g5,g5) = 3
    c: Radius(g6) = 3.4
    c: DistanceX(g0,g6) = 19
    c: Coincident(g7,g5)
    c: Vertical(g7)
    c: Coincident(g8,g0)
    c: Vertical(g8)
    c: Vertical(g7,g8)
    c: DistanceY(g8,g7) = 0.5
    c: Vertical(g9)
    c: Coincident(g10,g2)
    c: Vertical(g10)
    c: Tangent(g10,g2)
    c: Tangent(g9,g3) = 1.5708
    c: Vertical(g9,g10)
    c: DistanceY(g10,g9) = 0.5
    c: Equal(g9,g10)
    c: Vertical(g11)
    c: Coincident(g11,g12)
    c: Coincident(g12,g4)
    c: Horizontal(g12)
    c: DistanceX(g12,g12) = 3
    c: DistanceX(g0,g0) = 3
    c: Vertical(g13)
    c: Coincident(g13,g14)
    c: Coincident(g14,g1)
    c: Horizontal(g14)
    c: DistanceX(g20,g13) = 6
    c: DistanceX(g14,g14) = 3
    c: DistanceX(g0,g2) = 28
    c: Horizontal(g15)
    c: Tangent(g15,g16) = 1.5708
    c: Tangent(g16,g4) = 1.5708
    c: Tangent(g3,g15) = -1.5708
    c: Horizontal(g17)
    c: Tangent(g17,g18) = -1.5708
    c: Tangent(g18,g1) = 1.5708
    c: Tangent(g2,g17) = 1.5708
    c: Radius(g18) = 2
    c: Radius(g16) = 2
    c: DistanceX(g19,g11) = 6
    c: Coincident(g19,g5)
    c: Vertical(g19)
    c: DistanceY(g6,g7) = 0.25
    c: Coincident(g0,g20)
    c: Vertical(g20)
    c: DistanceY(g0,g5) = 66
    c: DistanceY(g17,g6) = 9
    c: DistanceY(g6,g15) = 9
    c: Coincident(g20,g21)
    c: Horizontal(g21)
    c: Coincident(g21,g22)
    c: Vertical(g22)
    c: Coincident(g22,g23)
    c: Horizontal(g23)
    c: Coincident(g23,g24)
    c: Vertical(g24)
    c: Coincident(g24,g25)
    c: Horizontal(g25)
    c: Coincident(g25,g26)
    c: Vertical(g26)
    c: Coincident(g26,g27)
    c: Horizontal(g27)
    c: Coincident(g27,g28)
    c: Vertical(g28)
    c: Coincident(g28,g29)
    c: Horizontal(g29)
    c: Coincident(g29,g30)
    c: Vertical(g30)
    c: Coincident(g30,g31)
    c: Horizontal(g31)
    c: Coincident(g31,g32)
    c: Vertical(g32)
    c: Coincident(g32,g33)
    c: Coincident(g33,g13)
    c: Horizontal(g33)
    c: DistanceX(g27,g27) = 3
    c: DistanceY(g22,g22) = 4
    c: DistanceY(g24,g24) = 2.5
    c: DistanceY(g26,g26) = 1.5
    c: DistanceY(g20,g20) = 3
    c: DistanceX(g23,g23) = 1.3
    c: DistanceY(g13,g13) = 3
    c: DistanceY(g32,g32) = 4
    c: DistanceY(g30,g30) = 2.5
    c: DistanceY(g28,g28) = 1.5
    c: DistanceX(g25,g25) = 1.3
    c: DistanceX(g21,g21) = 1.5
    c: DistanceX(g33,g33) = 1.5
    c: DistanceX(g31,g31) = 1.3
    c: DistanceX(g0) = 124
    c: DistanceY(g0) = 76
    c: Coincident(g19,g34)
    c: Horizontal(g34)
    c: Coincident(g34,g35)
    c: Vertical(g35)
    c: Coincident(g35,g36)
    c: Horizontal(g36)
    c: Coincident(g36,g37)
    c: Vertical(g37)
    c: Coincident(g37,g38)
    c: Horizontal(g38)
    c: Coincident(g38,g39)
    c: Vertical(g39)
    c: Coincident(g39,g40)
    c: Horizontal(g40)
    c: Coincident(g40,g41)
    c: Vertical(g41)
    c: Coincident(g41,g42)
    c: Horizontal(g42)
    c: Coincident(g42,g43)
    c: Vertical(g43)
    c: Coincident(g43,g44)
    c: Horizontal(g44)
    c: Coincident(g44,g45)
    c: Vertical(g45)
    c: Coincident(g45,g46)
    c: Coincident(g46,g11)
    c: Horizontal(g46)
    c: DistanceY(g19,g19) = 3
    c: DistanceY(g11,g11) = 3
    c: DistanceX(g34,g34) = 1.5
    c: DistanceX(g46,g46) = 1.5
    c: DistanceY(g35,g35) = 4
    c: DistanceY(g45,g45) = 4
    c: DistanceY(g37,g37) = 2.5
    c: DistanceY(g43,g43) = 2.5
    c: DistanceY(g39,g39) = 1.5
    c: DistanceY(g41,g41) = 1.5
    c: DistanceX(g40,g40) = 3
    c: DistanceX(g36,g36) = 1.3
    c: DistanceX(g44,g44) = 1.3
    c: DistanceX(g38,g38) = 1.3
    c: DistanceY(g1,g1) = 17
FEATURE [Sketcher::SketchObject] Sketch130
  MapMode = 5
  Support = -> [XY_Plane]
  sketch-geometry (51):
    g0: LineSegment StartX=169 StartY=142 StartZ=0 EndX=169 EndY=115 EndZ=0
    g1: ArcOfCircle CenterX=155 CenterY=111 CenterZ=0 NormalX=0 NormalY=0 NormalZ=1 AngleXU=0 Radius=2 StartAngle=1.5708 EndAngle=3.14159
    g2: ArcOfCircle CenterX=155 CenterY=97 CenterZ=0 NormalX=0 NormalY=0 NormalZ=1 AngleXU=0 Radius=2 StartAngle=3.14159 EndAngle=4.71239
    g3: LineSegment StartX=169 StartY=93 StartZ=0 EndX=169 EndY=76 EndZ=0
    g4: Circle CenterX=162 CenterY=104 CenterZ=0 NormalX=0 NormalY=0 NormalZ=1 AngleXU=0 Radius=3.4
    g5: LineSegment StartX=181 StartY=142 StartZ=0 EndX=181 EndY=104.25 EndZ=0
    g6: LineSegment StartX=181 StartY=76 StartZ=0 EndX=181 EndY=103.75 EndZ=0
    g7: LineSegment StartX=153 StartY=111 StartZ=0 EndX=153 EndY=104.25 EndZ=0
    g8: LineSegment StartX=153 StartY=97 StartZ=0 EndX=153 EndY=103.75 EndZ=0
    g9: LineSegment StartX=181 StartY=142 StartZ=0 EndX=178 EndY=142 EndZ=0
    g10: LineSegment StartX=178 StartY=142 StartZ=0 EndX=178 EndY=139 EndZ=0
    g11: LineSegment StartX=172 StartY=139 StartZ=0 EndX=172 EndY=142 EndZ=0
    g12: LineSegment StartX=172 StartY=142 StartZ=0 EndX=169 EndY=142 EndZ=0
    g13: LineSegment StartX=181 StartY=76 StartZ=0 EndX=178 EndY=76 EndZ=0
    g14: LineSegment StartX=178 StartY=76 StartZ=0 EndX=178 EndY=79 EndZ=0
    g15: LineSegment StartX=172 StartY=79 StartZ=0 EndX=172 EndY=76 EndZ=0
    g16: LineSegment StartX=172 StartY=76 StartZ=0 EndX=169 EndY=76 EndZ=0
    g17: LineSegment StartX=155 StartY=113 StartZ=0 EndX=167 EndY=113 EndZ=0
    g18: ArcOfCircle CenterX=167 CenterY=115 CenterZ=0 NormalX=0 NormalY=0 NormalZ=1 AngleXU=0 Radius=2 StartAngle=4.71239 EndAngle=6.28319
    g19: LineSegment StartX=155 StartY=95 StartZ=0 EndX=167 EndY=95 EndZ=0
    g20: ArcOfCircle CenterX=167 CenterY=93 CenterZ=0 NormalX=0 NormalY=0 NormalZ=1 AngleXU=0 Radius=2 StartAngle=0 EndAngle=1.5708
    g21: LineSegment StartX=172 StartY=79 StartZ=0 EndX=173.5 EndY=79 EndZ=0
    g22: LineSegment StartX=173.5 StartY=79 StartZ=0 EndX=173.5 EndY=83 EndZ=0
    g23: LineSegment StartX=173.5 StartY=83 StartZ=0 EndX=172.2 EndY=83 EndZ=0
    g24: LineSegment StartX=172.2 StartY=83 StartZ=0 EndX=172.2 EndY=85.5 EndZ=0
    g25: LineSegment StartX=172.2 StartY=85.5 StartZ=0 EndX=173.5 EndY=85.5 EndZ=0
    g26: LineSegment StartX=173.5 StartY=85.5 StartZ=0 EndX=173.5 EndY=87 EndZ=0
    g27: LineSegment StartX=173.5 StartY=87 StartZ=0 EndX=176.5 EndY=87 EndZ=0
    g28: LineSegment StartX=176.5 StartY=87 StartZ=0 EndX=176.5 EndY=85.5 EndZ=0
    g29: LineSegment StartX=176.5 StartY=85.5 StartZ=0 EndX=177.8 EndY=85.5 EndZ=0
    g30: LineSegment StartX=177.8 StartY=85.5 StartZ=0 EndX=177.8 EndY=83 EndZ=0
    g31: LineSegment StartX=177.8 StartY=83 StartZ=0 EndX=176.5 EndY=83 EndZ=0
    g32: LineSegment StartX=176.5 StartY=83 StartZ=0 EndX=176.5 EndY=79 EndZ=0
    g33: LineSegment StartX=176.5 StartY=79 StartZ=0 EndX=178 EndY=79 EndZ=0
    g34: LineSegment StartX=172 StartY=139 StartZ=0 EndX=173.5 EndY=139 EndZ=0
    g35: LineSegment StartX=173.5 StartY=139 StartZ=0 EndX=173.5 EndY=135 EndZ=0
    g36: LineSegment StartX=173.5 StartY=135 StartZ=0 EndX=172.2 EndY=135 EndZ=0
    g37: LineSegment StartX=172.2 StartY=135 StartZ=0 EndX=172.2 EndY=132.5 EndZ=0
    g38: LineSegment StartX=172.2 StartY=132.5 StartZ=0 EndX=173.5 EndY=132.5 EndZ=0
    g39: LineSegment StartX=173.5 StartY=132.5 StartZ=0 EndX=173.5 EndY=131 EndZ=0
    g40: LineSegment StartX=173.5 StartY=131 StartZ=0 EndX=176.5 EndY=131 EndZ=0
    g41: LineSegment StartX=176.5 StartY=131 StartZ=0 EndX=176.5 EndY=132.5 EndZ=0
    g42: LineSegment StartX=176.5 StartY=132.5 StartZ=0 EndX=177.8 EndY=132.5 EndZ=0
    g43: LineSegment StartX=177.8 StartY=132.5 StartZ=0 EndX=177.8 EndY=135 EndZ=0
    g44: LineSegment StartX=177.8 StartY=135 StartZ=0 EndX=176.5 EndY=135 EndZ=0
    g45: LineSegment StartX=176.5 StartY=135 StartZ=0 EndX=176.5 EndY=139 EndZ=0
    g46: LineSegment StartX=176.5 StartY=139 StartZ=0 EndX=178 EndY=139 EndZ=0
    g47: LineSegment [constr] StartX=172 StartY=128 StartZ=0 EndX=175 EndY=128 EndZ=0
    g48: LineSegment [constr] StartX=175 StartY=128 StartZ=0 EndX=175 EndY=118 EndZ=0
    g49: LineSegment [constr] StartX=175 StartY=118 StartZ=0 EndX=172 EndY=118 EndZ=0
    g50: LineSegment [constr] StartX=172 StartY=118 StartZ=0 EndX=172 EndY=128 EndZ=0
  constraints (153):
    c: Vertical(g0)
    c: Vertical(g3)
    c: Radius(g2) = 2
    c: Radius(g1) = 2
    c: Radius(g4) = 3.4
    c: DistanceX(g4,g6) = 19
    c: Vertical(g5)
    c: Vertical(g6)
    c: Vertical(g5,g6)
    c: DistanceY(g6,g5) = 0.5
    c: Vertical(g7)
    c: Coincident(g8,g2)
    c: Vertical(g8)
    c: Tangent(g8,g2)
    c: Tangent(g7,g1) = -1.5708
    c: Vertical(g7,g8)
    c: DistanceY(g8,g7) = 0.5
    c: Equal(g7,g8)
    c: Horizontal(g9)
    c: Coincident(g9,g10)
    c: Vertical(g10)
    c: Vertical(g11)
    c: Coincident(g11,g12)
    c: Coincident(g12,g0)
    c: Horizontal(g12)
    c: Coincident(g13,g14)
    c: Vertical(g14)
    c: Vertical(g15)
    c: Coincident(g15,g16)
    c: Coincident(g16,g3)
    c: Horizontal(g16)
    c: Horizontal(g13)
    c: DistanceX(g13,g13) = 3
    c: DistanceX(g16,g16) = 3
    c: DistanceX(g15,g14) = 6
    c: DistanceX(g2,g6) = 28
    c: DistanceX(g11,g10) = 6
    c: DistanceX(g9,g9) = 3
    c: DistanceX(g12,g12) = 3
    c: Horizontal(g17)
    c: Tangent(g17,g18) = -1.5708
    c: Tangent(g18,g0) = 1.5708
    c: Tangent(g1,g17) = 1.5708
    c: Radius(g18) = 2
    c: Horizontal(g19)
    c: Tangent(g19,g20) = 1.5708
    c: Tangent(g20,g3) = 1.5708
    c: Tangent(g2,g19) = -1.5708
    c: Radius(g20) = 2
    c: Coincident(g6,g13)
    c: Coincident(g5,g9)
    c: DistanceY(g19,g4) = 9
    c: DistanceY(g4,g17) = 9
    c: Horizontal(g6,g8)
    c: Coincident(g15,g21)
    c: Horizontal(g21)
    c: Coincident(g21,g22)
    c: Vertical(g22)
    c: Coincident(g22,g23)
    c: Horizontal(g23)
    c: Coincident(g23,g24)
    c: Vertical(g24)
    c: Coincident(g24,g25)
    c: Horizontal(g25)
    c: Coincident(g25,g26)
    c: Vertical(g26)
    c: Coincident(g26,g27)
    c: Horizontal(g27)
    c: Coincident(g27,g28)
    c: Vertical(g28)
    c: Coincident(g28,g29)
    c: Horizontal(g29)
    c: Coincident(g29,g30)
    c: Vertical(g30)
    c: Coincident(g30,g31)
    c: Horizontal(g31)
    c: Coincident(g31,g32)
    c: Vertical(g32)
    c: Coincident(g32,g33)
    c: Coincident(g33,g14)
    c: Horizontal(g33)
    c: DistanceY(g15,g15) = 3
    c: DistanceY(g14,g14) = 3
    c: DistanceX(g21,g21) = 1.5
    c: DistanceX(g33,g33) = 1.5
    c: DistanceY(g22,g22) = 4
    c: DistanceY(g32,g32) = 4
    c: DistanceX(g23,g23) = 1.3
    c: DistanceX(g31,g31) = 1.3
    c: DistanceY(g24,g24) = 2.5
    c: DistanceY(g30,g30) = 2.5
    c: DistanceX(g25,g25) = 1.3
    c: DistanceX(g29,g29) = 1.3
    c: DistanceY(g26,g26) = 1.5
    c: DistanceY(g28,g28) = 1.5
    c: Coincident(g11,g34)
    c: Horizontal(g34)
    c: Coincident(g34,g35)
    c: Vertical(g35)
    c: Coincident(g35,g36)
    c: Horizontal(g36)
    c: Coincident(g36,g37)
    c: Vertical(g37)
    c: Coincident(g37,g38)
    c: Horizontal(g38)
    c: Coincident(g38,g39)
    c: Vertical(g39)
    c: Coincident(g39,g40)
    c: Horizontal(g40)
    c: Coincident(g40,g41)
    c: Vertical(g41)
    c: Coincident(g41,g42)
    c: Horizontal(g42)
    c: Coincident(g42,g43)
    c: Vertical(g43)
    c: Coincident(g43,g44)
    c: Horizontal(g44)
    c: Coincident(g44,g45)
    c: Vertical(g45)
    c: Coincident(g45,g46)
    c: Coincident(g46,g10)
    c: DistanceY(g11,g11) = 3
    c: DistanceY(g10,g10) = 3
    c: DistanceX(g34,g34) = 1.5
    c: Horizontal(g46)
    c: DistanceX(g46,g46) = 1.5
    c: DistanceY(g35,g35) = 4
    c: DistanceY(g45,g45) = 4
    c: DistanceX(g36,g36) = 1.3
    c: DistanceX(g44,g44) = 1.3
    c: DistanceY(g37,g37) = 2.5
    c: DistanceY(g43,g43) = 2.5
    c: DistanceX(g38,g38) = 1.3
    c: DistanceX(g42,g42) = 1.3
    c: DistanceY(g39,g39) = 1.5
    c: DistanceY(g41,g41) = 1.5
    c: DistanceY(g6,g5) = 66
    c: DistanceX(g3) = 169
    c: DistanceY(g3) = 76
    c: DistanceY(g3,g3) = 17
    c: DistanceY(g17,g11) = 26
    c: Coincident(g47,g48)
    c: Coincident(g48,g49)
    c: Coincident(g49,g50)
    c: Coincident(g50,g47)
    c: Horizontal(g47)
    c: Horizontal(g49)
    c: Vertical(g48)
    c: Vertical(g50)
    c: DistanceX(g49,g49) = 3
    c: DistanceY(g17,g49) = 5
    c: DistanceY(g50,g50) = 10
    c: DistanceX(g0,g49) = 3
FEATURE [Sketcher::SketchObject] Sketch131
  MapMode = 5
  Support = -> [XY_Plane]
  sketch-geometry (12):
    g0: LineSegment StartX=140 StartY=114 StartZ=0 EndX=166 EndY=114 EndZ=0
    g1: LineSegment StartX=166 StartY=132 StartZ=0 EndX=140 EndY=132 EndZ=0
    g2: ArcOfCircle CenterX=140 CenterY=130 CenterZ=0 NormalX=0 NormalY=0 NormalZ=1 AngleXU=0 Radius=2 StartAngle=1.5708 EndAngle=3.14159
    g3: ArcOfCircle CenterX=140 CenterY=116 CenterZ=0 NormalX=0 NormalY=0 NormalZ=1 AngleXU=0 Radius=2 StartAngle=3.14159 EndAngle=4.71239
    g4: LineSegment StartX=147.261 StartY=126.39 StartZ=0 EndX=161.526 EndY=125.293 EndZ=0
    g5: ArcOfCircle CenterX=161.35 CenterY=123 CenterZ=0 NormalX=0 NormalY=0 NormalZ=1 AngleXU=0 Radius=2.3 StartAngle=4.78912 EndAngle=7.77725
    g6: LineSegment StartX=161.526 StartY=120.707 StartZ=0 EndX=147.261 EndY=119.61 EndZ=0
    g7: ArcOfCircle CenterX=147 CenterY=123 CenterZ=0 NormalX=0 NormalY=0 NormalZ=1 AngleXU=0 Radius=3.4 StartAngle=1.49407 EndAngle=4.78912
    g8: LineSegment StartX=138 StartY=130 StartZ=0 EndX=138 EndY=123.25 EndZ=0
    g9: LineSegment StartX=138 StartY=116 StartZ=0 EndX=138 EndY=122.75 EndZ=0
    g10: LineSegment StartX=166 StartY=132 StartZ=0 EndX=166 EndY=123.25 EndZ=0
    g11: LineSegment StartX=166 StartY=114 StartZ=0 EndX=166 EndY=122.75 EndZ=0
  constraints (37):
    c: Horizontal(g0)
    c: Horizontal(g1)
    c: Tangent(g1,g2) = -1.5708
    c: Radius(g3) = 2
    c: Radius(g2) = 2
    c: DistanceX(g1,g1) = 26
    c: Tangent(g4,g5) = 1.5708
    c: Tangent(g6,g7) = 1.5708
    c: Radius(g7) = 3.4
    c: DistanceX(g7,g0) = 19
    c: Horizontal(g5,g7)
    c: DistanceX(g7,g5) = 14.35
    c: Radius(g5) = 2.3
    c: Tangent(g7,g4) = 1.5708
    c: Tangent(g5,g6) = 1.5708
    c: DistanceY(g0,g7) = 9
    c: Vertical(g8)
    c: Vertical(g9)
    c: Tangent(g8,g2) = -1.5708
    c: DistanceY(g9,g8) = 0.5
    c: Vertical(g8,g9)
    c: Equal(g8,g9)
    c: DistanceY(g9,g9) = 6.75
    c: Coincident(g10,g1)
    c: Vertical(g10)
    c: Coincident(g11,g0)
    c: Vertical(g11)
    c: Vertical(g10,g11)
    c: DistanceY(g11,g10) = 0.5
    c: Equal(g10,g11)
    c: DistanceX(g0,g0) = 26
    c: Tangent(g9,g3) = 1.5708
    c: DistanceX(g5,g0) = 4.65
    c: DistanceX(g3,g7) = 9
    c: Tangent(g3,g0) = -1.5708
    c: DistanceX(g0) = 140
    c: DistanceY(g0) = 114
FEATURE [Sketcher::SketchObject] Sketch132
  MapMode = 5
  Support = -> [XY_Plane]
  sketch-geometry (30):
    g0: LineSegment StartX=135 StartY=286 StartZ=0 EndX=168 EndY=286 EndZ=0
    g1: LineSegment StartX=166 StartY=234 StartZ=0 EndX=137 EndY=234 EndZ=0
    g2: ArcOfCircle CenterX=166 CenterY=236 CenterZ=0 NormalX=0 NormalY=0 NormalZ=1 AngleXU=0 Radius=2 StartAngle=4.71239 EndAngle=6.28319
    g3: ArcOfCircle CenterX=137 CenterY=236 CenterZ=0 NormalX=0 NormalY=0 NormalZ=1 AngleXU=0 Radius=2 StartAngle=3.14159 EndAngle=4.71239
    g4: Circle CenterX=151.5 CenterY=281.5 CenterZ=0 NormalX=0 NormalY=0 NormalZ=1 AngleXU=0 Radius=1.5
    g5: Circle CenterX=151.5 CenterY=238.5 CenterZ=0 NormalX=0 NormalY=0 NormalZ=1 AngleXU=0 Radius=1.5
    g6: LineSegment StartX=159 StartY=283 StartZ=0 EndX=164 EndY=283 EndZ=0
    g7: LineSegment StartX=164 StartY=283 StartZ=0 EndX=164 EndY=280 EndZ=0
    g8: LineSegment StartX=164 StartY=280 StartZ=0 EndX=159 EndY=280 EndZ=0
    g9: LineSegment StartX=159 StartY=280 StartZ=0 EndX=159 EndY=283 EndZ=0
    g10: LineSegment StartX=139 StartY=283 StartZ=0 EndX=144 EndY=283 EndZ=0
    g11: LineSegment StartX=144 StartY=283 StartZ=0 EndX=144 EndY=280 EndZ=0
    g12: LineSegment StartX=144 StartY=280 StartZ=0 EndX=139 EndY=280 EndZ=0
    g13: LineSegment StartX=139 StartY=280 StartZ=0 EndX=139 EndY=283 EndZ=0
    g14: LineSegment StartX=139 StartY=240 StartZ=0 EndX=144 EndY=240 EndZ=0
    g15: LineSegment StartX=144 StartY=240 StartZ=0 EndX=144 EndY=237 EndZ=0
    g16: LineSegment StartX=144 StartY=237 StartZ=0 EndX=139 EndY=237 EndZ=0
    g17: LineSegment StartX=139 StartY=237 StartZ=0 EndX=139 EndY=240 EndZ=0
    g18: LineSegment StartX=159 StartY=240 StartZ=0 EndX=164 EndY=240 EndZ=0
    g19: LineSegment StartX=164 StartY=240 StartZ=0 EndX=164 EndY=237 EndZ=0
    g20: LineSegment StartX=164 StartY=237 StartZ=0 EndX=159 EndY=237 EndZ=0
    g21: LineSegment StartX=159 StartY=237 StartZ=0 EndX=159 EndY=240 EndZ=0
    g22: LineSegment StartX=135 StartY=286 StartZ=0 EndX=135 EndY=261.25 EndZ=0
    g23: LineSegment StartX=135 StartY=236 StartZ=0 EndX=135 EndY=260.75 EndZ=0
    g24: LineSegment StartX=151.5 StartY=249 StartZ=0 EndX=152.5 EndY=250.732 EndZ=0
    g25: LineSegment StartX=152.5 StartY=250.732 StartZ=0 EndX=150.5 EndY=250.732 EndZ=0
    g26: LineSegment StartX=150.5 StartY=250.732 StartZ=0 EndX=151.5 EndY=249 EndZ=0
    g27: Circle [constr] CenterX=151.5 CenterY=250.155 CenterZ=0 NormalX=0 NormalY=0 NormalZ=1 AngleXU=0 Radius=1.1547
    g28: LineSegment StartX=168 StartY=286 StartZ=0 EndX=168 EndY=261.25 EndZ=0
    g29: LineSegment StartX=168 StartY=236 StartZ=0 EndX=168 EndY=260.75 EndZ=0
  constraints (91):
    c: Horizontal(g0)
    c: Horizontal(g1)
    c: Tangent(g1,g2) = 1.5708
    c: Tangent(g1,g3) = 1.5708
    c: Radius(g4) = 1.5
    c: Equal(g4,g5)
    c: Coincident(g6,g7)
    c: Coincident(g7,g8)
    c: Coincident(g8,g9)
    c: Coincident(g9,g6)
    c: Horizontal(g6)
    c: Horizontal(g8)
    c: Vertical(g7)
    c: Vertical(g9)
    c: Coincident(g10,g11)
    c: Coincident(g11,g12)
    c: Coincident(g12,g13)
    c: Coincident(g13,g10)
    c: Horizontal(g10)
    c: Horizontal(g12)
    c: Vertical(g11)
    c: Vertical(g13)
    c: Coincident(g14,g15)
    c: Coincident(g15,g16)
    c: Coincident(g16,g17)
    c: Coincident(g17,g14)
    c: Horizontal(g14)
    c: Horizontal(g16)
    c: Vertical(g17)
    c: Coincident(g18,g19)
    c: Coincident(g19,g20)
    c: Coincident(g20,g21)
    c: Coincident(g21,g18)
    c: Horizontal(g18)
    c: Horizontal(g20)
    c: Vertical(g19)
    c: Vertical(g21)
    c: DistanceX(g8,g8) = 5
    c: DistanceY(g9,g9) = 3
    c: DistanceX(g4,g8) = 7.5
    c: DistanceX(g12,g12) = 5
    c: DistanceY(g13,g13) = 3
    c: DistanceX(g11,g4) = 7.5
    c: DistanceX(g20,g20) = 5
    c: DistanceY(g21,g21) = 3
    c: DistanceY(g17,g17) = 3
    c: DistanceX(g16,g16) = 5
    c: DistanceX(g15,g5) = 7.5
    c: DistanceX(g5,g20) = 7.5
    c: Vertical(g22)
    c: Vertical(g23)
    c: DistanceY(g23,g22) = 0.5
    c: Equal(g22,g23)
    c: Tangent(g23,g3) = 1.5708
    c: DistanceX(g3,g16) = 4
    c: DistanceY(g14,g12) = 40
    c: DistanceY(g1,g16) = 3
    c: DistanceY(g10,g0) = 3
    c: DistanceY(g1,g5) = 4.5
    c: DistanceY(g1,g19) = 3
    c: DistanceX(g19,g2) = 4
    c: DistanceY(g4,g0) = 4.5
    c: Vertical(g22,g23)
    c: DistanceY(g6,g0) = 3
    c: Vertical(g15)
    c: Coincident(g0,g22)
    c: DistanceX(g0,g10) = 4
    c: Radius(g2) = 2
    c: Radius(g3) = 2
    c: Coincident(g24,g25)
    c: Coincident(g25,g26)
    c: Coincident(g26,g24)
    c: Equal(g24,g25)
    c: Equal(g24,g26)
    c: PointOnObject(g24,g27)
    c: PointOnObject(g25,g27)
    c: PointOnObject(g26,g27)
    c: Horizontal(g25)
    c: DistanceX(g25,g25) = 2
    c: DistanceY(g1,g24) = 15
    c: Vertical(g28)
    c: Vertical(g29)
    c: Vertical(g28,g29)
    c: DistanceY(g29,g28) = 0.5
    c: Horizontal(g23,g29)
    c: DistanceX(g3,g24) = 16.5
    c: Coincident(g0,g28)
    c: Tangent(g2,g29) = -1.5708
    c: DistanceX(g0,g0) = 33
    c: DistanceX(g1) = 137
    c: DistanceY(g1) = 234
FEATURE [Sketcher::SketchObject] Sketch133
  MapMode = 5
  Support = -> [XY_Plane]
  sketch-geometry (11):
    g0: LineSegment StartX=185 StartY=269 StartZ=0 EndX=185 EndY=266 EndZ=0
    g1: LineSegment StartX=188 StartY=266 StartZ=0 EndX=188 EndY=269 EndZ=0
    g2: ArcOfCircle CenterX=202.938 CenterY=285.182 CenterZ=0 NormalX=0 NormalY=0 NormalZ=1 AngleXU=0 Radius=1 StartAngle=5.49233 EndAngle=8.55211
    g3: LineSegment StartX=202.295 StartY=285.948 StartZ=0 EndX=187.143 EndY=273.234 EndZ=0
    g4: ArcOfCircle CenterX=186.5 CenterY=274 CenterZ=0 NormalX=0 NormalY=0 NormalZ=1 AngleXU=0 Radius=1 StartAngle=4.01426 EndAngle=5.41052
    g5: LineSegment StartX=185.857 StartY=273.234 StartZ=0 EndX=170.705 EndY=285.948 EndZ=0
    g6: ArcOfCircle CenterX=170.062 CenterY=285.182 CenterZ=0 NormalX=0 NormalY=0 NormalZ=1 AngleXU=0 Radius=1 StartAngle=0.872665 EndAngle=3.93245
    g7: LineSegment StartX=169.359 StartY=284.471 StartZ=0 EndX=185 EndY=269 EndZ=0
    g8: LineSegment StartX=203.641 StartY=284.471 StartZ=0 EndX=188 EndY=269 EndZ=0
    g9: LineSegment StartX=185 StartY=266 StartZ=0 EndX=186.25 EndY=266 EndZ=0
    g10: LineSegment StartX=188 StartY=266 StartZ=0 EndX=186.75 EndY=266 EndZ=0
  constraints (32):
    c: Vertical(g0)
    c: Vertical(g1)
    c: Tangent(g3,g4) = 1.5708
    c: Tangent(g5,g6) = -1.5708
    c: Radius(g4) = 1
    c: Radius(g6) = 1
    c: Radius(g2) = 1
    c: Tangent(g4,g5) = 1.5708
    c: Tangent(g2,g3) = -1.5708
    c: DistanceY(g0,g0) = 3
    c: DistanceY(g1,g1) = 3
    c: DistanceX(g0,g4) = 1.5
    c: Horizontal(g3,g4)
    c: Horizontal(g6,g2)
    c: DistanceY(g0,g4) = 8
    c: Angle(g3,g5) = 1.74533
    c: Distance(g0,g6) = 22
    c: Tangent(g2,g8) = 1.5708
    c: Tangent(g6,g7) = -1.5708
    c: DistanceX(g0) = 185
    c: DistanceY(g0) = 266
    c: Coincident(g0,g7)
    c: Coincident(g1,g8)
    c: Coincident(g9,g0)
    c: Horizontal(g9)
    c: Coincident(g10,g1)
    c: Horizontal(g10)
    c: Horizontal(g9,g10)
    c: DistanceX(g9,g10) = 0.5
    c: DistanceX(g9,g9) = 1.25
    c: DistanceX(g10,g10) = 1.25
    c: DistanceX(g0,g1) = 3
FEATURE [Sketcher::SketchObject] Sketch134
  MapMode = 5
  Support = -> [XY_Plane]
  sketch-geometry (46):
    g0: LineSegment StartX=42 StartY=197 StartZ=0 EndX=42 EndY=211 EndZ=0
    g1: LineSegment StartX=42 StartY=211 StartZ=0 EndX=39 EndY=211 EndZ=0
    g2: LineSegment StartX=39 StartY=211 StartZ=0 EndX=39 EndY=221 EndZ=0
    g3: LineSegment StartX=39 StartY=221 StartZ=0 EndX=42 EndY=221 EndZ=0
    g4: LineSegment StartX=69 StartY=221 StartZ=0 EndX=72 EndY=221 EndZ=0
    g5: LineSegment StartX=72 StartY=221 StartZ=0 EndX=72 EndY=211 EndZ=0
    g6: LineSegment StartX=72 StartY=211 StartZ=0 EndX=69 EndY=211 EndZ=0
    g7: LineSegment StartX=69 StartY=211 StartZ=0 EndX=69 EndY=197 EndZ=0
    g8: LineSegment StartX=42 StartY=191 StartZ=0 EndX=39 EndY=191 EndZ=0
    g9: LineSegment StartX=39 StartY=191 StartZ=0 EndX=39 EndY=181 EndZ=0
    g10: LineSegment StartX=39 StartY=181 StartZ=0 EndX=42 EndY=181 EndZ=0
    g11: LineSegment StartX=69 StartY=181 StartZ=0 EndX=72 EndY=181 EndZ=0
    g12: LineSegment StartX=72 StartY=181 StartZ=0 EndX=72 EndY=191 EndZ=0
    g13: LineSegment StartX=72 StartY=191 StartZ=0 EndX=69 EndY=191 EndZ=0
    g14: LineSegment StartX=69 StartY=231 StartZ=0 EndX=69 EndY=221 EndZ=0
    g15: LineSegment StartX=69 StartY=181 StartZ=0 EndX=69 EndY=171 EndZ=0
    g16: LineSegment StartX=42 StartY=231 StartZ=0 EndX=42 EndY=221 EndZ=0
    g17: LineSegment StartX=42 StartY=181 StartZ=0 EndX=42 EndY=171 EndZ=0
    g18: LineSegment StartX=42 StartY=191 StartZ=0 EndX=42 EndY=195 EndZ=0
    g19: LineSegment StartX=42 StartY=195 StartZ=0 EndX=45.5 EndY=195 EndZ=0
    g20: LineSegment StartX=45.5 StartY=195 StartZ=0 EndX=45.5 EndY=194 EndZ=0
    g21: LineSegment StartX=45.5 StartY=194 StartZ=0 EndX=47 EndY=194 EndZ=0
    g22: LineSegment StartX=47 StartY=194 StartZ=0 EndX=47 EndY=195 EndZ=0
    g23: LineSegment StartX=47 StartY=195 StartZ=0 EndX=47.5 EndY=195 EndZ=0
    g24: LineSegment StartX=47.5 StartY=195 StartZ=0 EndX=47.5 EndY=197 EndZ=0
    g25: LineSegment StartX=47.5 StartY=197 StartZ=0 EndX=47 EndY=197 EndZ=0
    g26: LineSegment StartX=47 StartY=197 StartZ=0 EndX=47 EndY=198 EndZ=0
    g27: LineSegment StartX=47 StartY=198 StartZ=0 EndX=45.5 EndY=198 EndZ=0
    g28: LineSegment StartX=45.5 StartY=198 StartZ=0 EndX=45.5 EndY=197 EndZ=0
    g29: LineSegment StartX=45.5 StartY=197 StartZ=0 EndX=42 EndY=197 EndZ=0
    g30: LineSegment StartX=69 StartY=191 StartZ=0 EndX=69 EndY=195 EndZ=0
    g31: LineSegment StartX=69 StartY=195 StartZ=0 EndX=65.5 EndY=195 EndZ=0
    g32: LineSegment StartX=65.5 StartY=195 StartZ=0 EndX=65.5 EndY=194 EndZ=0
    g33: LineSegment StartX=65.5 StartY=194 StartZ=0 EndX=64 EndY=194 EndZ=0
    g34: LineSegment StartX=64 StartY=194 StartZ=0 EndX=64 EndY=195 EndZ=0
    g35: LineSegment StartX=64 StartY=195 StartZ=0 EndX=63.5 EndY=195 EndZ=0
    g36: LineSegment StartX=63.5 StartY=195 StartZ=0 EndX=63.5 EndY=197 EndZ=0
    g37: LineSegment StartX=63.5 StartY=197 StartZ=0 EndX=64 EndY=197 EndZ=0
    g38: LineSegment StartX=64 StartY=197 StartZ=0 EndX=64 EndY=198 EndZ=0
    g39: LineSegment StartX=64 StartY=198 StartZ=0 EndX=65.5 EndY=198 EndZ=0
    g40: LineSegment StartX=65.5 StartY=198 StartZ=0 EndX=65.5 EndY=197 EndZ=0
    g41: LineSegment StartX=65.5 StartY=197 StartZ=0 EndX=69 EndY=197 EndZ=0
    g42: LineSegment StartX=42 StartY=231 StartZ=0 EndX=55.25 EndY=231 EndZ=0
    g43: LineSegment StartX=69 StartY=231 StartZ=0 EndX=55.75 EndY=231 EndZ=0
    g44: LineSegment StartX=42 StartY=171 StartZ=0 EndX=55.25 EndY=171 EndZ=0
    g45: LineSegment StartX=69 StartY=171 StartZ=0 EndX=55.75 EndY=171 EndZ=0
  constraints (140):
    c: Vertical(g0)
    c: Coincident(g0,g1)
    c: Horizontal(g1)
    c: Coincident(g1,g2)
    c: Vertical(g2)
    c: Coincident(g2,g3)
    c: Horizontal(g3)
    c: Horizontal(g4)
    c: Coincident(g4,g5)
    c: Vertical(g5)
    c: Coincident(g5,g6)
    c: Horizontal(g6)
    c: Coincident(g6,g7)
    c: Vertical(g7)
    c: Horizontal(g8)
    c: Coincident(g8,g9)
    c: Vertical(g9)
    c: Coincident(g9,g10)
    c: Horizontal(g10)
    c: DistanceY(g3,g16) = 10
    c: DistanceY(g2,g2) = 10
    c: DistanceY(g9,g9) = 10
    c: DistanceY(g17,g10) = 10
    c: DistanceX(g16,g14) = 27
    c: DistanceX(g3,g3) = 3
    c: DistanceX(g1,g1) = 3
    c: DistanceX(g8,g8) = 3
    c: DistanceX(g10,g10) = 3
    c: DistanceY(g4,g14) = 10
    c: DistanceY(g5,g5) = 10
    c: DistanceX(g4,g4) = 3
    c: DistanceX(g6,g6) = 3
    c: DistanceX(g17,g15) = 27
    c: Horizontal(g11)
    c: Coincident(g11,g12)
    c: Vertical(g12)
    c: Coincident(g12,g13)
    c: Horizontal(g13)
    c: DistanceY(g15,g11) = 10
    c: DistanceY(g12,g12) = 10
    c: DistanceX(g11,g11) = 3
    c: Coincident(g14,g4)
    c: Vertical(g14)
    c: Coincident(g11,g15)
    c: Vertical(g15)
    c: Coincident(g16,g3)
    c: Vertical(g16)
    c: Coincident(g10,g17)
    c: Vertical(g17)
    c: Coincident(g8,g18)
    c: Vertical(g18)
    c: Coincident(g18,g19)
    c: Horizontal(g19)
    c: Coincident(g19,g20)
    c: Vertical(g20)
    c: Coincident(g20,g21)
    c: Horizontal(g21)
    c: Coincident(g21,g22)
    c: Vertical(g22)
    c: Coincident(g22,g23)
    c: Horizontal(g23)
    c: Coincident(g23,g24)
    c: Vertical(g24)
    c: Coincident(g24,g25)
    c: Horizontal(g25)
    c: Coincident(g25,g26)
    c: Vertical(g26)
    c: Coincident(g26,g27)
    c: Horizontal(g27)
    c: Coincident(g27,g28)
    c: Vertical(g28)
    c: Coincident(g28,g29)
    c: Horizontal(g29)
    c: DistanceY(g18,g18) = 4
    c: DistanceY(g20,g20) = 1
    c: DistanceY(g28,g28) = 1
    c: DistanceY(g26,g26) = 1
    c: DistanceY(g22,g22) = 1
    c: DistanceY(g24,g24) = 2
    c: DistanceX(g27,g27) = 1.5
    c: DistanceX(g21,g21) = 1.5
    c: DistanceX(g29,g29) = 3.5
    c: DistanceX(g25,g25) = 0.5
    c: DistanceX(g19,g19) = 3.5
    c: DistanceX(g23,g23) = 0.5
    c: Coincident(g13,g30)
    c: Vertical(g30)
    c: Coincident(g30,g31)
    c: Horizontal(g31)
    c: Coincident(g31,g32)
    c: Vertical(g32)
    c: Coincident(g32,g33)
    c: Horizontal(g33)
    c: Coincident(g33,g34)
    c: Vertical(g34)
    c: Coincident(g34,g35)
    c: Horizontal(g35)
    c: Coincident(g35,g36)
    c: Vertical(g36)
    c: Coincident(g36,g37)
    c: Horizontal(g37)
    c: Coincident(g37,g38)
    c: Vertical(g38)
    c: Coincident(g38,g39)
    c: Horizontal(g39)
    c: Coincident(g39,g40)
    c: Vertical(g40)
    c: Coincident(g40,g41)
    c: Horizontal(g41)
    c: DistanceY(g30,g30) = 4
    c: DistanceX(g33,g33) = 1.5
    c: DistanceX(g39,g39) = 1.5
    c: DistanceX(g41,g41) = 3.5
    c: DistanceX(g31,g31) = 3.5
    c: DistanceX(g37,g37) = 0.5
    c: DistanceX(g35,g35) = 0.5
    c: DistanceY(g38,g38) = 1
    c: DistanceY(g40,g40) = 1
    c: DistanceY(g34,g34) = 1
    c: DistanceY(g32,g32) = 1
    c: DistanceX(g17) = 42
    c: DistanceY(g17) = 171
    c: Coincident(g42,g16)
    c: Horizontal(g42)
    c: Coincident(g43,g14)
    c: Horizontal(g43)
    c: DistanceX(g42,g43) = 0.5
    c: Equal(g42,g43)
    c: Horizontal(g42,g43)
    c: Coincident(g0,g29)
    c: DistanceY(g8,g1) = 20
    c: Coincident(g7,g41)
    c: DistanceY(g36,g36) = 2
    c: Coincident(g44,g17)
    c: Horizontal(g44)
    c: Coincident(g45,g15)
    c: Horizontal(g45)
    c: Horizontal(g44,g45)
    c: DistanceX(g44,g45) = 0.5
    c: Equal(g44,g45)
FEATURE [Sketcher::SketchObject] Sketch135
  MapMode = 5
  Support = -> [XY_Plane]
  sketch-geometry (25):
    g0: ArcOfCircle CenterX=189 CenterY=63 CenterZ=0 NormalX=0 NormalY=0 NormalZ=1 AngleXU=0 Radius=2 StartAngle=1.5708 EndAngle=3.14159
    g1: LineSegment StartX=189 StartY=65 StartZ=0 EndX=205.1 EndY=65 EndZ=0
    g2: LineSegment StartX=190 StartY=59 StartZ=0 EndX=202.1 EndY=59 EndZ=0
    g3: LineSegment StartX=202.1 StartY=59 StartZ=0 EndX=202.1 EndY=55 EndZ=0
    g4: LineSegment StartX=202.1 StartY=36.5 StartZ=0 EndX=190 EndY=36.5 EndZ=0
    g5: Circle CenterX=196.05 CenterY=61.5 CenterZ=0 NormalX=0 NormalY=0 NormalZ=1 AngleXU=0 Radius=1
    g6: Circle CenterX=196.05 CenterY=34 CenterZ=0 NormalX=0 NormalY=0 NormalZ=1 AngleXU=0 Radius=1
    g7: LineSegment StartX=202.1 StartY=55 StartZ=0 EndX=205.1 EndY=55 EndZ=0
    g8: LineSegment StartX=205.1 StartY=55 StartZ=0 EndX=205.1 EndY=65 EndZ=0
    g9: ArcOfCircle CenterX=189 CenterY=7 CenterZ=0 NormalX=0 NormalY=0 NormalZ=1 AngleXU=0 Radius=2 StartAngle=3.14159 EndAngle=4.71239
    g10: LineSegment StartX=189 StartY=5 StartZ=0 EndX=205.1 EndY=5 EndZ=0
    g11: LineSegment StartX=205.1 StartY=45 StartZ=0 EndX=202.1 EndY=45 EndZ=0
    g12: LineSegment StartX=202.1 StartY=45 StartZ=0 EndX=202.1 EndY=36.5 EndZ=0
    g13: LineSegment StartX=187 StartY=63 StartZ=0 EndX=187 EndY=35.25 EndZ=0
    g14: LineSegment StartX=187 StartY=7 StartZ=0 EndX=187 EndY=34.75 EndZ=0
    g15: LineSegment StartX=190 StartY=36.5 StartZ=0 EndX=190 EndY=59 EndZ=0
    g16: LineSegment StartX=205.1 StartY=25 StartZ=0 EndX=202.1 EndY=25 EndZ=0
    g17: LineSegment StartX=202.1 StartY=25 StartZ=0 EndX=202.1 EndY=15 EndZ=0
    g18: LineSegment StartX=202.1 StartY=15 StartZ=0 EndX=205.1 EndY=15 EndZ=0
    g19: LineSegment StartX=205.1 StartY=15 StartZ=0 EndX=205.1 EndY=5 EndZ=0
    g20: Circle CenterX=203.6 CenterY=30 CenterZ=0 NormalX=0 NormalY=0 NormalZ=1 AngleXU=0 Radius=1
    g21: LineSegment StartX=205.1 StartY=45 StartZ=0 EndX=205.1 EndY=35.25 EndZ=0
    g22: LineSegment StartX=205.1 StartY=25 StartZ=0 EndX=205.1 EndY=27.4019 EndZ=0
    g23: ArcOfCircle CenterX=203.6 CenterY=30 CenterZ=0 NormalX=0 NormalY=0 NormalZ=1 AngleXU=0 Radius=3 StartAngle=5.23599 EndAngle=7.33038
    g24: LineSegment StartX=205.1 StartY=32.5981 StartZ=0 EndX=205.1 EndY=34.75 EndZ=0
  constraints (75):
    c: Horizontal(g1)
    c: Tangent(g0,g1) = 1.5708
    c: Radius(g0) = 2
    c: Coincident(g2,g3)
    c: Coincident(g12,g4)
    c: Horizontal(g2)
    c: Horizontal(g4)
    c: Vertical(g3)
    c: DistanceX(g4,g4) = 12.1
    c: DistanceY(g4,g2) = 22.5
    c: DistanceY(g2,g0) = 6
    c: Radius(g6) = 1
    c: Radius(g5) = 1
    c: DistanceY(g2,g5) = 2.5
    c: DistanceY(g6,g4) = 2.5
    c: DistanceX(g4,g6) = 6.05
    c: DistanceX(g2,g5) = 6.05
    c: Horizontal(g7)
    c: Coincident(g7,g8)
    c: Vertical(g8)
    c: DistanceX(g7,g7) = 3
    c: Coincident(g1,g8)
    c: Horizontal(g10)
    c: Horizontal(g11)
    c: PointOnObject(g3,g7)
    c: Coincident(g12,g11)
    c: Tangent(g3,g12)
    c: DistanceX(g11,g11) = 3
    c: Tangent(g9,g10) = -1.5708
    c: Radius(g9) = 2
    c: DistanceY(g11,g3) = 10
    c: Coincident(g3,g7)
    c: DistanceY(g7,g1) = 10
    c: DistanceY(g10,g1) = 60
    c: Vertical(g13)
    c: Vertical(g14)
    c: Coincident(g15,g4)
    c: Vertical(g15)
    c: Vertical(g13,g14)
    c: DistanceY(g14,g13) = 0.5
    c: Tangent(g13,g0) = -1.5708
    c: Tangent(g14,g9) = 1.5708
    c: Equal(g14,g13)
    c: DistanceX(g9,g4) = 3
    c: Horizontal(g16)
    c: Coincident(g16,g17)
    c: Vertical(g17)
    c: Coincident(g17,g18)
    c: Horizontal(g18)
    c: Coincident(g18,g19)
    c: Coincident(g19,g10)
    c: Vertical(g19)
    c: DistanceY(g19,g19) = 10
    c: DistanceY(g17,g17) = 10
    c: DistanceX(g18,g18) = 3
    c: DistanceX(g16,g16) = 3
    c: Radius(g20) = 1
    c: DistanceY(g10,g20) = 25
    c: DistanceX(g20,g10) = 1.5
    c: Coincident(g2,g15)
    c: Coincident(g21,g11)
    c: Vertical(g21)
    c: Coincident(g16,g22)
    c: Vertical(g22)
    c: Coincident(g23,g24)
    c: Vertical(g24)
    c: Vertical(g21,g24)
    c: DistanceY(g24,g21) = 0.5
    c: Coincident(g20,g23)
    c: Coincident(g22,g23)
    c: Radius(g23) = 3
    c: Horizontal(g14,g24)
    c: Vertical(g22,g23)
    c: DistanceX(g9) = 189
    c: DistanceY(g9) = 5
FEATURE [Sketcher::SketchObject] Sketch136
  MapMode = 5
  sketch-geometry (30):
    g0: LineSegment StartX=187 StartY=233 StartZ=0 EndX=201 EndY=233 EndZ=0
    g1: LineSegment StartX=203 StartY=231 StartZ=0 EndX=203 EndY=230 EndZ=0
    g2: LineSegment StartX=201 StartY=192 StartZ=0 EndX=187 EndY=192 EndZ=0
    g3: LineSegment StartX=185 StartY=194 StartZ=0 EndX=185 EndY=195 EndZ=0
    g4: ArcOfCircle CenterX=187 CenterY=231 CenterZ=0 NormalX=0 NormalY=0 NormalZ=1 AngleXU=0 Radius=2 StartAngle=1.5708 EndAngle=3.14159
    g5: ArcOfCircle CenterX=201 CenterY=231 CenterZ=0 NormalX=0 NormalY=0 NormalZ=1 AngleXU=0 Radius=2 StartAngle=0 EndAngle=1.5708
    g6: ArcOfCircle CenterX=187 CenterY=194 CenterZ=0 NormalX=0 NormalY=0 NormalZ=1 AngleXU=0 Radius=2 StartAngle=3.14159 EndAngle=4.71239
    g7: ArcOfCircle CenterX=201 CenterY=194 CenterZ=0 NormalX=0 NormalY=0 NormalZ=1 AngleXU=0 Radius=2 StartAngle=4.71239 EndAngle=6.28319
    g8: LineSegment StartX=199 StartY=198 StartZ=0 EndX=203 EndY=198 EndZ=0
    g9: LineSegment StartX=203 StartY=195 StartZ=0 EndX=199 EndY=195 EndZ=0
    g10: LineSegment StartX=199 StartY=195 StartZ=0 EndX=199 EndY=198 EndZ=0
    g11: Circle CenterX=194 CenterY=196.5 CenterZ=0 NormalX=0 NormalY=0 NormalZ=1 AngleXU=0 Radius=1.5
    g12: LineSegment [constr] StartX=194 StartY=192 StartZ=0 EndX=194 EndY=233 EndZ=0
    g13: LineSegment StartX=203 StartY=195 StartZ=0 EndX=203 EndY=194 EndZ=0
    g14: LineSegment StartX=185 StartY=198 StartZ=0 EndX=189 EndY=198 EndZ=0
    g15: LineSegment StartX=185 StartY=195 StartZ=0 EndX=189 EndY=195 EndZ=0
    g16: LineSegment StartX=189 StartY=198 StartZ=0 EndX=189 EndY=195 EndZ=0
    g17: LineSegment StartX=199 StartY=230 StartZ=0 EndX=203 EndY=230 EndZ=0
    g18: LineSegment StartX=203 StartY=227 StartZ=0 EndX=199 EndY=227 EndZ=0
    g19: LineSegment StartX=199 StartY=227 StartZ=0 EndX=199 EndY=230 EndZ=0
    g20: LineSegment StartX=185 StartY=227 StartZ=0 EndX=189 EndY=227 EndZ=0
    g21: LineSegment StartX=189 StartY=227 StartZ=0 EndX=189 EndY=230 EndZ=0
    g22: LineSegment StartX=189 StartY=230 StartZ=0 EndX=185 EndY=230 EndZ=0
    g23: Circle CenterX=194 CenterY=228.5 CenterZ=0 NormalX=0 NormalY=0 NormalZ=1 AngleXU=0 Radius=1.5
    g24: LineSegment StartX=185 StartY=230 StartZ=0 EndX=185 EndY=231 EndZ=0
    g25: Circle CenterX=194 CenterY=219 CenterZ=0 NormalX=0 NormalY=0 NormalZ=1 AngleXU=0 Radius=3.4
    g26: LineSegment StartX=203 StartY=227 StartZ=0 EndX=203 EndY=212.75 EndZ=0
    g27: LineSegment StartX=203 StartY=198 StartZ=0 EndX=203 EndY=212.25 EndZ=0
    g28: LineSegment StartX=185 StartY=227 StartZ=0 EndX=185 EndY=212.75 EndZ=0
    g29: LineSegment StartX=185 StartY=198 StartZ=0 EndX=185 EndY=212.25 EndZ=0
  constraints (92):
    c: Horizontal(g0)
    c: Horizontal(g2)
    c: Vertical(g1)
    c: Vertical(g3)
    c: Tangent(g0,g4) = 1.5708
    c: Tangent(g0,g5) = 1.5708
    c: Tangent(g1,g5) = 1.5708
    c: Tangent(g2,g6) = 1.5708
    c: Tangent(g3,g6) = 1.5708
    c: Radius(g4) = 2
    c: Equal(g4,g5)
    c: Equal(g4,g6)
    c: Equal(g4,g7)
    c: DistanceX(g3,g13) = 18
    c: Coincident(g9,g10)
    c: Coincident(g10,g8)
    c: Horizontal(g8)
    c: Horizontal(g9)
    c: Vertical(g10)
    c: PointOnObject(g9,g1)
    c: DistanceY(g2,g9) = 3
    c: DistanceY(g10,g10) = 3
    c: DistanceX(g9,g9) = 4
    c: PointOnObject(g12,g2)
    c: PointOnObject(g12,g0)
    c: Vertical(g12)
    c: Symmetric(g3,g13,g12)
    c: PointOnObject(g11,g12)
    c: Radius(g11) = 1.5
    c: DistanceY(g12,g11) = 4.5
    c: PointOnObject(g13,g9)
    c: PointOnObject(g8,g1)
    c: PointOnObject(g14,g3)
    c: Horizontal(g14,g8)
    c: Horizontal(g3,g9)
    c: Horizontal(g14)
    c: Coincident(g15,g3)
    c: Horizontal(g15)
    c: Coincident(g16,g14)
    c: Coincident(g16,g15)
    c: Vertical(g16)
    c: DistanceX(g15,g15) = 4
    c: Horizontal(g4,g4)
    c: Coincident(g18,g19)
    c: Coincident(g19,g17)
    c: Horizontal(g17)
    c: Horizontal(g18)
    c: Vertical(g19)
    c: PointOnObject(g18,g1)
    c: Coincident(g20,g21)
    c: Coincident(g21,g22)
    c: Horizontal(g20)
    c: Horizontal(g22)
    c: Vertical(g21)
    c: PointOnObject(g23,g12)
    c: DistanceY(g23,g12) = 4.5
    c: DistanceY(g17,g0) = 3
    c: DistanceY(g22,g0) = 3
    c: DistanceY(g21,g21) = 3
    c: DistanceY(g19,g19) = 3
    c: Radius(g23) = 1.5
    c: DistanceX(g18,g18) = 4
    c: PointOnObject(g1,g17)
    c: DistanceX(g17,g17) = 4
    c: PointOnObject(g24,g22)
    c: DistanceX(g20,g20) = 4
    c: DistanceX(g22,g22) = 4
    c: PointOnObject(g25,g12)
    c: Radius(g25) = 3.4
    c: Coincident(g26,g18)
    c: Vertical(g26)
    c: Coincident(g27,g8)
    c: Vertical(g27)
    c: DistanceY(g27,g26) = 0.5
    c: Equal(g26,g27)
    c: Coincident(g28,g20)
    c: Vertical(g28)
    c: Coincident(g29,g14)
    c: Vertical(g29)
    c: DistanceY(g29,g28) = 0.5
    c: Equal(g28,g29)
    c: Tangent(g24,g4) = 1.5708
    c: Coincident(g24,g22)
    c: DistanceX(g4,g1) = 18
    c: DistanceY(g12,g25) = 27
    c: Tangent(g13,g7) = 1.5708
    c: Tangent(g2,g7) = 1.5708
    c: Coincident(g9,g13)
    c: DistanceY(g14,g20) = 29
    c: DistanceY(g25,g20) = 8
    c: DistanceX(g2) = 187
    c: DistanceY(g2) = 192
FEATURE [PartDesign::Body] Body
  Group = -> [Sketch025,Sketch039,Sketch046,Sketch051,Sketch052,Sketch064,Sketch083,Sketch084,Sketch094,Sketch095,Sketch099,Sketch100,Sketch101,Sketch102,Sketch103,Sketch104,Sketch105,Sketch107,Sketch108,Sketch003,Sketch110,Sketch109,Sketch112,Sketch116,Sketch117,Sketch124,Sketch125,Sketch128,Sketch129,Sketch130,Sketch131,Sketch132,Sketch133,Sketch134,Sketch135,Sketch136]
  Origin = -> Origin
